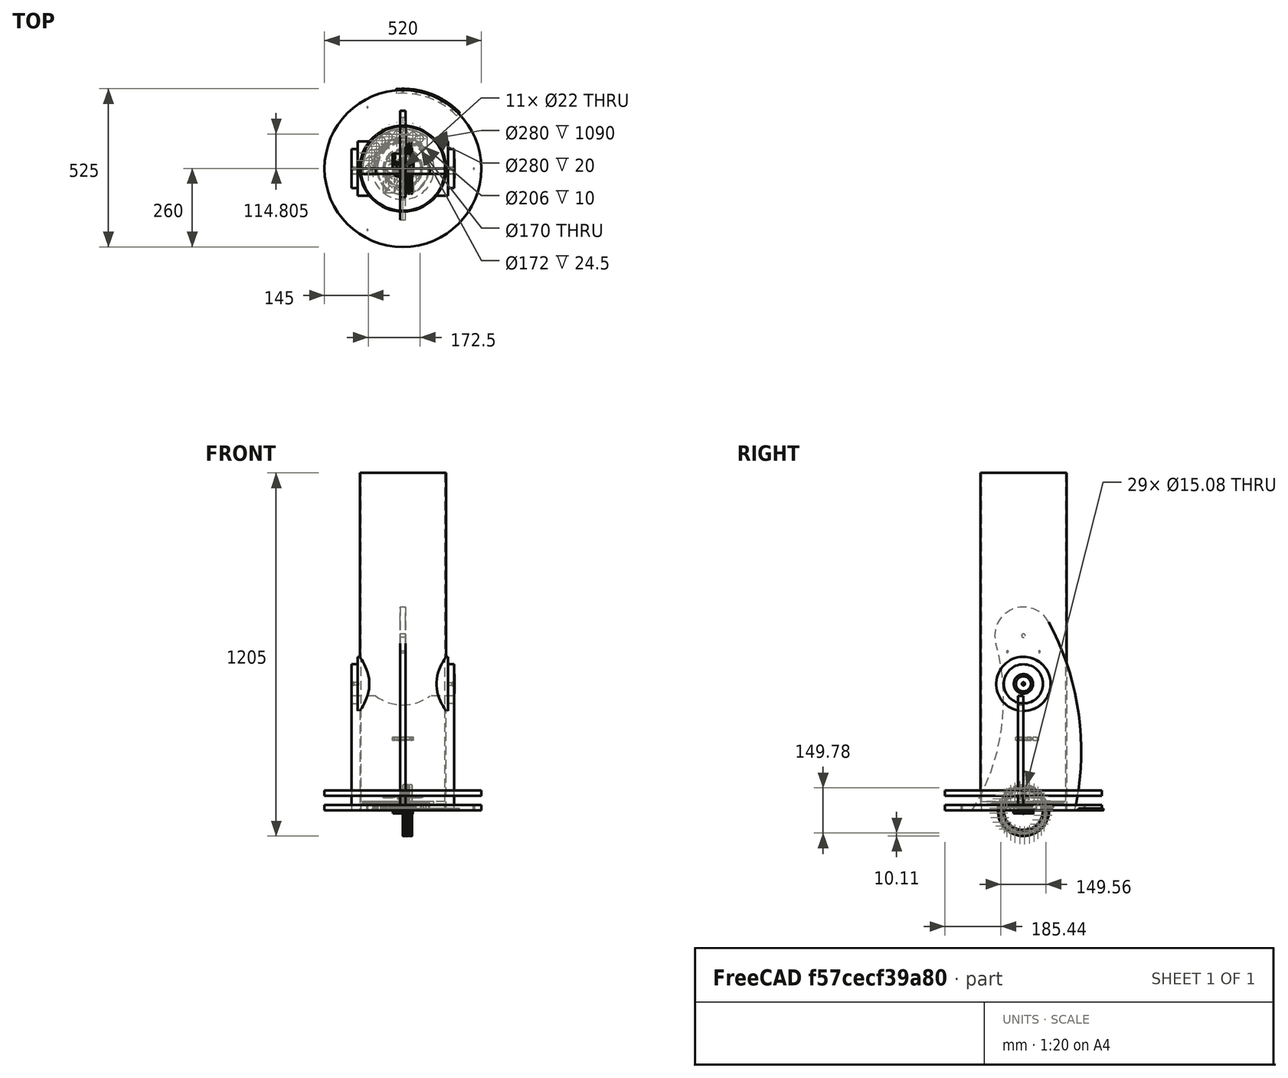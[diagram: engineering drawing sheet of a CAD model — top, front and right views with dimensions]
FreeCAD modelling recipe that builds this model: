
FCSTD DOCUMENT  (FreeCAD 1.1R20251125 (Git shallow))
Label: telescope
License: All rights reserved
LicenseURL: https://en.wikipedia.org/wiki/All_rights_reserved
objects: Sketcher::SketchObject×83, App::Link×62, PartDesign::Pocket×49, App::FeaturePython×38, App::Point×33, PartDesign::Pad×26, PartDesign::Body×21, Part::Feature×14, PartDesign::Chamfer×12, PartDesign::PolarPattern×8, App::Part×8, PartDesign::Fillet×7, PartDesign::LinearPattern×6, PartDesign::FeatureBase×6, Part::FeaturePython×6, PartDesign::MultiTransform×4, PartDesign::Plane×4, PartDesign::Groove×4, Assembly::JointGroup×4, Assembly::AssemblyObject×4, +6 more types
note: 565 computed .brp shape members not serialized (recipe doc carries the construction recipe); baked Part::Feature solids carry a one-line shape summary decoded from their .brp

FEATURE [Sketcher::SketchObject] Sketch002
  ArcFitTolerance = 0
  AttachmentSupport = -> [XY_Plane]
  ExternalTypes = [0]
  FullyConstrained = true
  MakeInternals = false
  MapMode = 5
  sketch-geometry (1):
    g0: Circle CenterX=0 CenterY=0 CenterZ=0 NormalX=0 NormalY=0 NormalZ=1 AngleXU=0 Radius=7
  constraints (2):
    c: Coincident(g0,g-1)
    c: Diameter(g0) = 14
FEATURE [Sketcher::SketchObject] Sketch
  ArcFitTolerance = 0
  AttachmentSupport = -> [XY_Plane]
  ExternalTypes = [0]
  FullyConstrained = true
  MakeInternals = false
  MapMode = 5
  sketch-geometry (1):
    g0: Circle CenterX=0 CenterY=0 CenterZ=0 NormalX=0 NormalY=0 NormalZ=1 AngleXU=0 Radius=260
  constraints (2):
    c: Coincident(g0,g-1)
    c: Diameter(g0) = 520
FEATURE [PartDesign::Pad] Pad
  AllowMultiFace = false
  Direction = (0,0,1)
  Length = 18
  Length2 = 100
  Profile = -> Sketch
  SideType = 0
  Suppressed = false
  Type = 0
  Type2 = 0
FEATURE [Sketcher::SketchObject] Sketch001
  ArcFitTolerance = 0
  AttachmentSupport = -> [Pad]
  ExternalTypes = [0]
  FullyConstrained = true
  MakeInternals = false
  MapMode = 5
  Placement = pos=(0,0,18) rot=(0,0,1;0rad)
  sketch-geometry (1):
    g0: Circle CenterX=235 CenterY=0 CenterZ=0 NormalX=0 NormalY=0 NormalZ=1 AngleXU=0 Radius=2
  constraints (3):
    c: PointOnObject(g0,g-1)
    c: DistanceX(g0) = 235
    c: Radius(g0) = 2
FEATURE [PartDesign::Pocket] Pocket
  AllowMultiFace = false
  BaseFeature = -> Pad
  Direction = (0,0,-1)
  Length = 5
  Length2 = 100
  Profile = -> Sketch001
  SideType = 0
  Suppressed = false
  Type = 1
  Type2 = 0
FEATURE [PartDesign::PolarPattern] PolarPattern
  Angle = 360
  Axis = -> Sketch001 [N_Axis]
  BaseFeature = -> Pocket
  Mode = 0
  Occurrences = 3
  Offset = 120
  Originals = -> [Pocket]
  SpacingPattern = [0]
  Spacings = [-1,-1]
  Suppressed = false
  TransformMode = 0
FEATURE [PartDesign::Pocket] Pocket001
  BaseFeature = -> PolarPattern
  Direction = (0,0,-1)
  Length = 5
  Length2 = 100
  Profile = -> Sketch002
  Reversed = true
  SideType = 0
  Suppressed = false
  Type = 1
  Type2 = 0
FEATURE [PartDesign::Body] Body  label="base_bottom_plate"
  AllowCompound = true
  Group = -> [Sketch,Pad,Sketch001,Pocket,PolarPattern,Sketch002,Pocket001]
  Origin = -> Origin
  Tip = -> Pocket001
FEATURE [Part::Feature] Solid001  label="_51126_PART2"
  shape: bbox 9.646 x 184 x 184 mm, 9 faces (baked)
FEATURE [Part::Feature] Solid003  label="_51126_PART4"
  shape: bbox 15.08 x 15.08 x 15.08 mm, 1 faces (baked)
FEATURE [App::Link] Link004  label="_51126_PART009"
  LinkPlacement = pos=(0,0,0) rot=(-1,0,0;1.08331rad)
  LinkedObject = -> Solid003
  Placement = pos=(0,0,0) rot=(-1,0,0;1.08331rad)
FEATURE [App::Link] Link  label="_51126_PART005"
  LinkPlacement = pos=(0,0,0) rot=(-1,0,0;0.216662rad)
  LinkedObject = -> Solid003
  Placement = pos=(0,0,0) rot=(-1,0,0;0.216662rad)
FEATURE [App::Link] Link017  label="_51126_PART022"
  LinkPlacement = pos=(0,0,0) rot=(1,0,0;2.38328rad)
  LinkedObject = -> Solid003
  Placement = pos=(0,0,0) rot=(1,0,0;2.38328rad)
FEATURE [App::Link] Link002  label="_51126_PART007"
  LinkPlacement = pos=(0,0,0) rot=(-1,0,0;0.649985rad)
  LinkedObject = -> Solid003
  Placement = pos=(0,0,0) rot=(-1,0,0;0.649985rad)
FEATURE [App::Link] Link027  label="_51126_PART032"
  LinkPlacement = pos=(0,0,0) rot=(1,0,0;0.216662rad)
  LinkedObject = -> Solid003
  Placement = pos=(0,0,0) rot=(1,0,0;0.216662rad)
FEATURE [App::Link] Link023  label="_51126_PART028"
  LinkPlacement = pos=(0,0,0) rot=(1,0,0;1.08331rad)
  LinkedObject = -> Solid003
  Placement = pos=(0,0,0) rot=(1,0,0;1.08331rad)
FEATURE [App::Link] Link024  label="_51126_PART029"
  LinkPlacement = pos=(0,0,0) rot=(1,0,0;0.866646rad)
  LinkedObject = -> Solid003
  Placement = pos=(0,0,0) rot=(1,0,0;0.866646rad)
FEATURE [App::Link] Link010  label="_51126_PART015"
  LinkPlacement = pos=(0,0,0) rot=(1,0,0;3.89991rad)
  LinkedObject = -> Solid003
  Placement = pos=(0,0,0) rot=(1,0,0;3.89991rad)
FEATURE [App::Link] Link014  label="_51126_PART019"
  LinkPlacement = pos=(0,0,0) rot=(1,0,0;3.03326rad)
  LinkedObject = -> Solid003
  Placement = pos=(0,0,0) rot=(1,0,0;3.03326rad)
FEATURE [App::Link] Link022  label="_51126_PART027"
  LinkPlacement = pos=(0,0,0) rot=(1,0,0;1.29997rad)
  LinkedObject = -> Solid003
  Placement = pos=(0,0,0) rot=(1,0,0;1.29997rad)
FEATURE [App::Link] Link026  label="_51126_PART031"
  LinkPlacement = pos=(0,0,0) rot=(1,0,0;0.433323rad)
  LinkedObject = -> Solid003
  Placement = pos=(0,0,0) rot=(1,0,0;0.433323rad)
FEATURE [App::Link] Link021  label="_51126_PART026"
  LinkPlacement = pos=(0,0,0) rot=(1,0,0;1.51663rad)
  LinkedObject = -> Solid003
  Placement = pos=(0,0,0) rot=(1,0,0;1.51663rad)
FEATURE [App::Link] Link016  label="_51126_PART021"
  LinkPlacement = pos=(0,0,0) rot=(1,0,0;2.59994rad)
  LinkedObject = -> Solid003
  Placement = pos=(0,0,0) rot=(1,0,0;2.59994rad)
FEATURE [App::Link] Link015  label="_51126_PART020"
  LinkPlacement = pos=(0,0,0) rot=(1,0,0;2.8166rad)
  LinkedObject = -> Solid003
  Placement = pos=(0,0,0) rot=(1,0,0;2.8166rad)
FEATURE [App::Link] Link013  label="_51126_PART018"
  LinkPlacement = pos=(0,0,0) rot=(1,0,0;3.24992rad)
  LinkedObject = -> Solid003
  Placement = pos=(0,0,0) rot=(1,0,0;3.24992rad)
FEATURE [App::Link] Link012  label="_51126_PART017"
  LinkPlacement = pos=(0,0,0) rot=(1,0,0;3.46658rad)
  LinkedObject = -> Solid003
  Placement = pos=(0,0,0) rot=(1,0,0;3.46658rad)
FEATURE [App::Link] Link019  label="_51126_PART024"
  LinkPlacement = pos=(0,0,0) rot=(1,0,0;1.94995rad)
  LinkedObject = -> Solid003
  Placement = pos=(0,0,0) rot=(1,0,0;1.94995rad)
FEATURE [App::Link] Link020  label="_51126_PART025"
  LinkPlacement = pos=(0,0,0) rot=(1,0,0;1.73329rad)
  LinkedObject = -> Solid003
  Placement = pos=(0,0,0) rot=(1,0,0;1.73329rad)
FEATURE [App::Link] Link001  label="_51126_PART006"
  LinkPlacement = pos=(0,0,0) rot=(-1,0,0;0.433323rad)
  LinkedObject = -> Solid003
  Placement = pos=(0,0,0) rot=(-1,0,0;0.433323rad)
FEATURE [App::Link] Link006  label="_51126_PART011"
  LinkPlacement = pos=(0,0,0) rot=(-1,0,0;1.51663rad)
  LinkedObject = -> Solid003
  Placement = pos=(0,0,0) rot=(-1,0,0;1.51663rad)
FEATURE [App::Link] Link007  label="_51126_PART012"
  LinkPlacement = pos=(0,0,0) rot=(-1,0,0;1.73329rad)
  LinkedObject = -> Solid003
  Placement = pos=(0,0,0) rot=(-1,0,0;1.73329rad)
FEATURE [App::Link] Link025  label="_51126_PART030"
  LinkPlacement = pos=(0,0,0) rot=(1,0,0;0.649985rad)
  LinkedObject = -> Solid003
  Placement = pos=(0,0,0) rot=(1,0,0;0.649985rad)
FEATURE [App::Link] Link011  label="_51126_PART016"
  LinkPlacement = pos=(0,0,0) rot=(1,0,0;3.68325rad)
  LinkedObject = -> Solid003
  Placement = pos=(0,0,0) rot=(1,0,0;3.68325rad)
FEATURE [App::Link] Link009  label="_51126_PART014"
  LinkPlacement = pos=(0,0,0) rot=(1,0,0;4.11657rad)
  LinkedObject = -> Solid003
  Placement = pos=(0,0,0) rot=(1,0,0;4.11657rad)
FEATURE [App::Link] Link005  label="_51126_PART010"
  LinkPlacement = pos=(0,0,0) rot=(-1,0,0;1.29997rad)
  LinkedObject = -> Solid003
  Placement = pos=(0,0,0) rot=(-1,0,0;1.29997rad)
FEATURE [Part::Feature] Solid002  label="_51126_PART3"
  shape: bbox 15 x 184 x 184 mm, 8 faces (baked)
FEATURE [App::Link] Link008  label="_51126_PART013"
  LinkPlacement = pos=(0,0,0) rot=(-1,0,0;1.94995rad)
  LinkedObject = -> Solid003
  Placement = pos=(0,0,0) rot=(-1,0,0;1.94995rad)
FEATURE [App::Link] Link018  label="_51126_PART023"
  LinkPlacement = pos=(0,0,0) rot=(1,0,0;2.16662rad)
  LinkedObject = -> Solid003
  Placement = pos=(0,0,0) rot=(1,0,0;2.16662rad)
FEATURE [App::Link] Link003  label="_51126_PART008"
  LinkPlacement = pos=(0,0,0) rot=(-1,0,0;0.866646rad)
  LinkedObject = -> Solid003
  Placement = pos=(0,0,0) rot=(-1,0,0;0.866646rad)
FEATURE [App::FeaturePython] Constraints  # WARN: FeaturePython — macro-defined, semantics opaque (R4)
  _Version = 1
FEATURE [Part::Feature] Solid  label="_51126_PART1"
  shape: bbox 7.541 x 184 x 184 mm, 35 faces (baked)
FEATURE [App::Part] Part  label="bearing-51126"
  Group = -> [Solid001,Link004,Link,Link017,Link002,Link027,Link023,Link024,Link010,Link014,Link022,Link026,Link021,Solid003,Link016,Link015,Link013,Link012,Link019,Link020,Link001,Link006,Link007,Link025,Link011,Link009,Link005,Solid002,Link008,Link018,Link003,Constraints,Solid]
  Origin = -> Origin001
  Placement = pos=(-4.26e-14,-3.08e-14,18) rot=(0.707107,0,0.707107;3.14159rad)
FEATURE [Sketcher::SketchObject] Sketch003
  ArcFitTolerance = 0
  AttachmentSupport = -> [XY_Plane003]
  ExternalTypes = [0]
  FullyConstrained = true
  MakeInternals = false
  MapMode = 5
  sketch-geometry (7):
    g0: ArcOfCircle CenterX=0 CenterY=0 CenterZ=0 NormalX=0 NormalY=0 NormalZ=1 AngleXU=0 Radius=60 StartAngle=1.65423 EndAngle=3.58176
    g1: ArcOfCircle CenterX=0 CenterY=0 CenterZ=0 NormalX=0 NormalY=0 NormalZ=1 AngleXU=0 Radius=10 StartAngle=2.0944 EndAngle=3.14159
    g2: LineSegment StartX=-5 StartY=8.66025 StartZ=0 EndX=-5 EndY=59.7913 EndZ=0
    g3: LineSegment [constr] StartX=0 StartY=0 StartZ=0 EndX=-86.6025 EndY=-50 EndZ=0
    g4: LineSegment StartX=-10 StartY=1.2e-15 StartZ=0 EndX=-54.2808 EndY=-25.5655 EndZ=0
    g5: LineSegment [constr] StartX=-10 StartY=1.2e-15 StartZ=0 EndX=0 EndY=0 EndZ=0
    g6: Circle CenterX=0 CenterY=50 CenterZ=0 NormalX=0 NormalY=0 NormalZ=1 AngleXU=0 Radius=2
  constraints (20):
    c: Coincident(g0,g-1)
    c: Coincident(g1,g0)
    c: Vertical(g2)
    c: Coincident(g3,g0)
    c: Angle(g3) = -2.61799
    c: Parallel(g4,g3)
    c: Diameter(g0) = 120
    c: Coincident(g5,g4)
    c: Coincident(g5,g0)
    c: Coincident(g0,g2)
    c: Coincident(g0,g4)
    c: Coincident(g1,g2)
    c: DistanceX(g1) = -5
    c: Diameter(g1) = 20
    c: Distance(g1,g3) = 5
    c: Coincident(g4,g1)
    c: Distance(g3) = 100
    c: PointOnObject(g6,g-2)
    c: Diameter(g6) = 4
    c: DistanceY(g6) = 50
FEATURE [Sketcher::SketchObject] Sketch004
  ArcFitTolerance = 0
  AttachmentSupport = -> [XY_Plane003]
  ExternalTypes = [0]
  FullyConstrained = true
  MakeInternals = false
  MapMode = 5
  sketch-geometry (1):
    g0: Circle CenterX=0 CenterY=0 CenterZ=0 NormalX=0 NormalY=0 NormalZ=1 AngleXU=0 Radius=5.5
  constraints (2):
    c: Coincident(g0,g-1)
    c: Diameter(g0) = 11
FEATURE [Sketcher::SketchObject] Sketch005
  ArcFitTolerance = 0
  AttachmentSupport = -> [XY_Plane003]
  ExternalTypes = [0]
  FullyConstrained = true
  MakeInternals = false
  MapMode = 5
  sketch-geometry (1):
    g0: Circle CenterX=0 CenterY=0 CenterZ=0 NormalX=0 NormalY=0 NormalZ=1 AngleXU=0 Radius=65.25
  constraints (2):
    c: Coincident(g0,g-1)
    c: Diameter(g0) = 130.5
FEATURE [PartDesign::Pad] Pad001
  Direction = (0,0,1)
  Length = 6
  Length2 = 100
  Profile = -> Sketch005
  SideType = 0
  Suppressed = false
  Type = 0
  Type2 = 0
FEATURE [PartDesign::Pocket] Pocket002
  BaseFeature = -> Pad001
  Direction = (0,0,-1)
  Length = 5
  Length2 = 100
  Profile = -> Sketch004
  Reversed = true
  SideType = 0
  Suppressed = false
  Type = 1
  Type2 = 0
FEATURE [PartDesign::Pocket] Pocket003
  BaseFeature = -> Pocket002
  Direction = (0,0,-1)
  Length = 5
  Length2 = 100
  Profile = -> Sketch003
  Reversed = true
  SideType = 0
  Suppressed = false
  Type = 1
  Type2 = 0
FEATURE [PartDesign::PolarPattern] PolarPattern001
  Angle = 360
  Axis = -> Sketch003 [N_Axis]
  BaseFeature = -> Pocket003
  Mode = 0
  Occurrences = 3
  Offset = 120
  Originals = -> [Pocket003]
  SpacingPattern = [0]
  Spacings = [-1,-1]
  Suppressed = false
  TransformMode = 0
FEATURE [PartDesign::Chamfer] Chamfer
  Angle = 45
  Base = -> PolarPattern001 [Edge3,Edge2]
  BaseFeature = -> PolarPattern001
  ChamferType = 0
  FlipDirection = false
  Size = 1
  Size2 = 1
  SupportTransform = true
  Suppressed = false
  UseAllEdges = false
FEATURE [PartDesign::Fillet] Fillet
  Base = -> Chamfer [Edge49,Edge46,Edge54,Edge52,Edge42,Edge40]
  BaseFeature = -> Chamfer
  Radius = 6
  SupportTransform = true
  Suppressed = false
  UseAllEdges = false
FEATURE [Sketcher::SketchObject] Sketch006
  ArcFitTolerance = 0
  AttachmentSupport = -> [Fillet]
  ExternalTypes = [0]
  FullyConstrained = true
  MakeInternals = false
  MapMode = 5
  Placement = pos=(0,0,6) rot=(0,0,1;0rad)
  sketch-geometry (1):
    g0: Circle CenterX=0 CenterY=0 CenterZ=0 NormalX=0 NormalY=0 NormalZ=1 AngleXU=0 Radius=63
  constraints (2):
    c: Coincident(g0,g-1)
    c: Diameter(g0) = 126
FEATURE [PartDesign::Pocket] Pocket004
  BaseFeature = -> Fillet
  Direction = (0,0,-1)
  Length = 3
  Length2 = 100
  Profile = -> Sketch006
  SideType = 0
  Suppressed = false
  Type = 0
  Type2 = 0
FEATURE [PartDesign::Body] Body001  label="bearing-bottom-location-ring"
  AllowCompound = true
  Group = -> [Sketch005,Pad001,Sketch004,Pocket002,Sketch003,Pocket003,PolarPattern001,Chamfer,Fillet,Sketch006,Pocket004]
  Origin = -> Origin003
  Placement = pos=(0,0,18) rot=(0,0,1;0rad)
  Tip = -> Pocket004
FEATURE [Sketcher::SketchObject] Sketch007
  ArcFitTolerance = 0
  AttachmentSupport = -> [XY_Plane004]
  ExternalTypes = [0]
  FullyConstrained = true
  MakeInternals = false
  MapMode = 5
  sketch-geometry (2):
    g0: Circle CenterX=0 CenterY=0 CenterZ=0 NormalX=0 NormalY=0 NormalZ=1 AngleXU=0 Radius=5.25
    g1: Circle CenterX=0 CenterY=0 CenterZ=0 NormalX=0 NormalY=0 NormalZ=1 AngleXU=0 Radius=7.25
  constraints (4):
    c: Coincident(g0,g-1)
    c: Coincident(g1,g0)
    c: Diameter(g0) = 10.5
    c: Diameter(g1) = 14.5
FEATURE [PartDesign::Pad] Pad002
  Direction = (0,0,1)
  Length = 17
  Length2 = 100
  Profile = -> Sketch007
  SideType = 0
  Suppressed = false
  Type = 0
  Type2 = 0
FEATURE [PartDesign::Chamfer] Chamfer001
  Angle = 45
  Base = -> Pad002 [Edge3]
  BaseFeature = -> Pad002
  ChamferType = 0
  FlipDirection = false
  Size = 1
  Size2 = 1
  SupportTransform = true
  Suppressed = false
  UseAllEdges = false
FEATURE [PartDesign::Body] Body002  label="m10to14.5-bolt-sleeve"
  AllowCompound = true
  Group = -> [Sketch007,Pad002,Chamfer001]
  Origin = -> Origin004
  Tip = -> Chamfer001
FEATURE [Sketcher::SketchObject] Sketch012
  ArcFitTolerance = 0
  AttachmentSupport = -> [XY_Plane009]
  ExternalTypes = [0]
  FullyConstrained = true
  MakeInternals = false
  MapMode = 5
  sketch-geometry (1):
    g0: Circle CenterX=0 CenterY=0 CenterZ=0 NormalX=0 NormalY=0 NormalZ=1 AngleXU=0 Radius=7
  constraints (2):
    c: Coincident(g0,g-1)
    c: Diameter(g0) = 14
FEATURE [Sketcher::SketchObject] Sketch013
  ArcFitTolerance = 0
  AttachmentSupport = -> [XY_Plane009]
  ExternalTypes = [0]
  FullyConstrained = true
  MakeInternals = false
  MapMode = 5
  sketch-geometry (1):
    g0: Circle CenterX=0 CenterY=0 CenterZ=0 NormalX=0 NormalY=0 NormalZ=1 AngleXU=0 Radius=260
  constraints (2):
    c: Coincident(g0,g-1)
    c: Radius(g0) = 260
FEATURE [PartDesign::Pad] Pad003
  AllowMultiFace = false
  Direction = (0,0,1)
  Length = 18
  Length2 = 100
  Profile = -> Sketch013
  SideType = 0
  Suppressed = false
  Type = 0
  Type2 = 0
FEATURE [PartDesign::Pocket] Pocket009
  BaseFeature = -> Pad003
  Direction = (0,0,-1)
  Length = 5
  Length2 = 100
  Profile = -> Sketch012
  Reversed = true
  SideType = 0
  Suppressed = false
  Type = 1
  Type2 = 0
FEATURE [Sketcher::SketchObject] Sketch014
  ArcFitTolerance = 0
  AttachmentSupport = -> [Pocket009]
  ExternalTypes = [0]
  FullyConstrained = true
  MakeInternals = false
  MapMode = 5
  Placement = pos=(0,0,18) rot=(0,0,1;0rad)
  sketch-geometry (4):
    g0: LineSegment StartX=-170 StartY=150 StartZ=0 EndX=170 EndY=150 EndZ=0
    g1: LineSegment StartX=-170 StartY=150 StartZ=0 EndX=-170 EndY=0 EndZ=0
    g2: LineSegment StartX=170 StartY=150 StartZ=0 EndX=170 EndY=0 EndZ=0
    g3: LineSegment StartX=-28 StartY=-227 StartZ=0 EndX=28 EndY=-227 EndZ=0
  constraints (12):
    c: Symmetric(g0,g0,g-2)
    c: DistanceX(g0,g0) = 340
    c: DistanceY(g0) = 150
    c: Coincident(g1,g0)
    c: PointOnObject(g1,g-1)
    c: Vertical(g1)
    c: Coincident(g2,g0)
    c: PointOnObject(g2,g-1)
    c: Vertical(g2)
    c: Symmetric(g3,g3,g-2)
    c: DistanceX(g3,g3) = 56
    c: DistanceY(g3) = -227
FEATURE [PartDesign::Body] Body004  label="fork-bottom-plate"
  AllowCompound = true
  Group = -> [Sketch013,Pad003,Sketch012,Pocket009,Sketch014]
  Origin = -> Origin009
  Placement = pos=(0,0,48) rot=(0,0,1;0.004518rad)
  Tip = -> Pocket009
FEATURE [Sketcher::SketchObject] Sketch015
  ArcFitTolerance = 0
  AttachmentSupport = -> [XY_Plane010]
  ExternalTypes = [0]
  FullyConstrained = true
  MakeInternals = false
  MapMode = 5
  sketch-geometry (7):
    g0: ArcOfCircle CenterX=0 CenterY=0 CenterZ=0 NormalX=0 NormalY=0 NormalZ=1 AngleXU=0 Radius=60 StartAngle=1.65423 EndAngle=3.58176
    g1: ArcOfCircle CenterX=0 CenterY=0 CenterZ=0 NormalX=0 NormalY=0 NormalZ=1 AngleXU=0 Radius=10 StartAngle=2.0944 EndAngle=3.14159
    g2: LineSegment StartX=-5 StartY=8.66025 StartZ=0 EndX=-5 EndY=59.7913 EndZ=0
    g3: LineSegment [constr] StartX=0 StartY=0 StartZ=0 EndX=-86.6025 EndY=-50 EndZ=0
    g4: LineSegment StartX=-10 StartY=1.2e-15 StartZ=0 EndX=-54.2808 EndY=-25.5655 EndZ=0
    g5: LineSegment [constr] StartX=-10 StartY=1.2e-15 StartZ=0 EndX=0 EndY=0 EndZ=0
    g6: Circle CenterX=0 CenterY=50 CenterZ=0 NormalX=0 NormalY=0 NormalZ=1 AngleXU=0 Radius=2
  constraints (20):
    c: Coincident(g0,g-1)
    c: Coincident(g1,g0)
    c: Vertical(g2)
    c: Coincident(g3,g0)
    c: Angle(g3) = -2.61799
    c: Parallel(g4,g3)
    c: Diameter(g0) = 120
    c: Coincident(g5,g4)
    c: Coincident(g5,g0)
    c: Coincident(g0,g2)
    c: Coincident(g0,g4)
    c: Coincident(g1,g2)
    c: DistanceX(g1) = -5
    c: Diameter(g1) = 20
    c: Distance(g1,g3) = 5
    c: Coincident(g4,g1)
    c: Distance(g3) = 100
    c: PointOnObject(g6,g-2)
    c: Diameter(g6) = 4
    c: DistanceY(g6) = 50
FEATURE [Sketcher::SketchObject] Sketch016
  ArcFitTolerance = 0
  AttachmentSupport = -> [XY_Plane010]
  ExternalTypes = [0]
  FullyConstrained = true
  MakeInternals = false
  MapMode = 5
  sketch-geometry (1):
    g0: Circle CenterX=0 CenterY=0 CenterZ=0 NormalX=0 NormalY=0 NormalZ=1 AngleXU=0 Radius=5.5
  constraints (2):
    c: Coincident(g0,g-1)
    c: Diameter(g0) = 11
FEATURE [Sketcher::SketchObject] Sketch017
  ArcFitTolerance = 0
  AttachmentSupport = -> [XY_Plane010]
  ExternalTypes = [0]
  FullyConstrained = true
  MakeInternals = false
  MapMode = 5
  sketch-geometry (1):
    g0: Circle CenterX=0 CenterY=0 CenterZ=0 NormalX=0 NormalY=0 NormalZ=1 AngleXU=0 Radius=66.25
  constraints (2):
    c: Coincident(g0,g-1)
    c: Diameter(g0) = 132.5
FEATURE [PartDesign::Pad] Pad004
  Direction = (0,0,1)
  Length = 6
  Length2 = 100
  Profile = -> Sketch017
  SideType = 0
  Suppressed = false
  Type = 0
  Type2 = 0
FEATURE [PartDesign::Pocket] Pocket010
  BaseFeature = -> Pad004
  Direction = (0,0,-1)
  Length = 5
  Length2 = 100
  Profile = -> Sketch016
  Reversed = true
  SideType = 0
  Suppressed = false
  Type = 1
  Type2 = 0
FEATURE [PartDesign::Pocket] Pocket011
  BaseFeature = -> Pocket010
  Direction = (0,0,-1)
  Length = 5
  Length2 = 100
  Profile = -> Sketch015
  Reversed = true
  SideType = 0
  Suppressed = false
  Type = 1
  Type2 = 0
FEATURE [PartDesign::PolarPattern] PolarPattern003
  Angle = 360
  Axis = -> Sketch015 [N_Axis]
  BaseFeature = -> Pocket011
  Mode = 0
  Occurrences = 3
  Offset = 120
  Originals = -> [Pocket011]
  SpacingPattern = [0]
  Spacings = [-1,-1]
  Suppressed = false
  TransformMode = 0
FEATURE [PartDesign::Chamfer] Chamfer002
  Angle = 45
  Base = -> PolarPattern003 [Edge3,Edge2]
  BaseFeature = -> PolarPattern003
  ChamferType = 0
  FlipDirection = false
  Size = 1
  Size2 = 1
  SupportTransform = true
  Suppressed = false
  UseAllEdges = false
FEATURE [PartDesign::Fillet] Fillet001
  Base = -> Chamfer002 [Edge49,Edge46,Edge54,Edge52,Edge42,Edge40]
  BaseFeature = -> Chamfer002
  Radius = 6
  SupportTransform = true
  Suppressed = false
  UseAllEdges = false
FEATURE [Sketcher::SketchObject] Sketch018
  ArcFitTolerance = 0
  AttachmentSupport = -> [Fillet001]
  ExternalTypes = [0]
  FullyConstrained = true
  MakeInternals = false
  MapMode = 5
  Placement = pos=(0,0,6) rot=(0,0,1;0rad)
  sketch-geometry (1):
    g0: Circle CenterX=0 CenterY=0 CenterZ=0 NormalX=0 NormalY=0 NormalZ=1 AngleXU=0 Radius=64
  constraints (2):
    c: Coincident(g0,g-1)
    c: Diameter(g0) = 128
FEATURE [PartDesign::Pocket] Pocket012
  BaseFeature = -> Fillet001
  Direction = (0,0,-1)
  Length = 3
  Length2 = 100
  Profile = -> Sketch018
  SideType = 0
  Suppressed = false
  Type = 0
  Type2 = 0
FEATURE [PartDesign::Body] Body005  label="bearing-top-location-ring"
  AllowCompound = true
  Group = -> [Sketch017,Pad004,Sketch016,Pocket010,Sketch015,Pocket011,PolarPattern003,Chamfer002,Fillet001,Sketch018,Pocket012]
  Origin = -> Origin010
  Placement = pos=(0,0,48) rot=(0.999999,-0.001422,0;3.14159rad)
  Tip = -> Pocket012
FEATURE [App::Link] Link028  label="base-bottom-plate001"
  LinkedObject = -> Body
FEATURE [App::Link] Link029  label="bearing-51126_001"
  LinkPlacement = pos=(0,0,18) rot=(0,1,0;4.71239rad)
  LinkedObject = -> Part
  Placement = pos=(0,0,18) rot=(0,1,0;4.71239rad)
FEATURE [App::FeaturePython] Fixed  # Assembly joint (typed FeaturePython)
  Angle = 0
  AngleMax = 0
  AngleMin = 0
  Detach1 = false
  Detach2 = false
  Distance = 0
  Distance2 = 0
  EnableAngleMax = false
  EnableAngleMin = false
  EnableLengthMax = false
  EnableLengthMin = false
  EnableLimits = false
  JointType = 0 (Fixed)
  LengthMax = 0
  LengthMin = 0
  Object1 = -> Solid001 [Edge1,Edge1]
  Object2 = -> Link028 [Edge9,Edge9]
  Placement1 = pos=(0,0,0) rot=(0,1,0;1.5708rad)
  Placement2 = pos=(0,0,18) rot=(1,0,0;3.14159rad)
  Reference1 = -> Assembly002 [Assembly.Link029.Solid001.Edge1,Assembly.Link029.Solid001.Edge1]
  Reference2 = -> Assembly002 [Assembly.Link028.Edge9,Assembly.Link028.Edge9]
  Suppressed = false
FEATURE [App::Link] Link030  label="bearing-bottom-location-ring001"
  LinkPlacement = pos=(0,0,18) rot=(0,0,1;0rad)
  LinkedObject = -> Body001
  Placement = pos=(0,0,18) rot=(0,0,1;0rad)
FEATURE [App::FeaturePython] Fixed001  # Assembly joint (typed FeaturePython)
  Angle = 0
  AngleMax = 0
  AngleMin = 0
  Detach1 = false
  Detach2 = false
  Distance = 0
  Distance2 = 0
  EnableAngleMax = false
  EnableAngleMin = false
  EnableLengthMax = false
  EnableLengthMin = false
  EnableLimits = false
  JointType = 0 (Fixed)
  LengthMax = 0
  LengthMin = 0
  Object1 = -> Link028 [Edge9,Edge9]
  Object2 = -> Link030 [Edge10,Edge10]
  Placement1 = pos=(0,0,18) rot=(1,0,0;3.14159rad)
  Reference1 = -> Assembly002 [Assembly.Link028.Edge9,Assembly.Link028.Edge9]
  Reference2 = -> Assembly002 [Assembly.Link030.Edge10,Assembly.Link030.Edge10]
  Suppressed = false
FEATURE [App::Link] Link031  label="m10to14.5-bolt-sleeve001"
  LinkedObject = -> Body002
FEATURE [App::FeaturePython] Fixed002  # Assembly joint (typed FeaturePython)
  Angle = 0
  AngleMax = 0
  AngleMin = 0
  Detach1 = false
  Detach2 = false
  Distance = 0
  Distance2 = 0
  EnableAngleMax = false
  EnableAngleMin = false
  EnableLengthMax = false
  EnableLengthMin = false
  EnableLimits = false
  JointType = 0 (Fixed)
  LengthMax = 0
  LengthMin = 0
  Object1 = -> Link031 [Edge3,Edge3]
  Object2 = -> Link028 [Edge5,Edge5]
  Reference1 = -> Assembly002 [Assembly.Link031.Edge3,Assembly.Link031.Edge3]
  Reference2 = -> Assembly002 [Assembly.Link028.Edge5,Assembly.Link028.Edge5]
  Suppressed = false
FEATURE [App::Link] Link032  label="fork-bottom-plate001"
  LinkPlacement = pos=(0,0,48) rot=(0,0,1;0.068094rad)
  LinkedObject = -> Body004
  Placement = pos=(0,0,48) rot=(0,0,1;0.068094rad)
FEATURE [App::Link] Link033  label="vertical-axis-main-gear001"
  LinkPlacement = pos=(0,0,22) rot=(0.984808,-0.173648,0;3.14159rad)
  LinkedObject = -> Part001
  Placement = pos=(0,0,22) rot=(0.984808,-0.173648,0;3.14159rad)
FEATURE [App::FeaturePython] Fixed003  # Assembly joint (typed FeaturePython)
  Angle = 0
  AngleMax = 0
  AngleMin = 0
  Detach1 = false
  Detach2 = false
  Distance = 0
  Distance2 = 0
  EnableAngleMax = false
  EnableAngleMin = false
  EnableLengthMax = false
  EnableLengthMin = false
  EnableLimits = false
  JointType = 0 (Fixed)
  LengthMax = 0
  LengthMin = 0
  Object1 = -> Body003 [Edge966,Edge966]
  Object2 = -> Link028 [Edge3,Edge3]
  Offset2 = pos=(0,0,0) rot=(0,0,-1;0.349066rad)
  Placement1 = pos=(0,0,4) rot=(0,0,1;0rad)
  Placement2 = pos=(0,0,18) rot=(0,0,-1;0.349066rad)
  Reference1 = -> Assembly002 [Assembly.Link033.Body003.Edge966,Assembly.Link033.Body003.Edge966]
  Reference2 = -> Assembly002 [Assembly.Link028.Edge3,Assembly.Link028.Edge3]
  Suppressed = false
FEATURE [App::Link] Link034  label="vertical-axis-main-gear002"
  LinkPlacement = pos=(0,0,22) rot=(0.816642,-0.577145,0;3.14159rad)
  LinkedObject = -> Part001
  Placement = pos=(0,0,22) rot=(0.816642,-0.577145,0;3.14159rad)
FEATURE [App::Link] Link035  label="vertical-axis-main-gear003"
  LinkPlacement = pos=(0,0,22) rot=(0.964787,0.263031,0;3.14159rad)
  LinkedObject = -> Part001
  Placement = pos=(0,0,22) rot=(0.964787,0.263031,0;3.14159rad)
FEATURE [App::FeaturePython] Fixed004  # Assembly joint (typed FeaturePython)
  Angle = 0
  AngleMax = 0
  AngleMin = 0
  Detach1 = false
  Detach2 = false
  Distance = 0
  Distance2 = 0
  EnableAngleMax = false
  EnableAngleMin = false
  EnableLengthMax = false
  EnableLengthMin = false
  EnableLimits = false
  JointType = 0 (Fixed)
  LengthMax = 0
  LengthMin = 0
  Object1 = -> Body003 [Edge966,Edge966]
  Object2 = -> Link028 [Edge3,Edge3]
  Offset2 = pos=(0,0,0) rot=(0,0,1;0.532325rad)
  Placement1 = pos=(0,0,4) rot=(0,0,1;0rad)
  Placement2 = pos=(0,0,18) rot=(0,0,1;0.532325rad)
  Reference1 = -> Assembly002 [Assembly.Link035.Body003.Edge966,Assembly.Link035.Body003.Edge966]
  Reference2 = -> Assembly002 [Assembly.Link028.Edge3,Assembly.Link028.Edge3]
  Suppressed = false
FEATURE [App::FeaturePython] Fixed005  # Assembly joint (typed FeaturePython)
  Angle = 0
  AngleMax = 0
  AngleMin = 0
  Detach1 = false
  Detach2 = false
  Distance = 0
  Distance2 = 0
  EnableAngleMax = false
  EnableAngleMin = false
  EnableLengthMax = false
  EnableLengthMin = false
  EnableLimits = false
  JointType = 0 (Fixed)
  LengthMax = 0
  LengthMin = 0
  Object1 = -> Body003 [Edge966,Edge966]
  Object2 = -> Link028 [Edge3,Edge3]
  Offset2 = pos=(0,0,0) rot=(0,0,-1;1.23046rad)
  Placement1 = pos=(0,0,4) rot=(0,0,1;0rad)
  Placement2 = pos=(0,0,18) rot=(0,0,-1;1.23046rad)
  Reference1 = -> Assembly002 [Assembly.Link034.Body003.Edge966,Assembly.Link034.Body003.Edge966]
  Reference2 = -> Assembly002 [Assembly.Link028.Edge3,Assembly.Link028.Edge3]
  Suppressed = false
FEATURE [App::Link] bearing_51126_hub_top  label="bearing-top-location-ring001"
  LinkPlacement = pos=(-3.6e-15,1.57e-14,48) rot=(0.99942,0.034041,0;3.14159rad)
  LinkedObject = -> Body005
  Placement = pos=(-3.6e-15,1.57e-14,48) rot=(0.99942,0.034041,0;3.14159rad)
FEATURE [Sketcher::SketchObject] Sketch019
  ArcFitTolerance = 0
  AttachmentSupport = -> [XZ_Plane011]
  ExternalTypes = [0]
  FullyConstrained = true
  MakeInternals = false
  MapMode = 5
  Placement = pos=(0,0,0) rot=(1,0,0;1.5708rad)
  sketch-geometry (5):
    g0: LineSegment StartX=85 StartY=0 StartZ=0 EndX=85 EndY=28.5 EndZ=0
    g1: LineSegment StartX=85 StartY=28.5 StartZ=0 EndX=84.5 EndY=29 EndZ=0
    g2: LineSegment StartX=84.5 StartY=29 StartZ=0 EndX=87 EndY=29 EndZ=0
    g3: LineSegment StartX=87 StartY=29 StartZ=0 EndX=87 EndY=0 EndZ=0
    g4: LineSegment StartX=87 StartY=0 StartZ=0 EndX=85 EndY=0 EndZ=0
  constraints (15):
    c: PointOnObject(g0,g-1)
    c: Vertical(g0)
    c: Coincident(g0,g1)
    c: Coincident(g1,g2)
    c: Coincident(g2,g3)
    c: PointOnObject(g3,g-1)
    c: Vertical(g3)
    c: Coincident(g3,g4)
    c: Coincident(g4,g0)
    c: Horizontal(g2)
    c: Angle(g1,g2) = 0.785398
    c: DistanceX(g0) = 85
    c: DistanceX(g4,g4) = 2
    c: DistanceX(g2,g2) = 2.5
    c: DistanceY(g3,g3) = 29
FEATURE [PartDesign::Revolution] Revolution
  Angle = 360
  Angle2 = 60
  Axis = (0,2e-16,1)
  Base = (0,0,0)
  Placement = pos=(0,0,0) rot=(1,0,0;1.5708rad)
  Profile = -> Sketch019
  ReferenceAxis = -> Sketch019 [V_Axis]
  Reversed = true
  Suppressed = false
  Type = 0
FEATURE [Sketcher::SketchObject] Sketch020
  ArcFitTolerance = 0
  AttachmentSupport = -> [Revolution]
  ExternalTypes = [0]
  FullyConstrained = true
  MakeInternals = false
  MapMode = 5
  Placement = pos=(0,0,0) rot=(1,0,0;3.14159rad)
  sketch-geometry (1):
    g0: Circle CenterX=0 CenterY=0 CenterZ=0 NormalX=0 NormalY=0 NormalZ=1 AngleXU=0 Radius=86
  constraints (2):
    c: Coincident(g0,g-1)
    c: Diameter(g0) = 172
FEATURE [PartDesign::Pocket] Pocket013
  BaseFeature = -> Revolution
  Direction = (0,0,1)
  Length = 25
  Length2 = 100
  Placement = pos=(0,0,0) rot=(1,0,0;1.5708rad)
  Profile = -> Sketch020
  SideType = 0
  Suppressed = false
  Type = 0
  Type2 = 0
FEATURE [PartDesign::Chamfer] Chamfer003
  Angle = 45
  Base = -> Pocket013 [Edge1,Edge8]
  BaseFeature = -> Pocket013
  ChamferType = 0
  FlipDirection = false
  Placement = pos=(0,0,0) rot=(1,0,0;1.5708rad)
  Size = 0.5
  Size2 = 1
  SupportTransform = true
  Suppressed = false
  UseAllEdges = false
FEATURE [PartDesign::Body] Body006  label="bearing-51126-cover"
  AllowCompound = true
  Group = -> [Sketch019,Revolution,Sketch020,Pocket013,Chamfer003]
  Origin = -> Origin011
  Tip = -> Chamfer003
FEATURE [App::Link] bearing_51126_cover  label="bearing_51126_cover001"
  LinkPlacement = pos=(-3.5e-15,1.56e-14,19) rot=(0,0,1;0.068094rad)
  LinkedObject = -> Body006
  Placement = pos=(-3.5e-15,1.56e-14,19) rot=(0,0,1;0.068094rad)
FEATURE [App::Link] Link036  label="m10to14.5-bolt-sleeve002"
  LinkPlacement = pos=(0,0,66) rot=(0.99942,0.034041,0;3.14159rad)
  LinkedObject = -> Body002
  Placement = pos=(0,0,66) rot=(0.99942,0.034041,0;3.14159rad)
FEATURE [Sketcher::SketchObject] Sketch021
  ArcFitTolerance = 0
  AttachmentSupport = -> [XY_Plane012]
  ExternalTypes = [0]
  FullyConstrained = true
  MakeInternals = false
  MapMode = 5
  sketch-geometry (4):
    g0: ArcOfCircle CenterX=-28 CenterY=15 CenterZ=0 NormalX=0 NormalY=0 NormalZ=1 AngleXU=0 Radius=2 StartAngle=3.14159 EndAngle=6.28319
    g1: ArcOfCircle CenterX=-28 CenterY=25 CenterZ=0 NormalX=0 NormalY=0 NormalZ=1 AngleXU=0 Radius=2 StartAngle=0 EndAngle=3.14159
    g2: LineSegment StartX=-26 StartY=15 StartZ=0 EndX=-26 EndY=25 EndZ=0
    g3: LineSegment StartX=-30 StartY=15 StartZ=0 EndX=-30 EndY=25 EndZ=0
  constraints (10):
    c: Tangent(g0,g3) = 1.5708
    c: Tangent(g0,g2) = -1.5708
    c: Tangent(g2,g1) = -1.5708
    c: Tangent(g3,g1) = 1.5708
    c: Vertical(g2)
    c: Equal(g0,g1)
    c: Radius(g1) = 2
    c: DistanceY(g0,g1) = 10
    c: DistanceY(g0) = 15
    c: DistanceX(g0,g-1) = 28
FEATURE [PartDesign::LinearPattern] LinearPattern
  Direction = -> Sketch021 [H_Axis]
  Length = 56
  Length2 = 100
  Mode = 0
  Mode2 = 0
  Occurrences = 2
  Occurrences2 = 1
  Offset = 56
  Offset2 = 10
  Reversed2 = false
  SpacingPattern = [0]
  SpacingPattern2 = [0]
  Spacings = [-1]
  Suppressed = false
  TransformMode = 0
FEATURE [PartDesign::LinearPattern] LinearPattern001
  Direction = -> Sketch021 [V_Axis]
  Length = 18
  Length2 = 100
  Mode = 0
  Mode2 = 0
  Occurrences = 2
  Occurrences2 = 1
  Offset = 18
  Offset2 = 10
  Reversed2 = false
  SpacingPattern = [0]
  SpacingPattern2 = [0]
  Spacings = [-1]
  Suppressed = false
  TransformMode = 0
FEATURE [Sketcher::SketchObject] Sketch022
  ArcFitTolerance = 0
  ExternalTypes = [0]
  FullyConstrained = true
  MakeInternals = false
  MapMode = 5
  Placement = pos=(0,0,5) rot=(0,0,1;0rad)
  sketch-geometry (4):
    g0: Circle CenterX=-15.5 CenterY=15.5 CenterZ=0 NormalX=0 NormalY=0 NormalZ=1 AngleXU=0 Radius=2
    g1: Circle CenterX=15.5 CenterY=15.5 CenterZ=0 NormalX=0 NormalY=0 NormalZ=1 AngleXU=0 Radius=2
    g2: Circle CenterX=15.5 CenterY=-15.5 CenterZ=0 NormalX=0 NormalY=0 NormalZ=1 AngleXU=0 Radius=2
    g3: Circle CenterX=-15.5 CenterY=-15.5 CenterZ=0 NormalX=0 NormalY=0 NormalZ=1 AngleXU=0 Radius=2
  constraints (9):
    c: Symmetric(g3,g0,g-1)
    c: Symmetric(g0,g1,g-2)
    c: Symmetric(g2,g1,g-1)
    c: Equal(g3,g2)
    c: Equal(g2,g1)
    c: Equal(g1,g0)
    c: DistanceX(g0,g1) = 31
    c: DistanceY(g2,g1) = 31
    c: Diameter(g1) = 4
FEATURE [Sketcher::SketchObject] Sketch023
  ArcFitTolerance = 0
  AttachmentSupport = -> [XY_Plane012]
  ExternalTypes = [0]
  FullyConstrained = true
  MakeInternals = false
  MapMode = 5
  sketch-geometry (5):
    g0: LineSegment StartX=25 StartY=25 StartZ=0 EndX=-25 EndY=25 EndZ=0
    g1: LineSegment StartX=-25 StartY=-25 StartZ=0 EndX=25 EndY=-25 EndZ=0
    g2: Circle [constr] CenterX=0 CenterY=0 CenterZ=0 NormalX=0 NormalY=0 NormalZ=1 AngleXU=0 Radius=35.3553
    g3: LineSegment StartX=-25 StartY=25 StartZ=0 EndX=-25 EndY=-25 EndZ=0
    g4: LineSegment StartX=25 StartY=25 StartZ=0 EndX=25 EndY=-25 EndZ=0
  constraints (14):
    c: Equal(g0,g1)
    c: PointOnObject(g0,g2)
    c: PointOnObject(g1,g2)
    c: PointOnObject(g1,g2)
    c: PointOnObject(g0,g2)
    c: Coincident(g2,g-1)
    c: Horizontal(g0)
    c: DistanceX(g0,g0) = 50
    c: DistanceY(g1,g0) = 50
    c: Horizontal(g1)
    c: Coincident(g0,g3)
    c: Coincident(g3,g1)
    c: Coincident(g0,g4)
    c: Coincident(g4,g1)
FEATURE [PartDesign::Pad] Pad005
  Direction = (0,0,1)
  Length = 10
  Length2 = 100
  Profile = -> Sketch023
  Refine = true
  SideType = 0
  Suppressed = false
  Type = 0
  Type2 = 0
FEATURE [Sketcher::SketchObject] Sketch024
  ArcFitTolerance = 0
  AttachmentSupport = -> [Pad005]
  ExternalTypes = [0]
  FullyConstrained = true
  MakeInternals = false
  MapMode = 5
  Placement = pos=(0,0,10) rot=(0,0,1;0rad)
  sketch-geometry (5):
    g0: LineSegment StartX=21 StartY=21 StartZ=0 EndX=-21 EndY=21 EndZ=0
    g1: LineSegment StartX=-21 StartY=21 StartZ=0 EndX=-21 EndY=-21 EndZ=0
    g2: LineSegment StartX=-21 StartY=-21 StartZ=0 EndX=21 EndY=-21 EndZ=0
    g3: LineSegment StartX=21 StartY=-21 StartZ=0 EndX=21 EndY=21 EndZ=0
    g4: Circle [constr] CenterX=0 CenterY=0 CenterZ=0 NormalX=0 NormalY=0 NormalZ=1 AngleXU=0 Radius=29.6985
  constraints (14):
    c: Coincident(g0,g1)
    c: Coincident(g1,g2)
    c: Coincident(g2,g3)
    c: Coincident(g3,g0)
    c: Equal(g0,g1)
    c: Equal(g0,g2)
    c: Equal(g0,g3)
    c: PointOnObject(g0,g4)
    c: PointOnObject(g1,g4)
    c: PointOnObject(g2,g4)
    c: PointOnObject(g3,g4)
    c: Coincident(g4,g-1)
    c: DistanceX(g0,g0) = 42
    c: Horizontal(g0)
FEATURE [PartDesign::Pocket] Pocket014
  BaseFeature = -> Pad005
  Direction = (0,0,-1)
  Length = 7
  Length2 = 100
  Profile = -> Sketch024
  Refine = true
  SideType = 0
  Suppressed = false
  Type = 0
  Type2 = 0
FEATURE [Sketcher::SketchObject] Sketch025
  ArcFitTolerance = 0
  AttachmentSupport = -> [Pocket014]
  ExternalTypes = [0]
  FullyConstrained = true
  MakeInternals = false
  MapMode = 5
  Placement = pos=(0,0,3) rot=(0,0,1;0rad)
  sketch-geometry (1):
    g0: Circle CenterX=0 CenterY=0 CenterZ=0 NormalX=0 NormalY=0 NormalZ=1 AngleXU=0 Radius=11
  constraints (2):
    c: Coincident(g0,g-1)
    c: Diameter(g0) = 22
FEATURE [PartDesign::Pocket] Pocket015
  BaseFeature = -> Pocket014
  Direction = (0,0,-1)
  Length = 5
  Length2 = 100
  Profile = -> Sketch025
  Refine = true
  SideType = 0
  Suppressed = false
  Type = 1
  Type2 = 0
FEATURE [PartDesign::Pocket] Pocket016
  BaseFeature = -> Pocket015
  Direction = (0,0,-1)
  Length = 5
  Length2 = 100
  Profile = -> Sketch022
  Refine = true
  SideType = 0
  Suppressed = false
  Type = 0
  Type2 = 0
FEATURE [Sketcher::SketchObject] Sketch026
  ArcFitTolerance = 0
  AttachmentSupport = -> [XY_Plane012]
  ExternalGeometry = -> [Pocket016]
  ExternalTypes = [0]
  FullyConstrained = true
  MakeInternals = false
  MapMode = 5
  sketch-geometry (8):
    g0: LineSegment StartX=-25 StartY=25 StartZ=0 EndX=25 EndY=25 EndZ=0
    g1: LineSegment StartX=35 StartY=-7.67949 StartZ=0 EndX=35 EndY=50 EndZ=0
    g2: LineSegment StartX=35 StartY=50 StartZ=0 EndX=-35 EndY=50 EndZ=0
    g3: LineSegment StartX=-35 StartY=50 StartZ=0 EndX=-35 EndY=-7.67949 EndZ=0
    g4: LineSegment StartX=-35 StartY=-7.67949 StartZ=0 EndX=-25 EndY=-25 EndZ=0
    g5: LineSegment StartX=-25 StartY=-25 StartZ=0 EndX=-25 EndY=25 EndZ=0
    g6: LineSegment StartX=35 StartY=-7.67949 StartZ=0 EndX=25 EndY=-25 EndZ=0
    g7: LineSegment StartX=25 StartY=-25 StartZ=0 EndX=25 EndY=25 EndZ=0
  constraints (19):
    c: Coincident(g-3,g0)
    c: Coincident(g0,g-3)
    c: Vertical(g1)
    c: Coincident(g1,g2)
    c: Coincident(g2,g3)
    c: Symmetric(g2,g1,g-2)
    c: Symmetric(g3,g1,g-2)
    c: DistanceX(g2,g2) = 70
    c: DistanceY(g1) = 50
    c: Coincident(g3,g4)
    c: Coincident(g4,g5)
    c: Coincident(g5,g0)
    c: Vertical(g5)
    c: Coincident(g1,g6)
    c: Coincident(g6,g7)
    c: Coincident(g7,g0)
    c: Symmetric(g6,g4,g-2)
    c: Angle(g1,g6) = 2.61799
    c: DistanceY(g6) = -25
FEATURE [PartDesign::Pad] Pad006
  BaseFeature = -> Pocket016
  Direction = (0,0,1)
  Length = 10
  Length2 = 100
  Profile = -> Sketch026
  Refine = true
  SideType = 0
  Suppressed = false
  Type = 0
  Type2 = 0
FEATURE [PartDesign::Pocket] Pocket017
  BaseFeature = -> Pad006
  Direction = (0,0,-1)
  Length = 5
  Length2 = 100
  Profile = -> Sketch021
  Refine = true
  Reversed = true
  SideType = 0
  Suppressed = false
  Type = 1
  Type2 = 0
FEATURE [PartDesign::MultiTransform] MultiTransform
  BaseFeature = -> Pocket017
  Originals = -> [Pocket017]
  Refine = true
  Suppressed = false
  TransformMode = 0
  Transformations = -> [LinearPattern,LinearPattern001]
FEATURE [PartDesign::Fillet] Fillet002
  Base = -> MultiTransform [Edge5,Edge1,Edge2,Edge58,Edge59,Edge8]
  BaseFeature = -> MultiTransform
  Radius = 5
  SupportTransform = true
  Suppressed = false
  UseAllEdges = false
FEATURE [PartDesign::Body] Body007  label="vertical-axis-motor-mount"
  AllowCompound = true
  Group = -> [Sketch023,Pad005,Sketch024,Pocket014,Sketch025,Pocket015,Sketch022,Pocket016,Sketch026,Pad006,Sketch021,Pocket017,MultiTransform,LinearPattern,LinearPattern001,Fillet002]
  Origin = -> Origin012
  Placement = pos=(0,0,232.808) rot=(0,0,1;0rad)
  Tip = -> Fillet002
FEATURE [App::Link] Link037  label="vertical-axis-motor-mount001"
  LinkPlacement = pos=(18.3713,-269.374,66) rot=(0,0,1;0.068094rad)
  LinkedObject = -> Body007
  Placement = pos=(18.3713,-269.374,66) rot=(0,0,1;0.068094rad)
FEATURE [Sketcher::SketchObject] Sketch027
  ArcFitTolerance = 0
  AttachmentSupport = -> [XY_Plane013]
  ExternalTypes = [0]
  FullyConstrained = true
  MakeInternals = false
  MapMode = 5
  sketch-geometry (5):
    g0: LineSegment StartX=21.15 StartY=21.15 StartZ=0 EndX=-21.15 EndY=21.15 EndZ=0
    g1: LineSegment StartX=-21.15 StartY=21.15 StartZ=0 EndX=-21.15 EndY=-21.15 EndZ=0
    g2: LineSegment StartX=-21.15 StartY=-21.15 StartZ=0 EndX=21.15 EndY=-21.15 EndZ=0
    g3: LineSegment StartX=21.15 StartY=-21.15 StartZ=0 EndX=21.15 EndY=21.15 EndZ=0
    g4: Circle [constr] CenterX=0 CenterY=0 CenterZ=0 NormalX=0 NormalY=0 NormalZ=1 AngleXU=0 Radius=29.9106
  constraints (14):
    c: Coincident(g0,g1)
    c: Coincident(g1,g2)
    c: Coincident(g2,g3)
    c: Coincident(g3,g0)
    c: Equal(g0,g1)
    c: Equal(g0,g2)
    c: Equal(g0,g3)
    c: PointOnObject(g0,g4)
    c: PointOnObject(g1,g4)
    c: PointOnObject(g2,g4)
    c: PointOnObject(g3,g4)
    c: Coincident(g4,g-1)
    c: Horizontal(g0)
    c: DistanceY(g3,g3) = 42.3
FEATURE [PartDesign::Pad] Pad007
  Direction = (0,0,1)
  Length = 40
  Length2 = 100
  Profile = -> Sketch027
  SideType = 0
  Suppressed = false
  Type = 0
  Type2 = 0
FEATURE [Sketcher::SketchObject] Sketch028
  ArcFitTolerance = 0
  AttachmentSupport = -> [Pad007]
  ExternalTypes = [0]
  FullyConstrained = true
  MakeInternals = false
  MapMode = 5
  Placement = pos=(0,0,40) rot=(0,0,1;0rad)
  sketch-geometry (1):
    g0: Circle CenterX=0 CenterY=0 CenterZ=0 NormalX=0 NormalY=0 NormalZ=1 AngleXU=0 Radius=11
  constraints (2):
    c: Coincident(g0,g-1)
    c: Diameter(g0) = 22
FEATURE [PartDesign::Pad] Pad008
  BaseFeature = -> Pad007
  Direction = (0,0,1)
  Length = 2
  Length2 = 100
  Profile = -> Sketch028
  SideType = 0
  Suppressed = false
  Type = 0
  Type2 = 0
FEATURE [Sketcher::SketchObject] Sketch029
  ArcFitTolerance = 0
  AttachmentSupport = -> [Pad008]
  ExternalTypes = [0]
  FullyConstrained = true
  MakeInternals = false
  MapMode = 5
  Placement = pos=(0,0,40) rot=(0,0,1;0rad)
  sketch-geometry (1):
    g0: Circle CenterX=0 CenterY=0 CenterZ=0 NormalX=0 NormalY=0 NormalZ=1 AngleXU=0 Radius=2.5
  constraints (2):
    c: Coincident(g0,g-1)
    c: Diameter(g0) = 5
FEATURE [PartDesign::Pad] Pad009
  BaseFeature = -> Pad008
  Direction = (0,0,1)
  Length = 24
  Length2 = 100
  Profile = -> Sketch029
  SideType = 0
  Suppressed = false
  Type = 0
  Type2 = 0
FEATURE [PartDesign::Chamfer] Chamfer004
  Angle = 45
  Base = -> Pad009 [Edge18]
  BaseFeature = -> Pad009
  ChamferType = 0
  FlipDirection = false
  Size = 0.5
  Size2 = 1
  SupportTransform = true
  Suppressed = false
  UseAllEdges = false
FEATURE [Sketcher::SketchObject] Sketch030
  ArcFitTolerance = 0
  AttachmentSupport = -> [XZ_Plane013]
  ExternalGeometry = -> [Chamfer004]
  ExternalTypes = [0]
  FullyConstrained = true
  MakeInternals = false
  MapMode = 5
  Placement = pos=(0,0,0) rot=(1,0,0;1.5708rad)
  sketch-geometry (4):
    g0: LineSegment StartX=2 StartY=64 StartZ=0 EndX=2.5 EndY=64 EndZ=0
    g1: LineSegment StartX=2.5 StartY=64 StartZ=0 EndX=2.5 EndY=43 EndZ=0
    g2: LineSegment StartX=2.5 StartY=43 StartZ=0 EndX=2 EndY=43 EndZ=0
    g3: LineSegment StartX=2 StartY=43 StartZ=0 EndX=2 EndY=64 EndZ=0
  constraints (12):
    c: Coincident(g0,g1)
    c: Coincident(g1,g2)
    c: Coincident(g2,g3)
    c: Coincident(g3,g0)
    c: Horizontal(g0)
    c: Horizontal(g2)
    c: Vertical(g1)
    c: Vertical(g3)
    c: PointOnObject(g0,g-3)
    c: PointOnObject(g1,g-4)
    c: DistanceX(g2,g2) = 0.5
    c: DistanceY(g1,g1) = 21
FEATURE [PartDesign::Pocket] Pocket018
  BaseFeature = -> Chamfer004
  Direction = (0,1,-2e-16)
  Length = 20
  Length2 = 100
  Profile = -> Sketch030
  SideType = 2
  Suppressed = false
  Type = 1
  Type2 = 0
FEATURE [Sketcher::SketchObject] Sketch031
  ArcFitTolerance = 0
  AttachmentSupport = -> [Pocket018]
  ExternalTypes = [0]
  FullyConstrained = true
  MakeInternals = false
  MapMode = 5
  Placement = pos=(0,0,40) rot=(0,0,1;0rad)
  sketch-geometry (4):
    g0: Circle CenterX=15.5 CenterY=-15.5 CenterZ=0 NormalX=0 NormalY=0 NormalZ=1 AngleXU=0 Radius=1.25
    g1: Circle CenterX=15.5 CenterY=15.5 CenterZ=0 NormalX=0 NormalY=0 NormalZ=1 AngleXU=0 Radius=1.25
    g2: Circle CenterX=-15.5 CenterY=15.5 CenterZ=0 NormalX=0 NormalY=0 NormalZ=1 AngleXU=0 Radius=1.25
    g3: Circle CenterX=-15.5 CenterY=-15.5 CenterZ=0 NormalX=0 NormalY=0 NormalZ=1 AngleXU=0 Radius=1.25
  constraints (9):
    c: Diameter(g0) = 2.5
    c: Symmetric(g1,g0,g-1)
    c: Symmetric(g1,g2,g-2)
    c: Symmetric(g3,g2,g-1)
    c: Equal(g2,g1)
    c: Equal(g1,g3)
    c: Equal(g3,g0)
    c: DistanceX(g2,g1) = 31
    c: DistanceY(g0,g1) = 31
FEATURE [PartDesign::Hole] Hole
  BaseFeature = -> Pocket018
  BaseProfileType = 6
  CustomThreadClearance = 0
  Depth = 4
  DepthType = 0
  Diameter = 1.4
  DrillForDepth = false
  DrillPoint = 1
  DrillPointAngle = 118
  HoleCutCountersinkAngle = 90
  HoleCutCustomValues = false
  HoleCutDepth = 0
  HoleCutDiameter = 1.6
  HoleCutType = 0
  ModelThread = false
  Profile = -> Sketch031
  Suppressed = false
  Tapered = false
  TaperedAngle = 90
  ThreadClass = 0
  ThreadDepth = 4
  ThreadDepthType = 0
  ThreadDiameter = 1.2
  ThreadDirection = 0
  ThreadFit = 0
  ThreadSize = 2
  ThreadType = 1
  Threaded = false
  UseCustomThreadClearance = false
FEATURE [PartDesign::Chamfer] Chamfer005
  Angle = 45
  Base = -> Hole [Edge29,Edge26,Edge31,Edge27]
  BaseFeature = -> Hole
  ChamferType = 0
  FlipDirection = false
  Size = 5
  Size2 = 1
  SupportTransform = true
  Suppressed = false
  UseAllEdges = false
FEATURE [PartDesign::Body] Body008  label="nema17"
  AllowCompound = true
  Group = -> [Sketch027,Pad007,Sketch028,Pad008,Sketch029,Pad009,Chamfer004,Sketch030,Pocket018,Sketch031,Hole,Chamfer005]
  Origin = -> Origin013
  Tip = -> Chamfer005
FEATURE [App::Link] Link038  label="nema17_001"
  LinkPlacement = pos=(18.3713,-269.374,109) rot=(0.99942,0.034041,0;3.14159rad)
  LinkedObject = -> Body008
  Placement = pos=(18.3713,-269.374,109) rot=(0.99942,0.034041,0;3.14159rad)
FEATURE [App::Link] Link039  label="vertical-axis-motor-gear001"
  LinkPlacement = pos=(18.3713,-269.374,12) rot=(0,0,-1;0.004082rad)
  LinkedObject = -> Part002
  Placement = pos=(18.3713,-269.374,12) rot=(0,0,-1;0.004082rad)
FEATURE [Sketcher::SketchObject] Sketch034
  ArcFitTolerance = 0
  AttachmentSupport = -> [XZ_Plane016]
  ExternalTypes = [0]
  FullyConstrained = true
  MakeInternals = false
  MapMode = 5
  Placement = pos=(0,0,0) rot=(1,0,0;1.5708rad)
  sketch-geometry (7):
    g0: LineSegment StartX=-170 StartY=0 StartZ=0 EndX=170 EndY=0 EndZ=0
    g1: LineSegment StartX=170 StartY=0 StartZ=0 EndX=170 EndY=380 EndZ=0
    g2: LineSegment StartX=170 StartY=380 StartZ=0 EndX=90 EndY=380 EndZ=0
    g3: LineSegment StartX=-170 StartY=380 StartZ=0 EndX=-170 EndY=0 EndZ=0
    g4: ArcOfCircle CenterX=0 CenterY=500 CenterZ=0 NormalX=0 NormalY=0 NormalZ=1 AngleXU=0 Radius=150 StartAngle=4.06889 EndAngle=5.35589
    g5: LineSegment StartX=-90 StartY=380 StartZ=0 EndX=-170 EndY=380 EndZ=0
    g6: GeomPoint [constr] X=0 Y=350 Z=0
  constraints (19):
    c: Coincident(g0,g1)
    c: Coincident(g1,g2)
    c: Coincident(g5,g3)
    c: Coincident(g3,g0)
    c: Horizontal(g0)
    c: Vertical(g1)
    c: Vertical(g3)
    c: PointOnObject(g0,g-1)
    c: Symmetric(g1,g5,g-2)
    c: DistanceY(g1,g1) = 380
    c: DistanceX(g0,g0) = 340
    c: Tangent(g2,g5)
    c: Coincident(g4,g5)
    c: Coincident(g4,g2)
    c: PointOnObject(g4,g-2)
    c: PointOnObject(g6,g-2)
    c: PointOnObject(g6,g4)
    c: DistanceY(g-1,g6) = 350
    c: DistanceX(g4,g2) = 180
FEATURE [PartDesign::Pad] Pad010
  AllowMultiFace = false
  Direction = (0,-1,-1.035e-13)
  Length = 18
  Length2 = 100
  Placement = pos=(0,0,0) rot=(1,0,0;1.5708rad)
  Profile = -> Sketch034
  SideType = 0
  Suppressed = false
  Type = 0
  Type2 = 0
FEATURE [PartDesign::Body] Body010  label="fork-rear-plate"
  AllowCompound = true
  Group = -> [Sketch034,Pad010]
  Origin = -> Origin016
  Tip = -> Pad010
FEATURE [App::Link] Link040  label="fork-rear-plate001"
  LinkPlacement = pos=(-10.2063,149.652,66) rot=(0,0,1;0.068094rad)
  LinkedObject = -> Body010
  Placement = pos=(-10.2063,149.652,66) rot=(0,0,1;0.068094rad)
FEATURE [Sketcher::SketchObject] Sketch035
  ArcFitTolerance = 0
  AttachmentSupport = -> [YZ_Plane017]
  ExternalTypes = [0]
  FullyConstrained = true
  MakeInternals = false
  MapMode = 5
  Placement = pos=(0,0,0) rot=(0.57735,0.57735,0.57735;2.0944rad)
  sketch-geometry (5):
    g0: ArcOfCircle CenterX=0 CenterY=580 CenterZ=0 NormalX=0 NormalY=0 NormalZ=1 AngleXU=0 Radius=95 StartAngle=0.495618 EndAngle=3.41262
    g1: ArcOfCircle CenterX=-765.98 CenterY=367.162 CenterZ=0 NormalX=0 NormalY=0 NormalZ=1 AngleXU=0 Radius=700 StartAngle=5.73104 EndAngle=6.55421
    g2: ArcOfCircle CenterX=-708.138 CenterY=197.162 CenterZ=0 NormalX=0 NormalY=0 NormalZ=1 AngleXU=0 Radius=900 StartAngle=6.06233 EndAngle=6.7788
    g3: LineSegment StartX=-170 StartY=-2.274e-13 StartZ=0 EndX=170 EndY=-1.705e-13 EndZ=0
    g4: Circle CenterX=0 CenterY=580 CenterZ=0 NormalX=0 NormalY=0 NormalZ=1 AngleXU=0 Radius=6
  constraints (16):
    c: PointOnObject(g0,g-2)
    c: Radius(g0) = 95
    c: DistanceY(g-1,g0) = 580
    c: PointOnObject(g1,g-1)
    c: PointOnObject(g2,g-1)
    c: Tangent(g2,g0)
    c: Coincident(g3,g1)
    c: Coincident(g3,g2)
    c: DistanceX(g3,g3) = 340
    c: DistanceX(g1,g-1) = 170
    c: Radius(g1) = 700
    c: Radius(g2) = 900
    c: Coincident(g0,g2)
    c: Tangent(g0,g1) = 1.5708
    c: Coincident(g4,g0)
    c: Radius(g4) = 6
FEATURE [PartDesign::Pad] Pad011
  AllowMultiFace = false
  Direction = (1,-1.128e-13,1.13e-13)
  Length = 18
  Length2 = 100
  Placement = pos=(0,0,0) rot=(0.57735,0.57735,0.57735;2.0944rad)
  Profile = -> Sketch035
  SideType = 2
  Suppressed = false
  Type = 0
  Type2 = 0
FEATURE [Sketcher::SketchObject] Sketch036
  ArcFitTolerance = 0
  AttachmentSupport = -> [Pad011]
  ExternalGeometry = -> [Pad011]
  ExternalTypes = [0]
  FullyConstrained = true
  MakeInternals = false
  MapMode = 5
  Placement = pos=(9,-1.0152e-12,1.0172e-12) rot=(0.57735,0.57735,0.57735;2.0944rad)
  sketch-geometry (5):
    g0: Circle [constr] CenterX=0 CenterY=580 CenterZ=0 NormalX=0 NormalY=0 NormalZ=1 AngleXU=0 Radius=75
    g1: LineSegment [constr] StartX=0 StartY=580 StartZ=0 EndX=-53.033 EndY=526.967 EndZ=0
    g2: LineSegment [constr] StartX=0 StartY=580 StartZ=0 EndX=53.033 EndY=526.967 EndZ=0
    g3: Circle CenterX=-53.033 CenterY=526.967 CenterZ=0 NormalX=0 NormalY=0 NormalZ=1 AngleXU=0 Radius=3
    g4: Circle CenterX=53.033 CenterY=526.967 CenterZ=0 NormalX=0 NormalY=0 NormalZ=1 AngleXU=0 Radius=3
  constraints (12):
    c: Coincident(g0,g-3)
    c: Coincident(g1,g0)
    c: PointOnObject(g1,g0)
    c: Coincident(g2,g0)
    c: PointOnObject(g2,g0)
    c: Angle(g1,g2) = 1.5708
    c: Angle(g1) = -2.35619
    c: Radius(g0) = 75
    c: Coincident(g3,g1)
    c: Coincident(g4,g2)
    c: Equal(g4,g3)
    c: Radius(g4) = 3
FEATURE [PartDesign::Pocket] Pocket020
  AllowMultiFace = false
  BaseFeature = -> Pad011
  Direction = (-1,1.125e-13,-1.129e-13)
  Length = 5
  Length2 = 100
  Placement = pos=(0,0,0) rot=(0.57735,0.57735,0.57735;2.0944rad)
  Profile = -> Sketch036
  SideType = 0
  Suppressed = false
  Type = 1
  Type2 = 0
FEATURE [PartDesign::Line] DatumLine
  AttacherType = Attacher::AttachEngineLine
  AttachmentSupport = -> [Pocket020]
  Length = 18
  MapMode = 19
  Placement = pos=(9,6.45244e-11,580) rot=(0.57735,0.57735,0.57735;2.0944rad)
  ResizeMode = 0
FEATURE [Sketcher::SketchObject] Sketch037
  ArcFitTolerance = 0
  AttachmentSupport = -> [Pocket020]
  ExternalGeometry = -> [Pocket020]
  ExternalTypes = [0]
  FullyConstrained = true
  MakeInternals = false
  MapMode = 5
  Placement = pos=(9,-1.0152e-12,1.0172e-12) rot=(0.57735,0.57735,0.57735;2.0944rad)
  sketch-geometry (1):
    g0: LineSegment StartX=2.416e-13 StartY=580 StartZ=0 EndX=0 EndY=0 EndZ=0
  constraints (2):
    c: Coincident(g0,g-3)
    c: Coincident(g0,g-1)
FEATURE [PartDesign::Body] Body011  label="fork-side-plate"
  AllowCompound = true
  Group = -> [Sketch035,Pad011,Sketch036,Pocket020,DatumLine,Sketch037]
  Origin = -> Origin017
  Tip = -> Pocket020
FEATURE [App::Link] Link041  label="fork-side-plate001"
  LinkPlacement = pos=(178.585,12.1795,66) rot=(0,0,1;0.068094rad)
  LinkedObject = -> Body011
  Placement = pos=(178.585,12.1795,66) rot=(0,0,1;0.068094rad)
FEATURE [App::Link] Link042  label="fork-side-plate002"
  LinkPlacement = pos=(-178.585,-12.1795,66) rot=(0,0,1;0.068094rad)
  LinkedObject = -> Body011
  Placement = pos=(-178.585,-12.1795,66) rot=(0,0,1;0.068094rad)
FEATURE [Sketcher::SketchObject] Sketch051
  ArcFitTolerance = 0
  AttachmentSupport = -> [XZ_Plane020]
  ExternalTypes = [0]
  FullyConstrained = true
  MakeInternals = false
  MapMode = 5
  Placement = pos=(0,0,0) rot=(1,0,0;1.5708rad)
  sketch-geometry (2):
    g0: Circle CenterX=0 CenterY=-135 CenterZ=0 NormalX=0 NormalY=0 NormalZ=1 AngleXU=0 Radius=145
    g1: GeomPoint [constr] X=0 Y=10 Z=0
  constraints (5):
    c: PointOnObject(g0,g-2)
    c: PointOnObject(g1,g0)
    c: PointOnObject(g1,g-2)
    c: DistanceY(g-1,g1) = 10
    c: Diameter(g0) = 290
FEATURE [Sketcher::SketchObject] Sketch052
  ArcFitTolerance = 0
  AttachmentSupport = -> [XY_Plane020]
  ExternalTypes = [0]
  FullyConstrained = true
  MakeInternals = false
  MapMode = 5
  sketch-geometry (4):
    g0: LineSegment StartX=-150 StartY=-20 StartZ=0 EndX=150 EndY=-20 EndZ=0
    g1: LineSegment StartX=150 StartY=-20 StartZ=0 EndX=150 EndY=-170 EndZ=0
    g2: LineSegment StartX=150 StartY=-170 StartZ=0 EndX=-150 EndY=-170 EndZ=0
    g3: LineSegment StartX=-150 StartY=-170 StartZ=0 EndX=-150 EndY=-20 EndZ=0
  constraints (11):
    c: Coincident(g0,g1)
    c: Coincident(g1,g2)
    c: Coincident(g2,g3)
    c: Coincident(g3,g0)
    c: Horizontal(g2)
    c: Vertical(g1)
    c: Vertical(g3)
    c: DistanceY(g0,g-1) = 20
    c: Symmetric(g0,g0,g-2)
    c: DistanceX(g2,g2) = 300
    c: DistanceY(g1,g1) = 150
FEATURE [PartDesign::Plane] DatumPlane003
  AttachmentOffset = pos=(0,0,5) rot=(0,0,1;0rad)
  AttachmentSupport = -> [XY_Plane020]
  Length = 249.689
  MapMode = 5
  Placement = pos=(0,0,5) rot=(0,0,1;0rad)
  ResizeMode = 0
  Width = 194.689
FEATURE [Sketcher::SketchObject] Sketch053
  ArcFitTolerance = 0
  AttachmentSupport = -> [DatumPlane003]
  ExternalTypes = [0]
  FullyConstrained = true
  MakeInternals = false
  MapMode = 5
  Placement = pos=(0,0,5) rot=(0,0,1;0rad)
  sketch-geometry (6):
    g0: LineSegment StartX=80 StartY=0 StartZ=0 EndX=80 EndY=2 EndZ=0
    g1: LineSegment StartX=80 StartY=2 StartZ=0 EndX=98 EndY=2 EndZ=0
    g2: LineSegment StartX=98 StartY=2 StartZ=0 EndX=98 EndY=3.5 EndZ=0
    g3: LineSegment StartX=98 StartY=3.5 StartZ=0 EndX=140 EndY=3.5 EndZ=0
    g4: LineSegment StartX=140 StartY=3.5 StartZ=0 EndX=140 EndY=0 EndZ=0
    g5: LineSegment StartX=140 StartY=0 StartZ=0 EndX=80 EndY=0 EndZ=0
  constraints (18):
    c: PointOnObject(g0,g-1)
    c: Vertical(g0)
    c: Coincident(g0,g1)
    c: Horizontal(g1)
    c: Coincident(g1,g2)
    c: Coincident(g2,g3)
    c: Horizontal(g3)
    c: Coincident(g3,g4)
    c: PointOnObject(g4,g-1)
    c: Vertical(g4)
    c: Coincident(g4,g5)
    c: Coincident(g5,g0)
    c: DistanceX(g0) = 80
    c: DistanceX(g1,g1) = 18
    c: Vertical(g2)
    c: DistanceY(g0,g0) = 2
    c: DistanceY(g4,g4) = 3.5
    c: DistanceX(g5,g5) = 60
FEATURE [PartDesign::PolarPattern] PolarPattern004
  Angle = 45
  Axis = -> Z_Axis020
  Mode = 0
  Occurrences = 3
  Offset = 120
  SpacingPattern = [0]
  Spacings = [-1,-1]
  Suppressed = false
  TransformMode = 0
FEATURE [PartDesign::Mirrored] Mirrored
  MirrorPlane = -> YZ_Plane020
  Suppressed = false
  TransformMode = 0
FEATURE [Sketcher::SketchObject] Sketch054
  ArcFitTolerance = 0
  AttachmentSupport = -> [XY_Plane020]
  ExternalTypes = [0]
  FullyConstrained = true
  MakeInternals = false
  MapMode = 5
  sketch-geometry (4):
    g0: LineSegment StartX=160 StartY=150 StartZ=0 EndX=10 EndY=0 EndZ=0
    g1: LineSegment StartX=10 StartY=0 StartZ=0 EndX=10 EndY=-30 EndZ=0
    g2: LineSegment StartX=10 StartY=-30 StartZ=0 EndX=160 EndY=-30 EndZ=0
    g3: LineSegment StartX=160 StartY=-30 StartZ=0 EndX=160 EndY=150 EndZ=0
  constraints (12):
    c: PointOnObject(g0,g-1)
    c: Coincident(g0,g1)
    c: Vertical(g1)
    c: Coincident(g1,g2)
    c: Horizontal(g2)
    c: Coincident(g2,g3)
    c: Coincident(g3,g0)
    c: Angle(g-1,g0) = 0.785398
    c: DistanceX(g0) = 10
    c: Vertical(g3)
    c: DistanceY(g2) = -30
    c: DistanceX(g2,g2) = 150
FEATURE [Sketcher::SketchObject] Sketch055
  ArcFitTolerance = 0
  AttachmentSupport = -> [XY_Plane020]
  ExternalTypes = [0]
  FullyConstrained = true
  MakeInternals = false
  MapMode = 5
  sketch-geometry (5):
    g0: LineSegment StartX=-92 StartY=8 StartZ=0 EndX=-97 EndY=8 EndZ=0
    g1: ArcOfCircle CenterX=0 CenterY=0 CenterZ=0 NormalX=0 NormalY=0 NormalZ=1 AngleXU=0 Radius=92.3472 StartAngle=2.82743 EndAngle=3.05485
    g2: ArcOfCircle CenterX=0 CenterY=0 CenterZ=0 NormalX=0 NormalY=0 NormalZ=1 AngleXU=0 Radius=97.3293 StartAngle=2.82743 EndAngle=3.0593
    g3: LineSegment StartX=-92.5657 StartY=30.0764 StartZ=0 EndX=-87.8274 EndY=28.5368 EndZ=0
    g4: LineSegment [constr] StartX=-87.8274 StartY=28.5368 StartZ=0 EndX=0 EndY=0 EndZ=0
  constraints (14):
    c: Horizontal(g0)
    c: Coincident(g1,g-1)
    c: Coincident(g1,g0)
    c: Coincident(g2,g1)
    c: Coincident(g2,g0)
    c: Coincident(g3,g2)
    c: Coincident(g3,g1)
    c: DistanceX(g0) = -92
    c: DistanceY(g0) = 8
    c: DistanceX(g0,g0) = 5
    c: Angle(g3,g0) = 0.314159
    c: Coincident(g4,g1)
    c: Coincident(g4,g1)
    c: Parallel(g4,g3)
FEATURE [Sketcher::SketchObject] Sketch056
  ArcFitTolerance = 0
  AttachmentSupport = -> [XY_Plane020]
  ExternalTypes = [0]
  FullyConstrained = true
  MakeInternals = false
  MapMode = 5
  sketch-geometry (2):
    g0: Circle CenterX=0 CenterY=0 CenterZ=0 NormalX=0 NormalY=0 NormalZ=1 AngleXU=0 Radius=100
    g1: Circle CenterX=0 CenterY=0 CenterZ=0 NormalX=0 NormalY=0 NormalZ=1 AngleXU=0 Radius=150
  constraints (4):
    c: Coincident(g0,g-1)
    c: Coincident(g1,g0)
    c: Diameter(g0) = 200
    c: Diameter(g1) = 300
FEATURE [Sketcher::SketchObject] Sketch057
  ArcFitTolerance = 0
  AttachmentSupport = -> [XY_Plane020]
  ExternalTypes = [0]
  FullyConstrained = true
  MakeInternals = false
  MapMode = 5
  sketch-geometry (1):
    g0: Circle CenterX=-115 CenterY=0 CenterZ=0 NormalX=0 NormalY=0 NormalZ=1 AngleXU=0 Radius=11
  constraints (3):
    c: PointOnObject(g0,g-1)
    c: DistanceX(g0) = -115
    c: Diameter(g0) = 22
FEATURE [Sketcher::SketchObject] Sketch058
  ArcFitTolerance = 0
  AttachmentSupport = -> [XY_Plane020]
  ExternalTypes = [0]
  FullyConstrained = true
  MakeInternals = false
  MapMode = 5
  sketch-geometry (4):
    g0: LineSegment StartX=80 StartY=120 StartZ=0 EndX=160 EndY=120 EndZ=0
    g1: LineSegment StartX=160 StartY=120 StartZ=0 EndX=160 EndY=0 EndZ=0
    g2: LineSegment StartX=160 StartY=0 StartZ=0 EndX=80 EndY=0 EndZ=0
    g3: LineSegment StartX=80 StartY=0 StartZ=0 EndX=80 EndY=120 EndZ=0
  constraints (12):
    c: Coincident(g0,g1)
    c: Coincident(g1,g2)
    c: Coincident(g2,g3)
    c: Coincident(g3,g0)
    c: Horizontal(g0)
    c: Horizontal(g2)
    c: Vertical(g1)
    c: Vertical(g3)
    c: PointOnObject(g1,g-1)
    c: DistanceX(g2) = 80
    c: DistanceY(g1,g1) = 120
    c: DistanceX(g2,g2) = 80
FEATURE [Sketcher::SketchObject] Sketch059
  ArcFitTolerance = 0
  AttachmentSupport = -> [XY_Plane023]
  ExternalTypes = [0]
  FullyConstrained = true
  MakeInternals = false
  MapMode = 5
  sketch-geometry (2):
    g0: Circle CenterX=0 CenterY=0 CenterZ=0 NormalX=0 NormalY=0 NormalZ=1 AngleXU=0 Radius=140
    g1: Circle CenterX=0 CenterY=0 CenterZ=0 NormalX=0 NormalY=0 NormalZ=1 AngleXU=0 Radius=143
  constraints (4):
    c: Coincident(g0,g-1)
    c: Coincident(g1,g0)
    c: Radius(g1) = 143
    c: Radius(g0) = 140
FEATURE [PartDesign::Pad] Pad020
  AllowMultiFace = false
  Direction = (0,0,1)
  Length = 1120
  Length2 = 100
  Profile = -> Sketch059
  SideType = 0
  Suppressed = false
  Type = 0
  Type2 = 0
FEATURE [PartDesign::Plane] DatumPlane004
  AttachmentOffset = pos=(0,0,-20) rot=(0,0,1;0rad)
  AttachmentSupport = -> [Pad020]
  Length = 404.321
  MapMode = 5
  Placement = pos=(0,0,20) rot=(1,0,0;3.14159rad)
  ResizeMode = 0
  Width = 346.236
FEATURE [Sketcher::SketchObject] Sketch060
  ArcFitTolerance = 0
  AttachmentSupport = -> [DatumPlane004]
  ExternalGeometry = -> [Pad020]
  ExternalTypes = [0]
  FullyConstrained = true
  MakeInternals = false
  MapMode = 5
  Placement = pos=(0,0,20) rot=(1,0,0;3.14159rad)
  sketch-geometry (2):
    g0: Circle CenterX=0 CenterY=0 CenterZ=0 NormalX=0 NormalY=0 NormalZ=1 AngleXU=0 Radius=140
    g1: Circle CenterX=0 CenterY=0 CenterZ=0 NormalX=0 NormalY=0 NormalZ=1 AngleXU=0 Radius=103
  constraints (4):
    c: Coincident(g0,g-1)
    c: Coincident(g1,g0)
    c: Equal(g-3,g0)
    c: Radius(g1) = 103
FEATURE [PartDesign::Pad] Pad021
  AllowMultiFace = false
  BaseFeature = -> Pad020
  Direction = (0,0,-1)
  Length = 10
  Length2 = 100
  Profile = -> Sketch060
  Reversed = true
  SideType = 0
  Suppressed = false
  Type = 0
  Type2 = 0
FEATURE [PartDesign::Plane] DatumPlane005
  AttachmentOffset = pos=(0,0,150) rot=(0,0,1;0rad)
  AttachmentSupport = -> [YZ_Plane023]
  Length = 397.947
  MapMode = 5
  Placement = pos=(150,-1.69198e-11,1.69531e-11) rot=(0.57735,0.57735,0.57735;2.0944rad)
  ResizeMode = 0
  Width = 1259.03
FEATURE [Sketcher::SketchObject] Sketch061
  ArcFitTolerance = 0
  AttachmentSupport = -> [DatumPlane005]
  ExternalTypes = [0]
  FullyConstrained = true
  MakeInternals = false
  MapMode = 5
  Placement = pos=(150,-1.69198e-11,1.69531e-11) rot=(0.57735,0.57735,0.57735;2.0944rad)
  sketch-geometry (1):
    g0: Circle CenterX=0 CenterY=420 CenterZ=0 NormalX=0 NormalY=0 NormalZ=1 AngleXU=0 Radius=90
  constraints (3):
    c: PointOnObject(g0,g-2)
    c: DistanceY(g0) = 420
    c: Radius(g0) = 90
FEATURE [PartDesign::Pad] Pad022
  AllowMultiFace = false
  BaseFeature = -> Pad021
  Direction = (1,0,0)
  Length = 23
  Length2 = 100
  Profile = -> Sketch061
  ReferenceAxis = -> Sketch061 [N_Axis]
  Reversed = true
  SideType = 0
  Suppressed = false
  Type = 2
  Type2 = 0
FEATURE [Sketcher::SketchObject] Sketch062
  ArcFitTolerance = 0
  AttachmentSupport = -> [Pad022]
  ExternalTypes = [0]
  FullyConstrained = true
  MakeInternals = false
  MapMode = 5
  Placement = pos=(150,-1.6926e-11,1.6956e-11) rot=(0.57735,0.57735,0.57735;2.0944rad)
  sketch-geometry (1):
    g0: Circle CenterX=0 CenterY=420 CenterZ=0 NormalX=0 NormalY=0 NormalZ=1 AngleXU=0 Radius=65
  constraints (2):
    c: Coincident(g0,g-3)
    c: Radius(g0) = 65
FEATURE [PartDesign::Pad] Pad023
  AllowMultiFace = false
  BaseFeature = -> Pad022
  Direction = (1,-1.127e-13,1.129e-13)
  Length = 20
  Length2 = 100
  Profile = -> Sketch062
  SideType = 0
  Suppressed = false
  Type = 0
  Type2 = 0
FEATURE [Sketcher::SketchObject] Sketch063
  ArcFitTolerance = 0
  AttachmentSupport = -> [Pad023]
  ExternalGeometry = -> [Pad023]
  ExternalTypes = [0]
  FullyConstrained = true
  MakeInternals = false
  MapMode = 5
  Placement = pos=(170,-1.91539e-11,1.91845e-11) rot=(0.57735,0.57735,0.57735;2.0944rad)
  sketch-geometry (2):
    g0: Circle CenterX=0 CenterY=420 CenterZ=0 NormalX=0 NormalY=0 NormalZ=1 AngleXU=0 Radius=32
    g1: Circle CenterX=0 CenterY=420 CenterZ=0 NormalX=0 NormalY=0 NormalZ=1 AngleXU=0 Radius=25
  constraints (4):
    c: Coincident(g0,g-3)
    c: Radius(g0) = 32
    c: Coincident(g1,g0)
    c: Radius(g1) = 25
FEATURE [PartDesign::Pad] Pad024
  AllowMultiFace = false
  BaseFeature = -> Pad023
  Direction = (1,-1.126e-13,1.13e-13)
  Length = 1
  Length2 = 100
  Profile = -> Sketch063
  SideType = 0
  Suppressed = false
  Type = 0
  Type2 = 0
FEATURE [PartDesign::Plane] DatumPlane006
  AttachmentOffset = pos=(0,0,-150) rot=(0,0,1;0rad)
  AttachmentSupport = -> [YZ_Plane023]
  Length = 397.947
  MapMode = 5
  Placement = pos=(-150,1.69198e-11,-1.69531e-11) rot=(0.57735,0.57735,0.57735;2.0944rad)
  ResizeMode = 0
  Width = 1259.03
FEATURE [Sketcher::SketchObject] Sketch064
  ArcFitTolerance = 0
  AttachmentSupport = -> [DatumPlane006]
  ExternalGeometry = -> [Pad024]
  ExternalTypes = [0]
  FullyConstrained = true
  MakeInternals = false
  MapMode = 5
  Placement = pos=(-150,1.69198e-11,-1.69531e-11) rot=(0.57735,0.57735,0.57735;2.0944rad)
  sketch-geometry (1):
    g0: Circle CenterX=0 CenterY=420 CenterZ=0 NormalX=0 NormalY=0 NormalZ=1 AngleXU=0 Radius=90
  constraints (2):
    c: Coincident(g0,g-3)
    c: Equal(g0,g-3)
FEATURE [PartDesign::Pad] Pad025
  AllowMultiFace = false
  BaseFeature = -> Pad024
  Direction = (1,-1.128e-13,1.13e-13)
  Length = 10
  Length2 = 100
  Profile = -> Sketch064
  SideType = 0
  Suppressed = false
  Type = 3
  Type2 = 0
  UpToFace = -> Pad024 [Face1]
FEATURE [Sketcher::SketchObject] Sketch065
  ArcFitTolerance = 0
  AttachmentSupport = -> [Pad025]
  ExternalGeometry = -> [Pad025]
  ExternalTypes = [0]
  FullyConstrained = true
  MakeInternals = false
  MapMode = 5
  Placement = pos=(-150,1.6926e-11,-1.6956e-11) rot=(-0.57735,0.57735,0.57735;4.18879rad)
  sketch-geometry (1):
    g0: Circle CenterX=0 CenterY=420 CenterZ=0 NormalX=0 NormalY=0 NormalZ=1 AngleXU=0 Radius=65
  constraints (2):
    c: Coincident(g0,g-3)
    c: Equal(g-4,g0)
FEATURE [PartDesign::Pad] Pad026
  AllowMultiFace = false
  BaseFeature = -> Pad025
  Direction = (-1,1.127e-13,-1.129e-13)
  Length = 20
  Length2 = 100
  Profile = -> Sketch065
  SideType = 0
  Suppressed = false
  Type = 0
  Type2 = 0
FEATURE [Sketcher::SketchObject] Sketch066
  ArcFitTolerance = 0
  AttachmentSupport = -> [Pad026]
  ExternalGeometry = -> [Pad026]
  ExternalTypes = [0]
  FullyConstrained = true
  MakeInternals = false
  MapMode = 5
  Placement = pos=(-170,1.91539e-11,-1.91845e-11) rot=(-0.57735,0.57735,0.57735;4.18879rad)
  sketch-geometry (2):
    g0: Circle CenterX=0 CenterY=420 CenterZ=0 NormalX=0 NormalY=0 NormalZ=1 AngleXU=0 Radius=25
    g1: Circle CenterX=0 CenterY=420 CenterZ=0 NormalX=0 NormalY=0 NormalZ=1 AngleXU=0 Radius=32
  constraints (4):
    c: Coincident(g0,g-4)
    c: Coincident(g1,g0)
    c: Equal(g1,g-3)
    c: Equal(g0,g-4)
FEATURE [PartDesign::Pad] Pad027
  AllowMultiFace = false
  BaseFeature = -> Pad026
  Direction = (-1,1.126e-13,-1.13e-13)
  Length = 1
  Length2 = 100
  Profile = -> Sketch066
  SideType = 0
  Suppressed = false
  Type = 0
  Type2 = 0
FEATURE [Sketcher::SketchObject] Sketch067
  ArcFitTolerance = 0
  AttachmentSupport = -> [Pad027]
  ExternalGeometry = -> [Pad027]
  ExternalTypes = [0]
  FullyConstrained = true
  MakeInternals = false
  MapMode = 5
  Placement = pos=(170,-1.91539e-11,1.91845e-11) rot=(0.57735,0.57735,0.57735;2.0944rad)
  sketch-geometry (1):
    g0: Circle CenterX=0 CenterY=420 CenterZ=0 NormalX=0 NormalY=0 NormalZ=1 AngleXU=0 Radius=5.25
  constraints (2):
    c: Coincident(g0,g-3)
    c: Radius(g0) = 5.25
FEATURE [PartDesign::Pocket] Pocket033
  AllowMultiFace = false
  BaseFeature = -> Pad027
  Direction = (-1,1.126e-13,-1.13e-13)
  Length = 7
  Length2 = 100
  Profile = -> Sketch067
  SideType = 0
  Suppressed = false
  Type = 0
  Type2 = 0
FEATURE [Sketcher::SketchObject] Sketch068
  ArcFitTolerance = 0
  AttachmentSupport = -> [Pocket033]
  ExternalGeometry = -> [Pocket033]
  ExternalTypes = [0]
  FullyConstrained = true
  MakeInternals = false
  MapMode = 5
  Placement = pos=(163,-1.85315e-11,1.8851e-11) rot=(0.57735,0.57735,0.57735;2.0944rad)
  sketch-geometry (1):
    g0: Circle CenterX=0 CenterY=420 CenterZ=0 NormalX=0 NormalY=0 NormalZ=1 AngleXU=0 Radius=4.25
  constraints (2):
    c: Coincident(g0,g-3)
    c: Radius(g0) = 4.25
FEATURE [PartDesign::Pocket] Pocket034
  AllowMultiFace = false
  BaseFeature = -> Pocket033
  Direction = (-1,1.136e-13,-1.156e-13)
  Length = 15
  Length2 = 100
  Profile = -> Sketch068
  SideType = 0
  Suppressed = false
  Type = 0
  Type2 = 0
FEATURE [Sketcher::SketchObject] Sketch069
  ArcFitTolerance = 0
  AttachmentSupport = -> [Pocket034]
  ExternalGeometry = -> [Pocket034]
  ExternalTypes = [0]
  FullyConstrained = true
  MakeInternals = false
  MapMode = 5
  Placement = pos=(-170,1.91539e-11,-1.91845e-11) rot=(-0.57735,0.57735,0.57735;4.18879rad)
  sketch-geometry (1):
    g0: Circle CenterX=0 CenterY=420 CenterZ=0 NormalX=0 NormalY=0 NormalZ=1 AngleXU=0 Radius=5.25
  constraints (2):
    c: Coincident(g0,g-3)
    c: Radius(g0) = 5.25
FEATURE [PartDesign::Pocket] Pocket035
  AllowMultiFace = false
  BaseFeature = -> Pocket034
  Direction = (1,-1.126e-13,1.13e-13)
  Length = 7
  Length2 = 100
  Profile = -> Sketch069
  SideType = 0
  Suppressed = false
  Type = 0
  Type2 = 0
FEATURE [Sketcher::SketchObject] Sketch070
  ArcFitTolerance = 0
  AttachmentSupport = -> [Pocket035]
  ExternalGeometry = -> [Pocket035]
  ExternalTypes = [0]
  FullyConstrained = true
  MakeInternals = false
  MapMode = 5
  Placement = pos=(-163,1.82364e-11,-1.83408e-11) rot=(-0.57735,0.57735,0.57735;4.18879rad)
  sketch-geometry (1):
    g0: Circle CenterX=0 CenterY=420 CenterZ=0 NormalX=0 NormalY=0 NormalZ=1 AngleXU=0 Radius=4.25
  constraints (2):
    c: Coincident(g0,g-3)
    c: Radius(g0) = 4.25
FEATURE [PartDesign::Pocket] Pocket036
  AllowMultiFace = false
  BaseFeature = -> Pocket035
  Direction = (1,-1.118e-13,1.125e-13)
  Length = 15
  Length2 = 100
  Profile = -> Sketch070
  SideType = 0
  Suppressed = false
  Type = 0
  Type2 = 0
FEATURE [PartDesign::Body] Body014  label="tube-main"
  AllowCompound = true
  Group = -> [Sketch059,Pad020,DatumPlane004,Sketch060,Pad021,DatumPlane005,Sketch061,Pad022,Sketch062,Pad023,Sketch063,Pad024,DatumPlane006,Sketch064,Pad025,Sketch065,Pad026,Sketch066,Pad027,Sketch067,Pocket033,Sketch068,Pocket034,Sketch069,Pocket035,Sketch070,Pocket036]
  Origin = -> Origin023
  Tip = -> Pocket036
FEATURE [App::Link] Link043  label="tube-main001"
  LinkedObject = -> Body014
FEATURE [App::Link] Link044  label="tube-main-gear001"
  LinkPlacement = pos=(-133,6.25091e-11,420) rot=(-0.57735,0.57735,0.57735;4.18879rad)
  LinkedObject = -> Part003
  Placement = pos=(-133,6.25091e-11,420) rot=(-0.57735,0.57735,0.57735;4.18879rad)
FEATURE [Sketcher::SketchObject] Sketch071
  ArcFitTolerance = 0
  AttachmentSupport = -> [XY_Plane024]
  ExternalTypes = [0]
  FullyConstrained = true
  MakeInternals = false
  MapMode = 5
  sketch-geometry (7):
    g0: LineSegment StartX=-65 StartY=-80 StartZ=0 EndX=37 EndY=-80 EndZ=0
    g1: LineSegment StartX=37 StartY=-80 StartZ=0 EndX=37 EndY=25 EndZ=0
    g2: LineSegment StartX=37 StartY=25 StartZ=0 EndX=-65 EndY=25 EndZ=0
    g3: LineSegment StartX=-65 StartY=25 StartZ=0 EndX=-65 EndY=-80 EndZ=0
    g4: Circle CenterX=2 CenterY=0 CenterZ=0 NormalX=0 NormalY=0 NormalZ=1 AngleXU=0 Radius=11
    g5: Circle CenterX=-40 CenterY=-4e-15 CenterZ=0 NormalX=0 NormalY=0 NormalZ=1 AngleXU=0 Radius=13.5
    g6: LineSegment [constr] StartX=2 StartY=0 StartZ=0 EndX=-40 EndY=-4e-15 EndZ=0
  constraints (20):
    c: Coincident(g0,g1)
    c: Coincident(g1,g2)
    c: Coincident(g2,g3)
    c: Coincident(g3,g0)
    c: Horizontal(g0)
    c: Horizontal(g2)
    c: Vertical(g1)
    c: Vertical(g3)
    c: DistanceX(g0) = -65
    c: DistanceY(g0) = -80
    c: DistanceY(g3,g3) = 105
    c: DistanceX(g2,g2) = 102
    c: Diameter(g4) = 22
    c: Coincident(g6,g4)
    c: Coincident(g6,g5)
    c: Diameter(g5) = 27
    c: Angle(g-1,g6) = 3.14159
    c: DistanceX(g5) = -40
    c: DistanceX(g4) = 2
    c: PointOnObject(g4,g-1)
FEATURE [PartDesign::Pad] Pad028
  Direction = (0,0,1)
  Length = 20
  Length2 = 100
  Profile = -> Sketch071
  SideType = 0
  Suppressed = false
  Type = 0
  Type2 = 0
FEATURE [Sketcher::SketchObject] Sketch072
  ArcFitTolerance = 0
  AttachmentSupport = -> [Pad028]
  ExternalGeometry = -> [Pad028]
  ExternalTypes = [0]
  FullyConstrained = true
  MakeInternals = false
  MapMode = 5
  Placement = pos=(0,0,20) rot=(0,0,1;0rad)
  sketch-geometry (4):
    g0: LineSegment StartX=37 StartY=-80 StartZ=0 EndX=-65 EndY=-80 EndZ=0
    g1: LineSegment StartX=-65 StartY=-80 StartZ=0 EndX=-65 EndY=-25 EndZ=0
    g2: LineSegment StartX=-65 StartY=-25 StartZ=0 EndX=37 EndY=-25 EndZ=0
    g3: LineSegment StartX=37 StartY=-25 StartZ=0 EndX=37 EndY=-80 EndZ=0
  constraints (11):
    c: Coincident(g0,g1)
    c: Coincident(g1,g2)
    c: Coincident(g2,g3)
    c: Coincident(g3,g0)
    c: Horizontal(g0)
    c: Horizontal(g2)
    c: Vertical(g1)
    c: Vertical(g3)
    c: Coincident(g0,g-3)
    c: PointOnObject(g1,g-4)
    c: DistanceY(g2) = -25
FEATURE [PartDesign::Pocket] Pocket037
  BaseFeature = -> Pad028
  Direction = (0,0,-1)
  Length = 10
  Length2 = 100
  Profile = -> Sketch072
  SideType = 0
  Suppressed = false
  Type = 0
  Type2 = 0
FEATURE [Sketcher::SketchObject] Sketch073
  ArcFitTolerance = 0
  AttachmentSupport = -> [Pocket037]
  ExternalTypes = [0]
  FullyConstrained = true
  MakeInternals = false
  MapMode = 5
  Placement = pos=(0,0,0) rot=(1,0,0;3.14159rad)
  sketch-geometry (5):
    g0: LineSegment StartX=23 StartY=21 StartZ=0 EndX=-19 EndY=21 EndZ=0
    g1: LineSegment StartX=-19 StartY=21 StartZ=0 EndX=-19 EndY=-21 EndZ=0
    g2: LineSegment StartX=-19 StartY=-21 StartZ=0 EndX=23 EndY=-21 EndZ=0
    g3: LineSegment StartX=23 StartY=-21 StartZ=0 EndX=23 EndY=21 EndZ=0
    g4: Circle [constr] CenterX=2 CenterY=0 CenterZ=0 NormalX=0 NormalY=0 NormalZ=1 AngleXU=0 Radius=29.6985
  constraints (15):
    c: Coincident(g0,g1)
    c: Coincident(g1,g2)
    c: Coincident(g2,g3)
    c: Coincident(g3,g0)
    c: Equal(g0,g1)
    c: Equal(g0,g2)
    c: Equal(g0,g3)
    c: PointOnObject(g0,g4)
    c: PointOnObject(g1,g4)
    c: PointOnObject(g2,g4)
    c: PointOnObject(g3,g4)
    c: Horizontal(g0)
    c: DistanceX(g0,g0) = 42
    c: PointOnObject(g4,g-1)
    c: DistanceX(g-1,g4) = 2
FEATURE [PartDesign::Pocket] Pocket038
  BaseFeature = -> Pocket037
  Direction = (0,0,1)
  Length = 16
  Length2 = 100
  Profile = -> Sketch073
  SideType = 0
  Suppressed = false
  Type = 0
  Type2 = 0
FEATURE [Sketcher::SketchObject] Sketch074
  ArcFitTolerance = 0
  AttachmentSupport = -> [Pocket038]
  ExternalTypes = [0]
  FullyConstrained = true
  MakeInternals = false
  MapMode = 5
  Placement = pos=(0,0,0) rot=(1,0,0;3.14159rad)
  sketch-geometry (4):
    g0: ArcOfCircle CenterX=28 CenterY=35 CenterZ=0 NormalX=0 NormalY=0 NormalZ=1 AngleXU=0 Radius=2 StartAngle=3.14159 EndAngle=6.28319
    g1: ArcOfCircle CenterX=28 CenterY=45 CenterZ=0 NormalX=0 NormalY=0 NormalZ=1 AngleXU=0 Radius=2 StartAngle=0 EndAngle=3.14159
    g2: LineSegment StartX=30 StartY=35 StartZ=0 EndX=30 EndY=45 EndZ=0
    g3: LineSegment StartX=26 StartY=35 StartZ=0 EndX=26 EndY=45 EndZ=0
  constraints (10):
    c: Tangent(g0,g3) = 1.5708
    c: Tangent(g0,g2) = -1.5708
    c: Tangent(g2,g1) = -1.5708
    c: Tangent(g3,g1) = 1.5708
    c: Vertical(g2)
    c: Equal(g0,g1)
    c: Radius(g0) = 2
    c: DistanceY(g2,g2) = 10
    c: DistanceX(g0) = 28
    c: DistanceY(g0) = 35
FEATURE [PartDesign::Pocket] Pocket039
  BaseFeature = -> Pocket038
  Direction = (0,0,1)
  Length = 5
  Length2 = 100
  Profile = -> Sketch074
  SideType = 0
  Suppressed = false
  Type = 1
  Type2 = 0
FEATURE [PartDesign::LinearPattern] LinearPattern002
  Direction = -> Sketch074 [H_Axis]
  Length = 84
  Length2 = 100
  Mode = 0
  Mode2 = 0
  Occurrences = 4
  Occurrences2 = 1
  Offset = 28
  Offset2 = 10
  Reversed = true
  Reversed2 = false
  SpacingPattern = [0]
  SpacingPattern2 = [0]
  Spacings = [-1,-1,-1]
  Suppressed = false
  TransformMode = 0
FEATURE [PartDesign::LinearPattern] LinearPattern003
  Direction = -> Sketch074 [V_Axis]
  Length = 30
  Length2 = 100
  Mode = 0
  Mode2 = 0
  Occurrences = 2
  Occurrences2 = 1
  Offset = 30
  Offset2 = 10
  Reversed2 = false
  SpacingPattern = [0]
  SpacingPattern2 = [0]
  Spacings = [-1]
  Suppressed = false
  TransformMode = 0
FEATURE [PartDesign::MultiTransform] MultiTransform002
  BaseFeature = -> Pocket039
  Originals = -> [Pocket039]
  Suppressed = false
  TransformMode = 0
  Transformations = -> [LinearPattern002,LinearPattern003]
FEATURE [Sketcher::SketchObject] Sketch075
  ArcFitTolerance = 0
  AttachmentSupport = -> [MultiTransform002]
  ExternalTypes = [0]
  FullyConstrained = true
  MakeInternals = false
  MapMode = 5
  Placement = pos=(0,0,16) rot=(1,0,0;3.14159rad)
  sketch-geometry (4):
    g0: Circle CenterX=16.5 CenterY=15.5 CenterZ=0 NormalX=0 NormalY=0 NormalZ=1 AngleXU=0 Radius=1.6
    g1: Circle CenterX=16.5 CenterY=-15.5 CenterZ=0 NormalX=0 NormalY=0 NormalZ=1 AngleXU=0 Radius=1.6
    g2: Circle CenterX=-14.5 CenterY=-15.5 CenterZ=0 NormalX=0 NormalY=0 NormalZ=1 AngleXU=0 Radius=1.6
    g3: Circle CenterX=-14.5 CenterY=15.5 CenterZ=0 NormalX=0 NormalY=0 NormalZ=1 AngleXU=0 Radius=1.6
  constraints (11):
    c: Equal(g0,g3)
    c: Equal(g3,g1)
    c: Equal(g1,g2)
    c: Diameter(g1) = 3.2
    c: DistanceY(g1,g0) = 31
    c: Vertical(g2,g3)
    c: Horizontal(g3,g0)
    c: Horizontal(g2,g1)
    c: DistanceX(g1) = 16.5
    c: DistanceX(g2,g1) = 31
    c: Symmetric(g0,g1,g-1)
FEATURE [PartDesign::Pocket] Pocket040
  BaseFeature = -> MultiTransform002
  Direction = (0,0,1)
  Length = 5
  Length2 = 100
  Profile = -> Sketch075
  SideType = 0
  Suppressed = false
  Type = 1
  Type2 = 0
FEATURE [PartDesign::Chamfer] Chamfer006
  Angle = 45
  Base = -> Pocket040 [Edge4,Edge2]
  BaseFeature = -> Pocket040
  ChamferType = 0
  FlipDirection = false
  Size = 5
  Size2 = 1
  SupportTransform = true
  Suppressed = false
  UseAllEdges = false
FEATURE [PartDesign::Chamfer] Chamfer007
  Angle = 45
  Base = -> Chamfer006 [Edge91,Edge89,Edge88]
  BaseFeature = -> Chamfer006
  ChamferType = 0
  FlipDirection = false
  Size = 10
  Size2 = 1
  SupportTransform = true
  Suppressed = false
  UseAllEdges = false
FEATURE [PartDesign::Fillet] Fillet004
  Base = -> Chamfer007 [Edge55]
  BaseFeature = -> Chamfer007
  Radius = 20
  SupportTransform = true
  Suppressed = false
  UseAllEdges = false
FEATURE [Sketcher::SketchObject] Sketch076
  ArcFitTolerance = 0
  AttachmentSupport = -> [Fillet004]
  ExternalGeometry = -> [Fillet004]
  ExternalTypes = [0]
  FullyConstrained = true
  MakeInternals = false
  MapMode = 5
  Placement = pos=(0,0,20) rot=(0,0,1;0rad)
  sketch-geometry (1):
    g0: Circle CenterX=-40 CenterY=-4.25258e-11 CenterZ=0 NormalX=0 NormalY=0 NormalZ=1 AngleXU=0 Radius=16
  constraints (2):
    c: Coincident(g0,g-3)
    c: Diameter(g0) = 32
FEATURE [PartDesign::Pocket] Pocket041
  BaseFeature = -> Fillet004
  Direction = (0,0,-1)
  Length = 16
  Length2 = 100
  Profile = -> Sketch076
  SideType = 0
  Suppressed = false
  Type = 0
  Type2 = 0
FEATURE [Sketcher::SketchObject] Sketch077
  ArcFitTolerance = 0
  AttachmentSupport = -> [Pocket041]
  ExternalGeometry = -> [Pocket041]
  ExternalTypes = [0]
  FullyConstrained = true
  MakeInternals = false
  MapMode = 5
  Placement = pos=(0,0,20) rot=(0,0,1;0rad)
  sketch-geometry (4):
    g0: Circle CenterX=16.5 CenterY=15.5 CenterZ=0 NormalX=0 NormalY=0 NormalZ=1 AngleXU=0 Radius=3
    g1: Circle CenterX=-14.5 CenterY=15.5 CenterZ=0 NormalX=0 NormalY=0 NormalZ=1 AngleXU=0 Radius=3
    g2: Circle CenterX=-14.5 CenterY=-15.5 CenterZ=0 NormalX=0 NormalY=0 NormalZ=1 AngleXU=0 Radius=3
    g3: Circle CenterX=16.5 CenterY=-15.5 CenterZ=0 NormalX=0 NormalY=0 NormalZ=1 AngleXU=0 Radius=3
  constraints (8):
    c: Diameter(g3) = 6
    c: Equal(g3,g2)
    c: Equal(g3,g1)
    c: Equal(g3,g0)
    c: Coincident(g2,g-6)
    c: Coincident(g3,g-5)
    c: Coincident(g0,g-4)
    c: Coincident(g1,g-3)
FEATURE [PartDesign::Pocket] Pocket042
  BaseFeature = -> Pocket041
  Direction = (0,0,-1)
  Length = 2
  Length2 = 100
  Profile = -> Sketch077
  SideType = 0
  Suppressed = false
  Type = 0
  Type2 = 0
FEATURE [Sketcher::SketchObject] Sketch078
  ArcFitTolerance = 0
  AttachmentSupport = -> [Pocket042]
  ExternalGeometry = -> [Pocket042]
  ExternalTypes = [0]
  FullyConstrained = true
  MakeInternals = false
  MapMode = 5
  Placement = pos=(0,0,16) rot=(1,0,0;3.14159rad)
  sketch-geometry (16):
    g0: ArcOfCircle CenterX=-14.5 CenterY=-15.5 CenterZ=0 NormalX=0 NormalY=0 NormalZ=1 AngleXU=0 Radius=1.6 StartAngle=4.71239 EndAngle=7.85398
    g1: ArcOfCircle CenterX=-16.5 CenterY=-15.5 CenterZ=0 NormalX=0 NormalY=0 NormalZ=1 AngleXU=0 Radius=1.6 StartAngle=1.5708 EndAngle=4.71239
    g2: LineSegment StartX=-14.5 StartY=-13.9 StartZ=0 EndX=-16.5 EndY=-13.9 EndZ=0
    g3: LineSegment StartX=-14.5 StartY=-17.1 StartZ=0 EndX=-16.5 EndY=-17.1 EndZ=0
    g4: ArcOfCircle CenterX=-14.5 CenterY=15.5 CenterZ=0 NormalX=0 NormalY=0 NormalZ=1 AngleXU=0 Radius=1.6 StartAngle=4.71239 EndAngle=7.85398
    g5: ArcOfCircle CenterX=-16.5 CenterY=15.5 CenterZ=0 NormalX=0 NormalY=0 NormalZ=1 AngleXU=0 Radius=1.6 StartAngle=1.5708 EndAngle=4.71239
    g6: LineSegment StartX=-14.5 StartY=17.1 StartZ=0 EndX=-16.5 EndY=17.1 EndZ=0
    g7: LineSegment StartX=-14.5 StartY=13.9 StartZ=0 EndX=-16.5 EndY=13.9 EndZ=0
    g8: ArcOfCircle CenterX=16.5 CenterY=15.5 CenterZ=0 NormalX=0 NormalY=0 NormalZ=1 AngleXU=0 Radius=1.6 StartAngle=4.71239 EndAngle=7.85398
    g9: ArcOfCircle CenterX=14.5 CenterY=15.5 CenterZ=0 NormalX=0 NormalY=0 NormalZ=1 AngleXU=0 Radius=1.6 StartAngle=1.5708 EndAngle=4.71239
    g10: LineSegment StartX=16.5 StartY=17.1 StartZ=0 EndX=14.5 EndY=17.1 EndZ=0
    g11: LineSegment StartX=16.5 StartY=13.9 StartZ=0 EndX=14.5 EndY=13.9 EndZ=0
    g12: ArcOfCircle CenterX=16.5 CenterY=-15.5 CenterZ=0 NormalX=0 NormalY=0 NormalZ=1 AngleXU=0 Radius=1.6 StartAngle=4.71239 EndAngle=7.85398
    g13: ArcOfCircle CenterX=14.5 CenterY=-15.5 CenterZ=0 NormalX=0 NormalY=0 NormalZ=1 AngleXU=0 Radius=1.6 StartAngle=1.5708 EndAngle=4.71239
    g14: LineSegment StartX=16.5 StartY=-13.9 StartZ=0 EndX=14.5 EndY=-13.9 EndZ=0
    g15: LineSegment StartX=16.5 StartY=-17.1 StartZ=0 EndX=14.5 EndY=-17.1 EndZ=0
  constraints (36):
    c: Tangent(g0,g3) = 1.5708
    c: Tangent(g0,g2) = -1.5708
    c: Tangent(g2,g1) = -1.5708
    c: Tangent(g3,g1) = 1.5708
    c: Horizontal(g2)
    c: Equal(g0,g1)
    c: Coincident(g0,g-4)
    c: Tangent(g4,g7) = 1.5708
    c: Tangent(g4,g6) = -1.5708
    c: Tangent(g6,g5) = -1.5708
    c: Tangent(g7,g5) = 1.5708
    c: Horizontal(g6)
    c: Equal(g4,g5)
    c: Coincident(g4,g-3)
    c: Tangent(g8,g11) = 1.5708
    c: Tangent(g8,g10) = -1.5708
    c: Tangent(g10,g9) = -1.5708
    c: Tangent(g11,g9) = 1.5708
    c: Horizontal(g10)
    c: Equal(g8,g9)
    c: Coincident(g8,g-6)
    c: Tangent(g12,g15) = 1.5708
    c: Tangent(g12,g14) = -1.5708
    c: Tangent(g14,g13) = -1.5708
    c: Tangent(g15,g13) = 1.5708
    c: Horizontal(g14)
    c: Equal(g12,g13)
    c: Coincident(g12,g-5)
    c: Equal(g0,g-4)
    c: Equal(g-4,g4)
    c: Equal(g4,g8)
    c: Equal(g8,g12)
    c: Equal(g6,g2)
    c: Equal(g2,g14)
    c: Equal(g14,g10)
    c: DistanceX(g14,g14) = 2
FEATURE [PartDesign::Pocket] Pocket043
  BaseFeature = -> Pocket042
  Direction = (0,0,1)
  Length = 5
  Length2 = 100
  Profile = -> Sketch078
  SideType = 0
  Suppressed = false
  Type = 1
  Type2 = 0
FEATURE [Sketcher::SketchObject] Sketch079
  ArcFitTolerance = 0
  AttachmentSupport = -> [Pocket043]
  ExternalGeometry = -> [Pocket043]
  ExternalTypes = [0]
  FullyConstrained = true
  MakeInternals = false
  MapMode = 5
  Placement = pos=(0,0,0) rot=(1,0,0;3.14159rad)
  sketch-geometry (4):
    g0: LineSegment StartX=-19 StartY=21 StartZ=0 EndX=-23 EndY=21 EndZ=0
    g1: LineSegment StartX=-23 StartY=21 StartZ=0 EndX=-23 EndY=-21 EndZ=0
    g2: LineSegment StartX=-23 StartY=-21 StartZ=0 EndX=-19 EndY=-21 EndZ=0
    g3: LineSegment StartX=-19 StartY=-21 StartZ=0 EndX=-19 EndY=21 EndZ=0
  constraints (10):
    c: Coincident(g0,g1)
    c: Coincident(g1,g2)
    c: Coincident(g2,g3)
    c: Coincident(g3,g0)
    c: Horizontal(g0)
    c: Horizontal(g2)
    c: Vertical(g1)
    c: Coincident(g0,g-3)
    c: Coincident(g2,g-3)
    c: DistanceX(g2,g2) = 4
FEATURE [PartDesign::Pocket] Pocket044
  BaseFeature = -> Pocket043
  Direction = (0,0,1)
  Length = 0
  Length2 = 100
  Profile = -> Sketch079
  SideType = 0
  Suppressed = false
  Type = 3
  Type2 = 0
  UpToFace = -> Pocket043 [Face52]
FEATURE [Sketcher::SketchObject] Sketch080
  ArcFitTolerance = 0
  AttachmentSupport = -> [Pocket044]
  ExternalGeometry = -> [Pocket044]
  ExternalTypes = [0]
  FullyConstrained = true
  MakeInternals = false
  MapMode = 5
  Placement = pos=(0,0,20) rot=(0,0,1;0rad)
  sketch-geometry (16):
    g0: ArcOfCircle CenterX=-14.5 CenterY=15.5 CenterZ=0 NormalX=0 NormalY=0 NormalZ=1 AngleXU=0 Radius=3 StartAngle=4.71239 EndAngle=7.85398
    g1: ArcOfCircle CenterX=-16.5 CenterY=15.5 CenterZ=0 NormalX=0 NormalY=0 NormalZ=1 AngleXU=0 Radius=3 StartAngle=1.5708 EndAngle=4.71239
    g2: LineSegment StartX=-14.5 StartY=18.5 StartZ=0 EndX=-16.5 EndY=18.5 EndZ=0
    g3: LineSegment StartX=-14.5 StartY=12.5 StartZ=0 EndX=-16.5 EndY=12.5 EndZ=0
    g4: ArcOfCircle CenterX=16.5 CenterY=15.5 CenterZ=0 NormalX=0 NormalY=0 NormalZ=1 AngleXU=0 Radius=3 StartAngle=4.71239 EndAngle=7.85398
    g5: ArcOfCircle CenterX=14.5 CenterY=15.5 CenterZ=0 NormalX=0 NormalY=0 NormalZ=1 AngleXU=0 Radius=3 StartAngle=1.5708 EndAngle=4.71239
    g6: LineSegment StartX=16.5 StartY=18.5 StartZ=0 EndX=14.5 EndY=18.5 EndZ=0
    g7: LineSegment StartX=16.5 StartY=12.5 StartZ=0 EndX=14.5 EndY=12.5 EndZ=0
    g8: ArcOfCircle CenterX=-14.5 CenterY=-15.5 CenterZ=0 NormalX=0 NormalY=0 NormalZ=1 AngleXU=0 Radius=3 StartAngle=4.71239 EndAngle=7.85398
    g9: ArcOfCircle CenterX=-16.5 CenterY=-15.5 CenterZ=0 NormalX=0 NormalY=0 NormalZ=1 AngleXU=0 Radius=3 StartAngle=1.5708 EndAngle=4.71239
    g10: LineSegment StartX=-14.5 StartY=-12.5 StartZ=0 EndX=-16.5 EndY=-12.5 EndZ=0
    g11: LineSegment StartX=-14.5 StartY=-18.5 StartZ=0 EndX=-16.5 EndY=-18.5 EndZ=0
    g12: ArcOfCircle CenterX=16.5 CenterY=-15.5 CenterZ=0 NormalX=0 NormalY=0 NormalZ=1 AngleXU=0 Radius=3 StartAngle=4.71239 EndAngle=7.85398
    g13: ArcOfCircle CenterX=14.5 CenterY=-15.5 CenterZ=0 NormalX=0 NormalY=0 NormalZ=1 AngleXU=0 Radius=3 StartAngle=1.5708 EndAngle=4.71239
    g14: LineSegment StartX=16.5 StartY=-12.5 StartZ=0 EndX=14.5 EndY=-12.5 EndZ=0
    g15: LineSegment StartX=16.5 StartY=-18.5 StartZ=0 EndX=14.5 EndY=-18.5 EndZ=0
  constraints (36):
    c: Tangent(g0,g3) = 1.5708
    c: Tangent(g0,g2) = -1.5708
    c: Tangent(g2,g1) = -1.5708
    c: Tangent(g3,g1) = 1.5708
    c: Horizontal(g2)
    c: Equal(g0,g1)
    c: Coincident(g0,g-3)
    c: Tangent(g4,g7) = 1.5708
    c: Tangent(g4,g6) = -1.5708
    c: Tangent(g6,g5) = -1.5708
    c: Tangent(g7,g5) = 1.5708
    c: Horizontal(g6)
    c: Equal(g4,g5)
    c: Coincident(g4,g-4)
    c: Tangent(g8,g11) = 1.5708
    c: Tangent(g8,g10) = -1.5708
    c: Tangent(g10,g9) = -1.5708
    c: Tangent(g11,g9) = 1.5708
    c: Horizontal(g10)
    c: Equal(g8,g9)
    c: Coincident(g8,g-6)
    c: Tangent(g12,g15) = 1.5708
    c: Tangent(g12,g14) = -1.5708
    c: Tangent(g14,g13) = -1.5708
    c: Tangent(g15,g13) = 1.5708
    c: Horizontal(g14)
    c: Equal(g12,g13)
    c: Coincident(g12,g-5)
    c: Equal(g12,g0)
    c: Equal(g0,g4)
    c: Equal(g4,g8)
    c: Equal(g8,g-4)
    c: Equal(g10,g14)
    c: Equal(g14,g3)
    c: Equal(g3,g7)
    c: DistanceX(g10,g10) = 2
FEATURE [PartDesign::Pocket] Pocket045
  BaseFeature = -> Pocket044
  Direction = (0,0,-1)
  Length = 0
  Length2 = 100
  Profile = -> Sketch080
  SideType = 0
  Suppressed = false
  Type = 3
  Type2 = 0
  UpToFace = -> Pocket044 [Face89]
FEATURE [Sketcher::SketchObject] Sketch081
  ArcFitTolerance = 0
  AttachmentSupport = -> [Pocket045]
  ExternalGeometry = -> [Pocket045]
  ExternalTypes = [0]
  FullyConstrained = true
  MakeInternals = false
  MapMode = 5
  Placement = pos=(0,0,20) rot=(0,0,1;0rad)
  sketch-geometry (4):
    g0: ArcOfCircle CenterX=0 CenterY=0 CenterZ=0 NormalX=0 NormalY=0 NormalZ=1 AngleXU=0 Radius=11 StartAngle=4.71239 EndAngle=7.85398
    g1: ArcOfCircle CenterX=-2 CenterY=9e-16 CenterZ=0 NormalX=0 NormalY=0 NormalZ=1 AngleXU=0 Radius=11 StartAngle=1.5708 EndAngle=4.71239
    g2: LineSegment StartX=-5.828e-13 StartY=11 StartZ=0 EndX=-2 EndY=11 EndZ=0
    g3: LineSegment StartX=-2e-15 StartY=-11 StartZ=0 EndX=-2 EndY=-11 EndZ=0
  constraints (9):
    c: Tangent(g0,g3) = 1.5708
    c: Tangent(g0,g2) = -1.5708
    c: Tangent(g2,g1) = -1.5708
    c: Tangent(g3,g1) = 1.5708
    c: Horizontal(g2)
    c: Equal(g0,g1)
    c: Coincident(g0,g-1)
    c: Equal(g0,g-3)
    c: DistanceX(g2,g2) = 2
FEATURE [PartDesign::Pocket] Pocket046
  BaseFeature = -> Pocket045
  Direction = (0,0,-1)
  Length = 5
  Length2 = 100
  Profile = -> Sketch081
  SideType = 0
  Suppressed = false
  Type = 1
  Type2 = 0
FEATURE [Sketcher::SketchObject] Sketch082
  ArcFitTolerance = 0
  AttachmentSupport = -> [Pocket046]
  ExternalTypes = [0]
  FullyConstrained = true
  MakeInternals = false
  MapMode = 5
  Placement = pos=(0,0,10) rot=(0,0,1;0rad)
  sketch-geometry (1):
    g0: Circle CenterX=14 CenterY=-65 CenterZ=0 NormalX=0 NormalY=0 NormalZ=1 AngleXU=0 Radius=6.5
  constraints (3):
    c: Diameter(g0) = 13
    c: DistanceX(g0) = 14
    c: DistanceY(g0) = -65
FEATURE [PartDesign::Pocket] Pocket047
  BaseFeature = -> Pocket046
  Direction = (0,0,-1)
  Length = 8
  Length2 = 100
  Profile = -> Sketch082
  SideType = 0
  Suppressed = false
  Type = 0
  Type2 = 0
FEATURE [PartDesign::LinearPattern] LinearPattern004
  Direction = -> Sketch082 [H_Axis]
  Length = 56
  Length2 = 100
  Mode = 0
  Mode2 = 0
  Occurrences = 3
  Occurrences2 = 1
  Offset = 28
  Offset2 = 10
  Reversed = true
  Reversed2 = false
  SpacingPattern = [0]
  SpacingPattern2 = [0]
  Spacings = [-1,-1]
  Suppressed = false
  TransformMode = 0
FEATURE [PartDesign::LinearPattern] LinearPattern005
  Direction = -> Sketch082 [V_Axis]
  Length = 30
  Length2 = 100
  Mode = 0
  Mode2 = 0
  Occurrences = 3
  Occurrences2 = 1
  Offset = 15
  Offset2 = 10
  Reversed2 = false
  SpacingPattern = [0]
  SpacingPattern2 = [0]
  Spacings = [-1,-1]
  Suppressed = false
  TransformMode = 0
FEATURE [PartDesign::MultiTransform] MultiTransform003
  BaseFeature = -> Pocket047
  Originals = -> [Pocket047]
  Refine = true
  Suppressed = false
  TransformMode = 0
  Transformations = -> [LinearPattern004,LinearPattern005]
FEATURE [PartDesign::Body] Body015  label="tube-gearbox-body"
  AllowCompound = true
  Group = -> [Sketch071,Pad028,Sketch072,Pocket037,Sketch073,Pocket038,Sketch074,Pocket039,MultiTransform002,LinearPattern002,LinearPattern003,Sketch075,Pocket040,Chamfer006,Chamfer007,Fillet004,Sketch076,Pocket041,Sketch077,Pocket042,Sketch078,Pocket043,Sketch079,Pocket044,Sketch080,Pocket045,Sketch081,Pocket046,Sketch082,Pocket047,MultiTransform003,LinearPattern004,LinearPattern005]
  Origin = -> Origin024
  Tip = -> MultiTransform003
FEATURE [App::Link] Link045  label="tube-gearbox-body001"
  LinkPlacement = pos=(-207.414,131.303,649.197) rot=(0.086966,0.984278,0.153736;1.59501rad)
  LinkedObject = -> Body015
  Placement = pos=(-207.414,131.303,649.197) rot=(0.086966,0.984278,0.153736;1.59501rad)
FEATURE [Sketcher::SketchObject] Sketch083
  ArcFitTolerance = 0
  AttachmentSupport = -> [XY_Plane025]
  ExternalTypes = [0]
  FullyConstrained = true
  MakeInternals = false
  MapMode = 5
  sketch-geometry (2):
    g0: Circle CenterX=0 CenterY=0 CenterZ=0 NormalX=0 NormalY=0 NormalZ=1 AngleXU=0 Radius=6
    g1: Circle CenterX=0 CenterY=0 CenterZ=0 NormalX=0 NormalY=0 NormalZ=1 AngleXU=0 Radius=16
  constraints (4):
    c: Coincident(g0,g-1)
    c: Coincident(g1,g0)
    c: Diameter(g0) = 12
    c: Diameter(g1) = 32
FEATURE [PartDesign::Pad] Pad029
  Direction = (0,0,1)
  Length = 15.9
  Length2 = 100
  Profile = -> Sketch083
  SideType = 2
  Suppressed = false
  Type = 0
  Type2 = 0
FEATURE [Sketcher::SketchObject] Sketch084
  ArcFitTolerance = 0
  AttachmentSupport = -> [Pad029]
  ExternalTypes = [0]
  FullyConstrained = true
  MakeInternals = false
  MapMode = 5
  Placement = pos=(0,0,7.95) rot=(0,0,1;0rad)
  sketch-geometry (2):
    g0: Circle CenterX=0 CenterY=0 CenterZ=0 NormalX=0 NormalY=0 NormalZ=1 AngleXU=0 Radius=7.75
    g1: Circle CenterX=0 CenterY=0 CenterZ=0 NormalX=0 NormalY=0 NormalZ=1 AngleXU=0 Radius=13.5
  constraints (4):
    c: Coincident(g0,g-1)
    c: Coincident(g1,g0)
    c: Diameter(g1) = 27
    c: Diameter(g0) = 15.5
FEATURE [PartDesign::Pocket] Pocket048
  BaseFeature = -> Pad029
  Direction = (0,0,-1)
  Length = 1
  Length2 = 100
  Profile = -> Sketch084
  SideType = 0
  Suppressed = false
  Type = 0
  Type2 = 0
FEATURE [PartDesign::Mirrored] Mirrored001
  BaseFeature = -> Pocket048
  MirrorPlane = -> XY_Plane025
  Originals = -> [Pocket048]
  Suppressed = false
  TransformMode = 0
FEATURE [PartDesign::Body] Body016  label="bearing5201"
  AllowCompound = true
  Group = -> [Sketch083,Pad029,Sketch084,Pocket048,Mirrored001]
  Origin = -> Origin025
  Tip = -> Mirrored001
FEATURE [App::Link] Link046  label="bearing5201_001"
  LinkPlacement = pos=(-194.834,122.462,688.009) rot=(0.086966,0.984278,0.153736;1.59501rad)
  LinkedObject = -> Body016
  Placement = pos=(-194.834,122.462,688.009) rot=(0.086966,0.984278,0.153736;1.59501rad)
FEATURE [Sketcher::SketchObject] Sketch085
  ArcFitTolerance = 0
  AttachmentSupport = -> [YZ_Plane026]
  ExternalTypes = [0]
  FullyConstrained = true
  MakeInternals = false
  MapMode = 5
  Placement = pos=(0,0,0) rot=(0.57735,0.57735,0.57735;2.0944rad)
  sketch-geometry (6):
    g0: LineSegment StartX=0 StartY=20 StartZ=0 EndX=7 EndY=20 EndZ=0
    g1: LineSegment StartX=7 StartY=20 StartZ=0 EndX=7 EndY=5 EndZ=0
    g2: LineSegment StartX=7 StartY=5 StartZ=0 EndX=3.9 EndY=5 EndZ=0
    g3: LineSegment StartX=3.9 StartY=5 StartZ=0 EndX=3.9 EndY=-20 EndZ=0
    g4: LineSegment StartX=3.9 StartY=-20 StartZ=0 EndX=0 EndY=-20 EndZ=0
    g5: LineSegment StartX=0 StartY=-20 StartZ=0 EndX=0 EndY=20 EndZ=0
  constraints (18):
    c: PointOnObject(g0,g-2)
    c: Horizontal(g0)
    c: Coincident(g0,g1)
    c: Vertical(g1)
    c: Coincident(g1,g2)
    c: Horizontal(g2)
    c: Coincident(g2,g3)
    c: Vertical(g3)
    c: Coincident(g3,g4)
    c: PointOnObject(g4,g-2)
    c: Horizontal(g4)
    c: Coincident(g4,g5)
    c: Coincident(g5,g0)
    c: DistanceX(g0) = 7
    c: DistanceY(g0) = 20
    c: DistanceX(g2) = 3.9
    c: DistanceY(g4) = -20
    c: DistanceY(g1) = 5
FEATURE [Sketcher::SketchObject] Sketch086
  ArcFitTolerance = 0
  AttachmentSupport = -> [XZ_Plane026]
  ExternalTypes = [0]
  FullyConstrained = true
  MakeInternals = false
  MapMode = 5
  Placement = pos=(0,0,0) rot=(1,0,0;1.5708rad)
  sketch-geometry (4):
    g0: LineSegment StartX=-28 StartY=0 StartZ=0 EndX=-25.8162 EndY=-6 EndZ=0
    g1: LineSegment StartX=-25.8162 StartY=-6 StartZ=0 EndX=-14.1838 EndY=-6 EndZ=0
    g2: LineSegment StartX=-14.1838 StartY=-6 StartZ=0 EndX=-12 EndY=0 EndZ=0
    g3: LineSegment StartX=-12 StartY=0 StartZ=0 EndX=-28 EndY=0 EndZ=0
  constraints (12):
    c: Coincident(g0,g1)
    c: Horizontal(g1)
    c: Coincident(g1,g2)
    c: Coincident(g2,g3)
    c: Coincident(g3,g0)
    c: Horizontal(g3)
    c: DistanceY(g1) = -6
    c: DistanceX(g0) = -28
    c: DistanceX(g2) = -12
    c: DistanceY(g2) = 0
    c: Equal(g2,g0)
    c: Angle(g2,g1) = 1.91986
FEATURE [Sketcher::SketchObject] Sketch087
  ArcFitTolerance = 0
  AttachmentSupport = -> [XY_Plane026]
  ExternalTypes = [0]
  FullyConstrained = true
  MakeInternals = false
  MapMode = 5
  sketch-geometry (1):
    g0: Circle CenterX=0 CenterY=20 CenterZ=0 NormalX=0 NormalY=0 NormalZ=1 AngleXU=0 Radius=5
  constraints (3):
    c: PointOnObject(g0,g-2)
    c: Diameter(g0) = 10
    c: DistanceY(g0) = 20
FEATURE [App::Link] Link047  label="tube-gearbox-output-gear001"
  LinkPlacement = pos=(-175.928,123.751,688.009) rot=(-0.587132,0.598497,-0.545048;2.00714rad)
  LinkedObject = -> Part004
  Placement = pos=(-175.928,123.751,688.009) rot=(-0.587132,0.598497,-0.545048;2.00714rad)
FEATURE [Sketcher::SketchObject] Sketch088
  ArcFitTolerance = 0
  AttachmentSupport = -> [XY_Plane028]
  ExternalTypes = [0]
  FullyConstrained = true
  MakeInternals = false
  MapMode = 5
  sketch-geometry (1):
    g0: Circle CenterX=0 CenterY=0 CenterZ=0 NormalX=0 NormalY=0 NormalZ=1 AngleXU=0 Radius=7
  constraints (2):
    c: Coincident(g0,g-1)
    c: Diameter(g0) = 14
FEATURE [PartDesign::Pad] Pad030
  Direction = (0,0,1)
  Length = 1
  Length2 = 100
  Profile = -> Sketch088
  SideType = 0
  Suppressed = false
  Type = 0
  Type2 = 0
FEATURE [Sketcher::SketchObject] Sketch089
  ArcFitTolerance = 0
  AttachmentSupport = -> [Pad030]
  ExternalTypes = [0]
  FullyConstrained = true
  MakeInternals = false
  MapMode = 5
  Placement = pos=(0,0,1) rot=(0,0,1;0rad)
  sketch-geometry (1):
    g0: Circle CenterX=0 CenterY=0 CenterZ=0 NormalX=0 NormalY=0 NormalZ=1 AngleXU=0 Radius=6
  constraints (2):
    c: Coincident(g0,g-1)
    c: Diameter(g0) = 12
FEATURE [PartDesign::Pad] Pad031
  BaseFeature = -> Pad030
  Direction = (0,0,1)
  Length = 15.5
  Length2 = 100
  Profile = -> Sketch089
  SideType = 0
  Suppressed = false
  Type = 0
  Type2 = 0
FEATURE [PartDesign::Chamfer] Chamfer008
  Angle = 45
  Base = -> Pad031 [Edge6]
  BaseFeature = -> Pad031
  ChamferType = 0
  FlipDirection = false
  Size = 1
  Size2 = 1
  SupportTransform = true
  Suppressed = false
  UseAllEdges = false
FEATURE [Sketcher::SketchObject] Sketch090
  ArcFitTolerance = 0
  AttachmentSupport = -> [Chamfer008]
  ExternalTypes = [0]
  FullyConstrained = true
  MakeInternals = false
  MapMode = 5
  Placement = pos=(0,0,16.5) rot=(0,0,1;0rad)
  sketch-geometry (1):
    g0: Circle CenterX=0 CenterY=0 CenterZ=0 NormalX=0 NormalY=0 NormalZ=1 AngleXU=0 Radius=3.85
  constraints (3):
    c: PointOnObject(g0,g-2)
    c: Diameter(g0) = 7.7
    c: DistanceY(g0) = 0
FEATURE [PartDesign::Pocket] Pocket050
  BaseFeature = -> Chamfer008
  Direction = (0,0,-1)
  Length = 5
  Length2 = 100
  Profile = -> Sketch090
  SideType = 0
  Suppressed = false
  Type = 1
  Type2 = 0
FEATURE [PartDesign::Body] Body018  label="m8-bolt-sleeve"
  AllowCompound = true
  Group = -> [Sketch088,Pad030,Sketch089,Pad031,Chamfer008,Sketch090,Pocket050]
  Origin = -> Origin028
  Tip = -> Pocket050
FEATURE [App::Link] Link048  label="m8-bolt-sleeve001"
  LinkPlacement = pos=(-185.904,123.071,688.009) rot=(-0.699853,-0.110229,0.705731;3.01704rad)
  LinkedObject = -> Body018
  Placement = pos=(-185.904,123.071,688.009) rot=(-0.699853,-0.110229,0.705731;3.01704rad)
FEATURE [Part::Feature] BOLTS_part  label="Hex socket head cap screw M8 40.0"
  shape: bbox 13 x 13 x 48 mm, 13 faces (baked)
FEATURE [PartDesign::FeatureBase] BaseFeature004
  BaseFeature = -> BOLTS_part
  Suppressed = false
FEATURE [PartDesign::Body] Body019  label="m8x40imb"
  AllowCompound = true
  BaseFeature = -> BOLTS_part
  Group = -> [BaseFeature004]
  Origin = -> Origin029
  Tip = -> BaseFeature004
FEATURE [App::Part] Part005  label="bolt-m8x40imb"
  Group = -> [BOLTS_part,Body019]
  Origin = -> Origin030
FEATURE [App::Link] Link049  label="bolt-m8x40imb001"
  LinkPlacement = pos=(-162.958,124.636,688.009) rot=(-0.699853,-0.110229,0.705731;3.01704rad)
  LinkedObject = -> Part005
  Placement = pos=(-162.958,124.636,688.009) rot=(-0.699853,-0.110229,0.705731;3.01704rad)
FEATURE [App::Link] Link050  label="nema017_002"
  LinkPlacement = pos=(-231.359,129.67,649.197) rot=(0.086966,0.984278,0.153736;1.59501rad)
  LinkedObject = -> Body008
  Placement = pos=(-231.359,129.67,649.197) rot=(0.086966,0.984278,0.153736;1.59501rad)
FEATURE [App::Link] Link051  label="tube-gearbox-motor-gear001"
  LinkPlacement = pos=(-176.985,133.379,649.197) rot=(-0.693438,-0.159356,0.702673;2.91891rad)
  LinkedObject = -> Part006
  Placement = pos=(-176.985,133.379,649.197) rot=(-0.693438,-0.159356,0.702673;2.91891rad)
FEATURE [App::Point] Origin033  label="Odniesienie położenia"
  Role = Origin
FEATURE [App::Point] Origin034  label="Odniesienie położenia"
  Role = Origin
FEATURE [App::Point] Origin035  label="Odniesienie położenia"
  Role = Origin
FEATURE [App::Point] Origin036  label="Odniesienie położenia"
  Role = Origin
FEATURE [App::Point] Origin037  label="Odniesienie położenia"
  Role = Origin
FEATURE [App::Point] Origin038  label="Odniesienie położenia"
  Role = Origin
FEATURE [App::Point] Origin039  label="Odniesienie położenia"
  Role = Origin
FEATURE [App::Point] Origin040  label="Odniesienie położenia"
  Role = Origin
FEATURE [App::Point] Origin041  label="Odniesienie położenia"
  Role = Origin
FEATURE [App::Point] Origin042  label="Odniesienie położenia"
  Role = Origin
FEATURE [App::Point] Origin043  label="Odniesienie położenia"
  Role = Origin
FEATURE [App::Point] Origin044  label="Odniesienie położenia"
  Role = Origin
FEATURE [App::Point] Origin045  label="Odniesienie położenia"
  Role = Origin
FEATURE [App::Point] Origin046  label="Odniesienie położenia"
  Role = Origin
FEATURE [App::Point] Origin047  label="Odniesienie położenia"
  Role = Origin
FEATURE [App::Point] Origin048  label="Odniesienie położenia"
  Role = Origin
FEATURE [App::Point] Origin049  label="Odniesienie położenia"
  Role = Origin
FEATURE [App::Point] Origin050  label="Odniesienie położenia"
  Role = Origin
FEATURE [App::Point] Origin051  label="Odniesienie położenia"
  Role = Origin
FEATURE [App::Point] Origin052  label="Odniesienie położenia"
  Role = Origin
FEATURE [App::Point] Origin053  label="Odniesienie położenia"
  Role = Origin
FEATURE [App::Point] Origin054  label="Odniesienie położenia"
  Role = Origin
FEATURE [App::Point] Origin055  label="Odniesienie położenia"
  Role = Origin
FEATURE [App::Point] Origin056  label="Odniesienie położenia"
  Role = Origin
FEATURE [App::Point] Origin057  label="Odniesienie położenia"
  Role = Origin
FEATURE [App::Point] Origin058  label="Odniesienie położenia"
  Role = Origin
FEATURE [App::Point] Origin059  label="Odniesienie położenia"
  Role = Origin
FEATURE [App::Point] Origin060  label="Odniesienie położenia"
  Role = Origin
FEATURE [App::Point] Origin061  label="Odniesienie położenia"
  Role = Origin
FEATURE [App::Point] Origin062  label="Odniesienie położenia"
  Role = Origin
FEATURE [App::Point] Origin063  label="Odniesienie położenia"
  Role = Origin
FEATURE [Part::FeaturePython] InvoluteGear  label="InvoluteGear003"  # WARN: FeaturePython — macro-defined, semantics opaque (R4)
  AttacherType = Attacher::AttachEngine3D
  addendum_diameter = 266
  angular_backlash = 0
  axle_hole = false
  axle_holesize = 10
  backlash = 0
  clearance = 0.25
  double_helix = false
  head = 0
  head_fillet = 0
  height = 29
  helix_angle = 0
  module = 1
  num_teeth = 264
  numpoints = 20
  offset_hole = false
  offset_holeoffset = 10
  offset_holesize = 10
  pitch_diameter = 264
  pressure_angle = 20
  properties_from_tool = false
  reversed_backlash = false
  root_diameter = 261.5
  root_fillet = 0
  shift = 0
  simple = false
  transverse_pitch = 3.14159
  traverse_module = 1
  undercut = false
  version = 1.3.0
  expr: angular_backlash = backlash / pitch_diameter * 360 ° / pi
FEATURE [PartDesign::FeatureBase] BaseFeature002
  BaseFeature = -> InvoluteGear
  Suppressed = false
FEATURE [Sketcher::SketchObject] Sketch050
  ArcFitTolerance = 0
  AttachmentSupport = -> [BaseFeature002]
  ExternalTypes = [0]
  FullyConstrained = true
  MakeInternals = false
  MapMode = 5
  Placement = pos=(0,0,29) rot=(0,0,1;0rad)
  sketch-geometry (1):
    g0: Circle CenterX=0 CenterY=0 CenterZ=0 NormalX=0 NormalY=0 NormalZ=1 AngleXU=0 Radius=90
  constraints (2):
    c: Coincident(g0,g-1)
    c: Diameter(g0) = 180
FEATURE [PartDesign::Pocket] Pocket025  label="Pocket025-mount-diameter"
  BaseFeature = -> BaseFeature002
  Direction = (0,0,-1)
  Length = 5
  Length2 = 100
  Profile = -> Sketch050
  SideType = 0
  Suppressed = false
  Type = 1
  Type2 = 0
FEATURE [PartDesign::Pocket] Pocket026  label="Pocket026-tube-diameter"
  BaseFeature = -> Pocket025
  Direction = (0,1,-2e-16)
  Length = 5
  Length2 = 100
  Profile = -> Sketch051
  SideType = 2
  Suppressed = false
  Type = 1
  Type2 = 0
FEATURE [PartDesign::Pocket] Pocket027
  BaseFeature = -> Pocket026
  Direction = (0,0,-1)
  Length = 5
  Length2 = 100
  Profile = -> Sketch052
  Reversed = true
  SideType = 0
  Suppressed = false
  Type = 1
  Type2 = 0
FEATURE [PartDesign::Groove] Groove001
  Angle = 360
  Angle2 = 60
  Axis = (1,0,0)
  Base = (0,0,5)
  BaseFeature = -> Pocket027
  Profile = -> Sketch053
  ReferenceAxis = -> Sketch053 [H_Axis]
  Reversed = true
  Suppressed = false
  Type = 0
FEATURE [PartDesign::MultiTransform] MultiTransform001
  BaseFeature = -> Groove001
  Originals = -> [Groove001]
  Suppressed = false
  TransformMode = 0
  Transformations = -> [PolarPattern004,Mirrored]
FEATURE [PartDesign::Pocket] Pocket028
  BaseFeature = -> MultiTransform001
  Direction = (0,0,-1)
  Length = 5
  Length2 = 100
  Profile = -> Sketch054
  Reversed = true
  SideType = 0
  Suppressed = false
  Type = 1
  Type2 = 0
FEATURE [PartDesign::Pocket] Pocket029
  BaseFeature = -> Pocket028
  Direction = (0,0,-1)
  Length = 5
  Length2 = 100
  Profile = -> Sketch055
  Reversed = true
  SideType = 0
  Suppressed = false
  Type = 1
  Type2 = 0
FEATURE [PartDesign::PolarPattern] PolarPattern005
  Angle = 112
  Axis = -> Z_Axis020
  BaseFeature = -> Pocket029
  Mode = 0
  Occurrences = 6
  Offset = 120
  Originals = -> [Pocket029]
  Reversed = true
  SpacingPattern = [0]
  Spacings = [-1,-1,-1,-1,-1]
  Suppressed = false
  TransformMode = 0
FEATURE [PartDesign::Pocket] Pocket030
  BaseFeature = -> PolarPattern005
  Direction = (0,0,-1)
  Length = 20
  Length2 = 100
  Profile = -> Sketch056
  ReferenceAxis = -> Sketch056 [N_Axis]
  Reversed = true
  SideType = 0
  Suppressed = false
  Type = 0
  Type2 = 0
FEATURE [PartDesign::Fillet] Fillet003
  Base = -> Pocket030 [Edge44]
  BaseFeature = -> Pocket030
  Radius = 3
  SupportTransform = true
  Suppressed = false
  UseAllEdges = false
FEATURE [PartDesign::Pocket] Pocket031
  BaseFeature = -> Fillet003
  Direction = (0,0,-1)
  Length = 5
  Length2 = 100
  Profile = -> Sketch057
  Reversed = true
  SideType = 0
  Suppressed = false
  Type = 1
  Type2 = 0
FEATURE [PartDesign::PolarPattern] PolarPattern006
  Angle = 120
  Axis = -> Sketch057 [N_Axis]
  BaseFeature = -> Pocket031
  Mode = 0
  Occurrences = 10
  Offset = 120
  Originals = -> [Pocket031]
  Reversed = true
  SpacingPattern = [0]
  Spacings = [-1,-1,-1,-1,-1,-1,-1,-1,-1]
  Suppressed = false
  TransformMode = 0
FEATURE [PartDesign::Pocket] Pocket032
  BaseFeature = -> PolarPattern006
  Direction = (0,0,-1)
  Length = 5
  Length2 = 100
  Profile = -> Sketch058
  Reversed = true
  SideType = 0
  Suppressed = false
  Type = 1
  Type2 = 0
FEATURE [PartDesign::Body] Body013  label="tube-gear"
  AllowCompound = true
  Group = -> [BaseFeature002,Sketch050,Pocket025,Sketch051,Pocket026,Sketch052,Pocket027,DatumPlane003,Sketch053,Groove001,MultiTransform001,PolarPattern004,Mirrored,Sketch054,Pocket028,Sketch055,Pocket029,PolarPattern005,Sketch056,Pocket030,Fillet003,Sketch057,Pocket031,PolarPattern006,Sketch058,Pocket032]
  Origin = -> Origin020
  Tip = -> Pocket032
FEATURE [App::Part] Part003  label="tube-main-gear"
  Group = -> [InvoluteGear,Body013]
  Origin = -> Origin021
FEATURE [Part::FeaturePython] InvoluteGear001  label="InvoluteGear004"  # WARN: FeaturePython — macro-defined, semantics opaque (R4)
  AttacherType = Attacher::AttachEngine3D
  addendum_diameter = 18
  angular_backlash = 0
  axle_hole = false
  axle_holesize = 10
  backlash = 0
  clearance = 0.25
  double_helix = false
  head = 0
  head_fillet = 0
  height = 12
  helix_angle = 0
  module = 1
  num_teeth = 16
  numpoints = 20
  offset_hole = false
  offset_holeoffset = 10
  offset_holesize = 10
  pitch_diameter = 16
  pressure_angle = 20
  properties_from_tool = false
  reversed_backlash = false
  root_diameter = 13.5
  root_fillet = 0
  shift = 0
  simple = false
  transverse_pitch = 3.14159
  traverse_module = 1
  undercut = false
  version = 1.3.0
  expr: angular_backlash = backlash / pitch_diameter * 360 ° / pi
FEATURE [PartDesign::FeatureBase] BaseFeature005
  BaseFeature = -> InvoluteGear001
  Suppressed = false
FEATURE [Sketcher::SketchObject] Sketch091
  ArcFitTolerance = 0
  AttachmentSupport = -> [BaseFeature005]
  ExternalTypes = [0]
  FullyConstrained = true
  MakeInternals = false
  MapMode = 5
  Placement = pos=(0,0,0) rot=(1,0,0;3.14159rad)
  sketch-geometry (2):
    g0: ArcOfCircle CenterX=0 CenterY=0 CenterZ=0 NormalX=0 NormalY=0 NormalZ=1 AngleXU=0 Radius=2.55 StartAngle=0.636936 EndAngle=5.64625
    g1: LineSegment StartX=2.05 StartY=1.51658 StartZ=0 EndX=2.05 EndY=-1.51658 EndZ=0
  constraints (6):
    c: Coincident(g0,g-1)
    c: Diameter(g0) = 5.1
    c: Vertical(g1)
    c: Coincident(g0,g1)
    c: Coincident(g0,g1)
    c: DistanceX(g0) = 2.05
FEATURE [PartDesign::Pocket] Pocket051
  BaseFeature = -> BaseFeature005
  Direction = (0,0,1)
  Length = 25
  Length2 = 100
  Profile = -> Sketch091
  SideType = 0
  Suppressed = false
  Type = 1
  Type2 = 0
FEATURE [PartDesign::Chamfer] Chamfer009
  Angle = 45
  Base = -> Pocket051 [Edge199,Edge200]
  BaseFeature = -> Pocket051
  ChamferType = 1
  FlipDirection = false
  Size = 0.5
  Size2 = 1
  SupportTransform = true
  Suppressed = false
  UseAllEdges = false
FEATURE [PartDesign::Body] Body020  label="tube-motor-gear"
  AllowCompound = true
  BaseFeature = -> InvoluteGear001
  Group = -> [BaseFeature005,Sketch091,Pocket051,Chamfer009]
  Origin = -> Origin031
  Placement = pos=(0,0,0) rot=(0,0,1;0.139626rad)
  Tip = -> Chamfer009
FEATURE [App::Part] Part006  label="tube-gearbox-motor-gear"
  Group = -> [Body020,InvoluteGear001]
  Origin = -> Origin032
FEATURE [Part::FeaturePython] InvoluteGear002  label="InvoluteGear005"  # WARN: FeaturePython — macro-defined, semantics opaque (R4)
  AttacherType = Attacher::AttachEngine3D
  addendum_diameter = 22
  angular_backlash = 0
  axle_hole = false
  axle_holesize = 10
  backlash = 0
  clearance = 0.25
  double_helix = false
  head = 0
  head_fillet = 0
  height = 15
  helix_angle = 0
  module = 1
  num_teeth = 20
  numpoints = 20
  offset_hole = false
  offset_holeoffset = 10
  offset_holesize = 10
  pitch_diameter = 20
  pressure_angle = 20
  properties_from_tool = false
  reversed_backlash = false
  root_diameter = 17.5
  root_fillet = 0
  shift = 0
  simple = false
  transverse_pitch = 3.14159
  traverse_module = 1
  undercut = false
  version = 1.3.0
  expr: angular_backlash = backlash / pitch_diameter * 360 ° / pi
FEATURE [Part::FeaturePython] InvoluteGear003  label="InvoluteGear006"  # WARN: FeaturePython — macro-defined, semantics opaque (R4)
  AttacherType = Attacher::AttachEngine3D
  Placement = pos=(0,0,-10) rot=(0,0,1;0rad)
  addendum_diameter = 66
  angular_backlash = 0
  axle_hole = false
  axle_holesize = 10
  backlash = 0
  clearance = 0.25
  double_helix = false
  head = 0
  head_fillet = 0
  height = 10
  helix_angle = 0
  module = 1
  num_teeth = 64
  numpoints = 20
  offset_hole = false
  offset_holeoffset = 10
  offset_holesize = 10
  pitch_diameter = 64
  pressure_angle = 20
  properties_from_tool = false
  reversed_backlash = false
  root_diameter = 61.5
  root_fillet = 0
  shift = 0
  simple = false
  transverse_pitch = 3.14159
  traverse_module = 1
  undercut = false
  version = 1.3.0
  expr: angular_backlash = backlash / pitch_diameter * 360 ° / pi
FEATURE [Part::Fuse] Fusion
  Base = -> InvoluteGear002
  Tool = -> InvoluteGear003
FEATURE [PartDesign::FeatureBase] BaseFeature003
  BaseFeature = -> Fusion
  Suppressed = false
FEATURE [PartDesign::Groove] Groove002
  Angle = 360
  Angle2 = 60
  Axis = (0,0,1)
  Base = (0,0,0)
  BaseFeature = -> BaseFeature003
  Profile = -> Sketch085
  ReferenceAxis = -> Sketch085 [V_Axis]
  Suppressed = false
  Type = 0
FEATURE [PartDesign::Groove] Groove003
  Angle = 360
  Angle2 = 60
  Axis = (0,2e-16,1)
  Base = (0,0,0)
  BaseFeature = -> Groove002
  Profile = -> Sketch086
  ReferenceAxis = -> Sketch086 [V_Axis]
  Reversed = true
  Suppressed = false
  Type = 0
FEATURE [PartDesign::Pocket] Pocket049
  BaseFeature = -> Groove003
  Direction = (0,0,-1)
  Length = 5
  Length2 = 100
  Profile = -> Sketch087
  SideType = 0
  Suppressed = false
  Type = 1
  Type2 = 0
FEATURE [PartDesign::PolarPattern] PolarPattern007
  Angle = 360
  Axis = -> Sketch087 [N_Axis]
  BaseFeature = -> Pocket049
  Mode = 0
  Occurrences = 8
  Offset = 120
  Originals = -> [Pocket049]
  SpacingPattern = [0]
  Spacings = [-1,-1,-1,-1,-1,-1,-1]
  Suppressed = false
  TransformMode = 0
FEATURE [PartDesign::Body] Body017  label="gearbox-output-gear"
  AllowCompound = true
  BaseFeature = -> Fusion
  Group = -> [BaseFeature003,Sketch085,Groove002,Sketch086,Groove003,Sketch087,Pocket049,PolarPattern007]
  Origin = -> Origin026
  Placement = pos=(0,0,0) rot=(0,0,1;0.15708rad)
  Tip = -> PolarPattern007
FEATURE [App::Part] Part004  label="tube-gearbox-output-gear"
  Group = -> [Fusion,Body017,InvoluteGear002,InvoluteGear003]
  Origin = -> Origin027
FEATURE [Part::FeaturePython] InvoluteGear004  label="InvoluteGear007"  # WARN: FeaturePython — macro-defined, semantics opaque (R4)
  AttacherType = Attacher::AttachEngine3D
  addendum_diameter = 530
  angular_backlash = 0
  axle_hole = false
  axle_holesize = 10
  backlash = 0
  clearance = 0.25
  double_helix = false
  head = 0
  head_fillet = 0
  height = 6
  helix_angle = 0
  module = 1
  num_teeth = 528
  numpoints = 20
  offset_hole = false
  offset_holeoffset = 10
  offset_holesize = 10
  pitch_diameter = 528
  pressure_angle = 20
  properties_from_tool = false
  reversed_backlash = false
  root_diameter = 525.5
  root_fillet = 0
  shift = 0
  simple = false
  transverse_pitch = 3.14159
  traverse_module = 1
  undercut = false
  version = 1.3.0
  expr: angular_backlash = backlash / pitch_diameter * 360 ° / pi
FEATURE [PartDesign::FeatureBase] BaseFeature
  BaseFeature = -> InvoluteGear004
  Suppressed = false
FEATURE [Sketcher::SketchObject] Sketch008
  ArcFitTolerance = 0
  AttachmentSupport = -> [BaseFeature]
  ExternalTypes = [0]
  FullyConstrained = true
  MakeInternals = false
  MapMode = 5
  Placement = pos=(0,0,6) rot=(0,0,1;0rad)
  sketch-geometry (1):
    g0: Circle CenterX=0 CenterY=0 CenterZ=0 NormalX=0 NormalY=0 NormalZ=1 AngleXU=0 Radius=260
  constraints (2):
    c: Coincident(g0,g-1)
    c: Diameter(g0) = 520
FEATURE [PartDesign::Pocket] Pocket005
  BaseFeature = -> BaseFeature
  Direction = (0,0,-1)
  Length = 2
  Length2 = 100
  Profile = -> Sketch008
  SideType = 0
  Suppressed = false
  Type = 0
  Type2 = 0
FEATURE [Sketcher::SketchObject] Sketch009
  ArcFitTolerance = 0
  AttachmentSupport = -> [Pocket005]
  ExternalTypes = [0]
  FullyConstrained = true
  MakeInternals = false
  MapMode = 5
  Placement = pos=(0,0,4) rot=(0,0,1;0rad)
  sketch-geometry (1):
    g0: Circle CenterX=0 CenterY=0 CenterZ=0 NormalX=0 NormalY=0 NormalZ=1 AngleXU=0 Radius=250
  constraints (2):
    c: Coincident(g0,g-1)
    c: Diameter(g0) = 500
FEATURE [PartDesign::Pocket] Pocket006
  BaseFeature = -> Pocket005
  Direction = (0,0,-1)
  Length = 5
  Length2 = 100
  Profile = -> Sketch009
  SideType = 0
  Suppressed = false
  Type = 1
  Type2 = 0
FEATURE [Sketcher::SketchObject] Sketch010
  ArcFitTolerance = 0
  AttachmentSupport = -> [Pocket006]
  ExternalTypes = [0]
  FullyConstrained = true
  MakeInternals = false
  MapMode = 5
  Placement = pos=(0,0,4) rot=(0,0,1;0rad)
  sketch-geometry (4):
    g0: ArcOfCircle CenterX=0 CenterY=254 CenterZ=0 NormalX=0 NormalY=0 NormalZ=1 AngleXU=0 Radius=2.1 StartAngle=3.14159 EndAngle=6.28319
    g1: ArcOfCircle CenterX=2e-16 CenterY=255 CenterZ=0 NormalX=0 NormalY=0 NormalZ=1 AngleXU=0 Radius=2.1 StartAngle=4.6e-15 EndAngle=3.14159
    g2: LineSegment StartX=2.1 StartY=254 StartZ=0 EndX=2.1 EndY=255 EndZ=0
    g3: LineSegment StartX=-2.1 StartY=254 StartZ=0 EndX=-2.1 EndY=255 EndZ=0
  constraints (10):
    c: Tangent(g0,g3) = 1.5708
    c: Tangent(g0,g2) = -1.5708
    c: Tangent(g2,g1) = -1.5708
    c: Tangent(g3,g1) = 1.5708
    c: Vertical(g2)
    c: Equal(g0,g1)
    c: PointOnObject(g0,g-2)
    c: Diameter(g0) = 4.2
    c: DistanceY(g2,g2) = 1
    c: DistanceY(g0) = 254
FEATURE [PartDesign::Pocket] Pocket007
  BaseFeature = -> Pocket006
  Direction = (0,0,-1)
  Length = 5
  Length2 = 100
  Profile = -> Sketch010
  SideType = 0
  Suppressed = false
  Type = 1
  Type2 = 0
FEATURE [PartDesign::PolarPattern] PolarPattern002
  Angle = 360
  Axis = -> Sketch010 [N_Axis]
  BaseFeature = -> Pocket007
  Mode = 0
  Occurrences = 36
  Offset = 120
  Originals = -> [Pocket007]
  SpacingPattern = [0]
  Spacings = [-1,-1,-1,-1,-1,-1,-1,-1,-1,-1,-1,-1,-1,-1,-1,-1,-1,-1,-1,-1,-1,-1,-1,-1,-1,-1,-1,-1,-1,-1,-1,-1,-1,-1,-1]
  Suppressed = false
  TransformMode = 0
FEATURE [Sketcher::SketchObject] Sketch011
  ArcFitTolerance = 0
  AttachmentSupport = -> [PolarPattern002]
  ExternalTypes = [0]
  FullyConstrained = true
  MakeInternals = false
  MapMode = 5
  Placement = pos=(0,0,6) rot=(0,0,1;0rad)
  sketch-geometry (3):
    g0: LineSegment StartX=-26.7392 StartY=298.806 StartZ=0 EndX=3.6e-15 EndY=0 EndZ=0
    g1: LineSegment StartX=0 StartY=0 StartZ=0 EndX=213.39 EndY=210.866 EndZ=0
    g2: ArcOfCircle CenterX=0 CenterY=0 CenterZ=0 NormalX=0 NormalY=0 NormalZ=1 AngleXU=0 Radius=300 StartAngle=1.66005 EndAngle=7.06263
  constraints (8):
    c: Coincident(g0,g-1)
    c: Coincident(g1,g0)
    c: Angle(g-2,g0) = 0.0892492
    c: Coincident(g2,g0)
    c: Coincident(g2,g0)
    c: Coincident(g2,g1)
    c: Distance(g0) = 300
    c: Angle(g1,g0) = 0.880597
FEATURE [PartDesign::Pocket] Pocket008
  BaseFeature = -> PolarPattern002
  Direction = (0,0,-1)
  Length = 5
  Length2 = 100
  Profile = -> Sketch011
  SideType = 0
  Suppressed = false
  Type = 1
  Type2 = 0
FEATURE [PartDesign::Body] Body003  label="gear_ring"
  AllowCompound = true
  BaseFeature = -> InvoluteGear004
  Group = -> [BaseFeature,Sketch008,Pocket005,Sketch009,Pocket006,Sketch010,Pocket007,PolarPattern002,Sketch011,Pocket008]
  Origin = -> Origin005
  Tip = -> Pocket008
FEATURE [App::Part] Part001  label="vertical-axis-main-gear"
  Group = -> [Body003,InvoluteGear004]
  Origin = -> Origin006
  Placement = pos=(0,0,22) rot=(1,0,0;3.14159rad)
FEATURE [Part::FeaturePython] InvoluteGear005  label="InvoluteGear008"  # WARN: FeaturePython — macro-defined, semantics opaque (R4)
  AttacherType = Attacher::AttachEngine3D
  addendum_diameter = 14
  angular_backlash = 0
  axle_hole = false
  axle_holesize = 10
  backlash = 0
  clearance = 0.25
  double_helix = false
  head = 0
  head_fillet = 0
  height = 55
  helix_angle = 0
  module = 1
  num_teeth = 12
  numpoints = 20
  offset_hole = false
  offset_holeoffset = 10
  offset_holesize = 10
  pitch_diameter = 12
  pressure_angle = 20
  properties_from_tool = false
  reversed_backlash = false
  root_diameter = 9.5
  root_fillet = 0
  shift = 0
  simple = false
  transverse_pitch = 3.14159
  traverse_module = 1
  undercut = false
  version = 1.3.0
  expr: angular_backlash = backlash / pitch_diameter * 360 ° / pi
FEATURE [PartDesign::FeatureBase] BaseFeature001
  BaseFeature = -> InvoluteGear005
  Suppressed = false
FEATURE [Sketcher::SketchObject] Sketch032
  ArcFitTolerance = 0
  AttachmentSupport = -> [BaseFeature001]
  ExternalTypes = [0]
  FullyConstrained = true
  MakeInternals = false
  MapMode = 5
  Placement = pos=(0,0,55) rot=(0,0,1;0rad)
  sketch-geometry (2):
    g0: ArcOfCircle CenterX=0 CenterY=0 CenterZ=0 NormalX=0 NormalY=0 NormalZ=1 AngleXU=0 Radius=2.5 StartAngle=0.643501 EndAngle=5.63968
    g1: LineSegment StartX=2 StartY=1.5 StartZ=0 EndX=2 EndY=-1.5 EndZ=0
  constraints (6):
    c: Coincident(g0,g-1)
    c: Diameter(g0) = 5
    c: Vertical(g1)
    c: Coincident(g0,g1)
    c: Coincident(g0,g1)
    c: DistanceX(g0) = 2
FEATURE [PartDesign::Pocket] Pocket019
  BaseFeature = -> BaseFeature001
  Direction = (0,0,-1)
  Length = 25
  Length2 = 100
  Profile = -> Sketch032
  SideType = 0
  Suppressed = false
  Type = 0
  Type2 = 0
FEATURE [Sketcher::SketchObject] Sketch033
  ArcFitTolerance = 0
  AttachmentSupport = -> [XZ_Plane014]
  ExternalGeometry = -> [Pocket019]
  ExternalTypes = [0]
  FullyConstrained = true
  MakeInternals = false
  MapMode = 5
  Placement = pos=(0,0,0) rot=(1,0,0;1.5708rad)
  sketch-geometry (4):
    g0: LineSegment StartX=4.5 StartY=36.4434 StartZ=0 EndX=4.5 EndY=55 EndZ=0
    g1: LineSegment StartX=4.5 StartY=55 StartZ=0 EndX=7 EndY=55 EndZ=0
    g2: LineSegment StartX=7 StartY=55 StartZ=0 EndX=7 EndY=35 EndZ=0
    g3: LineSegment StartX=7 StartY=35 StartZ=0 EndX=4.5 EndY=36.4434 EndZ=0
  constraints (12):
    c: Vertical(g0)
    c: Coincident(g0,g1)
    c: Coincident(g1,g2)
    c: Vertical(g2)
    c: Coincident(g2,g3)
    c: Coincident(g3,g0)
    c: DistanceX(g0) = 4.5
    c: DistanceX(g2) = 7
    c: DistanceY(g2,g2) = 20
    c: Horizontal(g1)
    c: Horizontal(g1,g-3)
    c: Angle(g2,g3) = 1.0472
FEATURE [PartDesign::Groove] Groove
  Angle = 360
  Angle2 = 60
  Axis = (0,2e-16,1)
  Base = (0,0,0)
  BaseFeature = -> Pocket019
  Profile = -> Sketch033
  ReferenceAxis = -> Sketch033 [V_Axis]
  Suppressed = false
  Type = 0
FEATURE [PartDesign::Body] Body009  label="vertical-axis-gear"
  AllowCompound = true
  BaseFeature = -> InvoluteGear005
  Group = -> [BaseFeature001,Sketch032,Pocket019,Sketch033,Groove]
  Origin = -> Origin014
  Tip = -> Groove
FEATURE [App::Part] Part002  label="vertical-axis-motor-gear"
  Group = -> [Body009,InvoluteGear005]
  Origin = -> Origin015
FEATURE [App::FeaturePython] Joint  label="Fixed008"  # Assembly joint (typed FeaturePython)
  Angle = 0
  AngleMax = 0
  AngleMin = 0
  Detach1 = false
  Detach2 = false
  Distance = 0
  Distance2 = 0
  EnableAngleMax = false
  EnableAngleMin = false
  EnableLengthMax = false
  EnableLengthMin = false
  JointType = 0 (Fixed)
  LengthMax = 0
  LengthMin = 0
  Placement1 = pos=(-1e-15,-1.42e-14,0) rot=(0,0,1;0rad)
  Placement2 = pos=(1e-16,5.08e-14,0) rot=(0,0,1;0rad)
  Reference1 = -> Assembly002 [Assembly001.Link032.Face2,Assembly001.Link032.Face2]
  Reference2 = -> Assembly002 [Assembly001.bearing_51126_hub_top.Face1,Assembly001.bearing_51126_hub_top.Face1]
  Suppressed = false
FEATURE [App::FeaturePython] Joint001  label="Fixed009"  # Assembly joint (typed FeaturePython)
  Angle = 0
  AngleMax = 0
  AngleMin = 0
  Detach1 = false
  Detach2 = false
  Distance = 0
  Distance2 = 0
  EnableAngleMax = false
  EnableAngleMin = false
  EnableLengthMax = false
  EnableLengthMin = false
  JointType = 0 (Fixed)
  LengthMax = 0
  LengthMin = 0
  Offset2 = pos=(0,18,-179) rot=(0,0,1;0rad)
  Placement2 = pos=(0,18,-179) rot=(0,0,1;0rad)
  Reference1 = -> Assembly002 [Assembly001.Link042.Origin017.YZ_Plane017.,Assembly001.Link042.Origin017.YZ_Plane017.]
  Reference2 = -> Assembly002 [Assembly001.Link032.Origin009.YZ_Plane009.,Assembly001.Link032.Origin009.YZ_Plane009.]
  Suppressed = false
FEATURE [App::FeaturePython] Joint002  label="Fixed010"  # Assembly joint (typed FeaturePython)
  Angle = 0
  AngleMax = 0
  AngleMin = 0
  Detach1 = false
  Detach2 = false
  Distance = 0
  Distance2 = 0
  EnableAngleMax = false
  EnableAngleMin = false
  EnableLengthMax = false
  EnableLengthMin = false
  JointType = 0 (Fixed)
  LengthMax = 0
  LengthMin = 0
  Offset2 = pos=(0,18,179) rot=(0,0,1;0rad)
  Placement2 = pos=(0,18,179) rot=(0,0,1;0rad)
  Reference1 = -> Assembly002 [Assembly001.Link041.Origin017.YZ_Plane017.,Assembly001.Link041.Origin017.YZ_Plane017.]
  Reference2 = -> Assembly002 [Assembly001.Link032.Origin009.YZ_Plane009.,Assembly001.Link032.Origin009.YZ_Plane009.]
  Suppressed = false
FEATURE [App::FeaturePython] Joint003  label="Fixed011"  # Assembly joint (typed FeaturePython)
  Angle = 0
  AngleMax = 0
  AngleMin = 0
  Detach1 = false
  Detach2 = false
  Distance = 0
  Distance2 = 0
  EnableAngleMax = false
  EnableAngleMin = false
  EnableLengthMax = false
  EnableLengthMin = false
  JointType = 0 (Fixed)
  LengthMax = 0
  LengthMin = 0
  Offset2 = pos=(0,18,-150) rot=(0,0,1;0rad)
  Placement2 = pos=(0,18,-150) rot=(0,0,1;0rad)
  Reference1 = -> Assembly002 [Assembly001.Link040.Origin016.XZ_Plane016.,Assembly001.Link040.Origin016.XZ_Plane016.]
  Reference2 = -> Assembly002 [Assembly001.Link032.Origin009.XZ_Plane009.,Assembly001.Link032.Origin009.XZ_Plane009.]
  Suppressed = false
FEATURE [App::FeaturePython] Joint004  label="Fixed012"  # Assembly joint (typed FeaturePython)
  Angle = 0
  AngleMax = 0
  AngleMin = 0
  Detach1 = false
  Detach2 = false
  Distance = 0
  Distance2 = 0
  EnableAngleMax = false
  EnableAngleMin = false
  EnableLengthMax = false
  EnableLengthMin = false
  JointType = 0 (Fixed)
  LengthMax = 0
  LengthMin = 0
  Placement2 = pos=(0,0,18) rot=(1,0,0;3.14159rad)
  Reference1 = -> Assembly002 [Assembly001.Link036.Edge3,Assembly001.Link036.Edge3]
  Reference2 = -> Assembly002 [Assembly001.Link032.Edge5,Assembly001.Link032.Edge5]
  Suppressed = false
FEATURE [App::FeaturePython] Joint005  label="Fixed013"  # Assembly joint (typed FeaturePython)
  Angle = 0
  AngleMax = 0
  AngleMin = 0
  Detach1 = false
  Detach2 = false
  Distance = 0
  Distance2 = 0
  EnableAngleMax = false
  EnableAngleMin = false
  EnableLengthMax = false
  EnableLengthMin = false
  JointType = 0 (Fixed)
  LengthMax = 0
  LengthMin = 0
  Placement1 = pos=(0,6.4e-15,29) rot=(1,0,0;3.14159rad)
  Reference1 = -> Assembly002 [Assembly001.bearing_51126_cover.Edge9,Assembly001.bearing_51126_cover.Edge9]
  Reference2 = -> Assembly002 [Assembly001.bearing_51126_hub_top.Edge7,Assembly001.bearing_51126_hub_top.Edge7]
  Suppressed = false
FEATURE [App::FeaturePython] Joint006  label="Fixed006"  # Assembly joint (typed FeaturePython)
  Angle = 0
  AngleMax = 0
  AngleMin = 0
  Detach1 = false
  Detach2 = false
  Distance = 0
  Distance2 = 0
  EnableAngleMax = false
  EnableAngleMin = false
  EnableLengthMax = false
  EnableLengthMin = false
  JointType = 0 (Fixed)
  LengthMax = 0
  LengthMin = 0
  Offset2 = pos=(0,18,270) rot=(0,0,1;0rad)
  Placement2 = pos=(0,18,270) rot=(0,0,1;0rad)
  Reference1 = -> Assembly002 [Assembly001.Link037.Origin012.XZ_Plane012.,Assembly001.Link037.Origin012.XZ_Plane012.]
  Reference2 = -> Assembly002 [Assembly001.Link032.Origin009.XZ_Plane009.,Assembly001.Link032.Origin009.XZ_Plane009.]
  Suppressed = false
FEATURE [App::FeaturePython] Joint007  label="Fixed007"  # Assembly joint (typed FeaturePython)
  Angle = 0
  AngleMax = 0
  AngleMin = 0
  Detach1 = false
  Detach2 = false
  Distance = 0
  Distance2 = 0
  EnableAngleMax = false
  EnableAngleMin = false
  EnableLengthMax = false
  EnableLengthMin = false
  JointType = 0 (Fixed)
  LengthMax = 0
  LengthMin = 0
  Placement1 = pos=(3.2e-15,-5.68e-14,40) rot=(0,0,1;0rad)
  Placement2 = pos=(0,0,3) rot=(0,0,1;0rad)
  Reference1 = -> Assembly002 [Assembly001.Link038.Edge11,Assembly001.Link038.Edge11]
  Reference2 = -> Assembly002 [Assembly001.Link037.Edge82,Assembly001.Link037.Edge82]
  Suppressed = false
FEATURE [App::FeaturePython] Joint008  label="Revolute008"  # Assembly joint (typed FeaturePython)
  Angle = 0
  AngleMax = 0
  AngleMin = 0
  Detach1 = false
  Detach2 = false
  Distance = 0
  Distance2 = 0
  EnableAngleMax = false
  EnableAngleMin = false
  EnableLengthMax = false
  EnableLengthMin = false
  JointType = 1 (Revolute)
  LengthMax = 0
  LengthMin = 0
  Placement1 = pos=(0,1.22e-14,55) rot=(0,0,1;0rad)
  Placement2 = pos=(3.4e-15,0,42) rot=(-1,0,0;3.14159rad)
  Reference1 = -> Assembly002 [Assembly001.Link039.Body009.Edge221,Assembly001.Link039.Body009.Edge221]
  Reference2 = -> Assembly002 [Assembly001.Link038.Edge44,Assembly001.Link038.Edge44]
  Suppressed = false
FEATURE [App::FeaturePython] Joint009  label="Revolute014"  # Assembly joint (typed FeaturePython)
  Angle = 0
  AngleMax = 0
  AngleMin = 0
  Detach1 = false
  Detach2 = false
  Distance = 0
  Distance2 = 0
  EnableAngleMax = false
  EnableAngleMin = false
  EnableLengthMax = false
  EnableLengthMin = false
  JointType = 1 (Revolute)
  LengthMax = 0
  LengthMin = 0
  Offset2 = pos=(0,0,30) rot=(0,0,1;0rad)
  Placement2 = pos=(0,0,48) rot=(0,0,1;0rad)
  Reference1 = -> Assembly002 [Assembly001.Link032.Edge2,Assembly001.Link032.Edge2]
  Reference2 = -> Assembly002 [Assembly.Link028.Edge3,Assembly.Link028.Edge3]
  Suppressed = false
FEATURE [App::FeaturePython] GroundedJoint003  label="GroundedJoint006"  # Assembly grounded joint (typed FeaturePython)
  ObjectToGround = -> Link028
FEATURE [Assembly::JointGroup] Joints
  Group = -> [Fixed,Fixed001,Fixed002,Fixed003,Fixed004,Fixed005,GroundedJoint003]
FEATURE [Assembly::AssemblyObject] Assembly  label="base"
  Group = -> [Joints,Link028,Link029,Fixed,Link030,Fixed001,Link031,Fixed002,Link033,Fixed003,Link035,Link034,Fixed004,Fixed005,GroundedJoint003]
  Origin = -> Origin002
  Type = Assembly
FEATURE [App::FeaturePython] GroundedJoint  label="GroundedJoint005"  # Assembly grounded joint (typed FeaturePython)
  ObjectToGround = -> Assembly
FEATURE [App::FeaturePython] GroundedJoint004  label="GroundedJoint007"  # Assembly grounded joint (typed FeaturePython)
  ObjectToGround = -> Link032
FEATURE [App::FeaturePython] Joint010  label="Fixed020"  # Assembly joint (typed FeaturePython)
  Angle = 0
  AngleMax = 0
  AngleMin = 0
  Detach1 = false
  Detach2 = false
  Distance = 0
  Distance2 = 0
  EnableAngleMax = false
  EnableAngleMin = false
  EnableLengthMax = false
  EnableLengthMin = false
  JointType = 0 (Fixed)
  LengthMax = 0
  LengthMin = 0
  Offset2 = pos=(288,-55,0) rot=(0,0,-1;2.89725rad)
  Placement1 = pos=(-14,-52.0592,10) rot=(0,0,1;0rad)
  Placement2 = pos=(-9,91.2121,584.187) rot=(0.120974,0.985257,0.120974;1.58565rad)
  Reference1 = -> Assembly002 [Assembly001.Link045.Face47,Assembly001.Link045.Face47]
  Reference2 = -> Assembly002 [Assembly001.Link042.Face4,Assembly001.Link042.Face4]
  Suppressed = false
FEATURE [App::FeaturePython] Joint011  label="Fixed021"  # Assembly joint (typed FeaturePython)
  Angle = 0
  AngleMax = 0
  AngleMin = 0
  Detach1 = false
  Detach2 = false
  Distance = 0
  Distance2 = 0
  EnableAngleMax = false
  EnableAngleMin = false
  EnableLengthMax = false
  EnableLengthMin = false
  JointType = 0 (Fixed)
  LengthMax = 0
  LengthMin = 0
  Placement1 = pos=(1.137e-13,5.68e-14,-7.95) rot=(0,0,1;0rad)
  Placement2 = pos=(-40,0,4) rot=(-1,0,0;3.14159rad)
  Reference1 = -> Assembly002 [Assembly001.Link046.Edge2,Assembly001.Link046.Edge2]
  Reference2 = -> Assembly002 [Assembly001.Link045.Edge131,Assembly001.Link045.Edge131]
  Suppressed = false
FEATURE [App::FeaturePython] Joint012  label="Fixed022"  # Assembly joint (typed FeaturePython)
  Angle = 0
  AngleMax = 0
  AngleMin = 0
  Detach1 = false
  Detach2 = false
  Distance = 0
  Distance2 = 0
  EnableAngleMax = false
  EnableAngleMin = false
  EnableLengthMax = false
  EnableLengthMin = false
  JointType = 0 (Fixed)
  LengthMax = 0
  LengthMin = 0
  Offset2 = pos=(2,0,0) rot=(0,0,1;0rad)
  Placement1 = pos=(0,-5.68e-14,40) rot=(0,0,1;0rad)
  Placement2 = pos=(-1.2506e-12,-5.68e-14,16) rot=(0,0,1;0rad)
  Reference1 = -> Assembly002 [Assembly001.Link050.Edge11,Assembly001.Link050.Edge11]
  Reference2 = -> Assembly002 [Assembly001.Link045.Edge205,Assembly001.Link045.Edge205]
  Suppressed = false
FEATURE [App::FeaturePython] Joint013  label="Fixed024"  # Assembly joint (typed FeaturePython)
  Angle = 0
  AngleMax = 0
  AngleMin = 0
  Detach1 = false
  Detach2 = false
  Distance = 0
  Distance2 = 0
  EnableAngleMax = false
  EnableAngleMin = false
  EnableLengthMax = false
  EnableLengthMin = false
  JointType = 0 (Fixed)
  LengthMax = 0
  LengthMin = 0
  Placement1 = pos=(0,0,1) rot=(0,0,1;0rad)
  Placement2 = pos=(1.137e-13,5.68e-14,7.95) rot=(0,0,1;0rad)
  Reference1 = -> Assembly002 [Assembly001.Link048.Edge3,Assembly001.Link048.Edge3]
  Reference2 = -> Assembly002 [Assembly001.Link046.Edge17,Assembly001.Link046.Edge17]
  Suppressed = false
FEATURE [App::FeaturePython] Joint014  label="Fixed025"  # Assembly joint (typed FeaturePython)
  Angle = 0
  AngleMax = 0
  AngleMin = 0
  Detach1 = false
  Detach2 = false
  Distance = 0
  Distance2 = 0
  EnableAngleMax = false
  EnableAngleMin = false
  EnableLengthMax = false
  EnableLengthMin = false
  JointType = 0 (Fixed)
  LengthMax = 0
  LengthMin = 0
  Placement1 = pos=(0,0,-10) rot=(0.707107,0.707107,0;3.14159rad)
  Reference1 = -> Assembly002 [Assembly001.Link047.Body017.Edge396,Assembly001.Link047.Body017.Edge396]
  Reference2 = -> Assembly002 [Assembly001.Link048.Edge11,Assembly001.Link048.Edge11]
  Suppressed = false
FEATURE [App::FeaturePython] Joint015  label="Fixed027"  # Assembly joint (typed FeaturePython)
  Angle = 0
  AngleMax = 0
  AngleMin = 0
  Detach1 = false
  Detach2 = false
  Distance = 0
  Distance2 = 0
  EnableAngleMax = false
  EnableAngleMin = false
  EnableLengthMax = false
  EnableLengthMin = false
  JointType = 0 (Fixed)
  LengthMax = 0
  LengthMin = 0
  Placement1 = pos=(0,0,8) rot=(0,0,1;0rad)
  Placement2 = pos=(0,0,5) rot=(0,0,1;1.5708rad)
  Reference1 = -> Assembly002 [Assembly001.Link049.Body019.Edge1,Assembly001.Link049.Body019.Edge1]
  Reference2 = -> Assembly002 [Assembly001.Link047.Body017.Edge376,Assembly001.Link047.Body017.Edge376]
  Suppressed = false
FEATURE [App::FeaturePython] Joint016  label="Revolute028"  # Assembly joint (typed FeaturePython)
  Angle = 0
  AngleMax = 0
  AngleMin = 0
  Detach1 = false
  Detach2 = false
  Distance = 0
  Distance2 = 0
  EnableAngleMax = false
  EnableAngleMin = false
  EnableLengthMax = false
  EnableLengthMin = false
  JointType = 1 (Revolute)
  LengthMax = 0
  LengthMin = 0
  Offset2 = pos=(0,0,-9) rot=(0,0,1;0rad)
  Placement1 = pos=(0,0,0) rot=(1,0,0;3.14159rad)
  Placement2 = pos=(-3e-16,5.63e-14,54.5) rot=(0,0,1;0rad)
  Reference1 = -> Assembly002 [Assembly001.Link051.Body020.Edge298,Assembly001.Link051.Body020.Edge298]
  Reference2 = -> Assembly002 [Assembly001.Link050.Edge52,Assembly001.Link050.Edge52]
  Suppressed = false
FEATURE [App::FeaturePython] GroundedJoint005  label="GroundedJoint008"  # Assembly grounded joint (typed FeaturePython)
  ObjectToGround = -> Link043
FEATURE [App::FeaturePython] Joint018  label="Revolute030"  # Assembly joint (typed FeaturePython)
  Angle = 0
  AngleMax = 0
  AngleMin = 0
  Detach1 = false
  Detach2 = false
  Distance = 0
  Distance2 = 0
  EnableAngleMax = false
  EnableAngleMin = false
  EnableLengthMax = false
  EnableLengthMin = false
  JointType = 1 (Revolute)
  LengthMax = 0
  LengthMin = 0
  Placement1 = pos=(-170,1.9153e-11,420) rot=(-0.57735,0.57735,0.57735;4.18879rad)
  Placement2 = pos=(9,6.467e-11,580) rot=(0.57735,0.57735,0.57735;2.0944rad)
  Reference1 = -> Assembly002 [Assembly003.Link043.Edge41,Assembly003.Link043.Edge41]
  Reference2 = -> Assembly002 [Assembly001.Link042.Edge17,Assembly001.Link042.Edge17]
  Suppressed = false
FEATURE [Assembly::JointGroup] Joints002
  Group = -> [Joint009,GroundedJoint,Joint018]
FEATURE [App::FeaturePython] Joint019  label="Fixed029"  # Assembly joint (typed FeaturePython)
  Angle = 0
  AngleMax = 0
  AngleMin = 0
  Detach1 = false
  Detach2 = false
  Distance = 0
  Distance2 = 0
  EnableAngleMax = false
  EnableAngleMin = false
  EnableLengthMax = false
  EnableLengthMin = false
  JointType = 0 (Fixed)
  LengthMax = 0
  LengthMin = 0
  Offset2 = pos=(0,0,-12) rot=(0,0,1;3.14159rad)
  Placement1 = pos=(0,0,29) rot=(0,0,1;0rad)
  Placement2 = pos=(-162,6.57362e-11,420) rot=(0.57735,-0.57735,0.57735;4.18879rad)
  Reference1 = -> Assembly002 [Assembly003.Link044.Body013.Edge483,Assembly003.Link044.Body013.Edge483]
  Reference2 = -> Assembly002 [Assembly003.Link043.Edge14,Assembly003.Link043.Edge14]
  Suppressed = false
FEATURE [Assembly::JointGroup] Joints003
  Group = -> [GroundedJoint005,Joint019]
FEATURE [Assembly::AssemblyObject] Assembly003  label="tube"
  Group = -> [Joints003,Link043,Link044,GroundedJoint005,Joint019]
  Origin = -> Origin022
  Placement = pos=(-8.47407,-193.419,273.284) rot=(-0.995769,0.021803,-0.089272;0.481038rad)
  Type = Assembly
FEATURE [Sketcher::SketchObject] Sketch092
  ArcFitTolerance = 0
  AttachmentSupport = -> [XY_Plane033]
  ExternalTypes = [0]
  FullyConstrained = true
  MakeInternals = false
  MapMode = 5
  sketch-geometry (1):
    g0: Circle CenterX=0 CenterY=0 CenterZ=0 NormalX=0 NormalY=0 NormalZ=1 AngleXU=0 Radius=8
  constraints (2):
    c: Coincident(g0,g-1)
    c: Diameter(g0) = 16
FEATURE [PartDesign::Pad] Pad032
  Direction = (0,0,1)
  Length = 4
  Length2 = 100
  Profile = -> Sketch092
  SideType = 0
  Suppressed = false
  Type = 0
  Type2 = 0
FEATURE [Sketcher::SketchObject] Sketch093
  ArcFitTolerance = 0
  AttachmentSupport = -> [Pad032]
  ExternalTypes = [0]
  FullyConstrained = true
  MakeInternals = false
  MapMode = 5
  Placement = pos=(0,0,4) rot=(0,0,1;0rad)
  sketch-geometry (1):
    g0: Circle CenterX=0 CenterY=0 CenterZ=0 NormalX=0 NormalY=0 NormalZ=1 AngleXU=0 Radius=4
  constraints (2):
    c: Coincident(g0,g-1)
    c: Diameter(g0) = 8
FEATURE [PartDesign::Pad] Pad033
  BaseFeature = -> Pad032
  Direction = (0,0,1)
  Length = 7
  Length2 = 100
  Profile = -> Sketch093
  SideType = 0
  Suppressed = false
  Type = 0
  Type2 = 0
FEATURE [Sketcher::SketchObject] Sketch094
  ArcFitTolerance = 0
  AttachmentSupport = -> [Pad033]
  ExternalTypes = [0]
  FullyConstrained = true
  MakeInternals = false
  MapMode = 5
  Placement = pos=(0,0,11) rot=(0,0,1;0rad)
  sketch-geometry (4):
    g0: ArcOfCircle CenterX=0 CenterY=0 CenterZ=0 NormalX=0 NormalY=0 NormalZ=1 AngleXU=0 Radius=4.05 StartAngle=5.44901 EndAngle=7.11736
    g1: LineSegment StartX=1 StartY=3 StartZ=0 EndX=2.72075 EndY=3 EndZ=0
    g2: LineSegment StartX=1 StartY=-3 StartZ=0 EndX=2.72075 EndY=-3 EndZ=0
    g3: ArcOfCircle CenterX=1 CenterY=0 CenterZ=0 NormalX=0 NormalY=0 NormalZ=1 AngleXU=0 Radius=3 StartAngle=1.5708 EndAngle=4.71239
  constraints (11):
    c: Coincident(g0,g-1)
    c: Diameter(g0) = 8.1
    c: Horizontal(g2)
    c: Horizontal(g1)
    c: Coincident(g0,g2)
    c: Coincident(g0,g1)
    c: PointOnObject(g3,g-1)
    c: DistanceX(g3) = 1
    c: Tangent(g3,g1) = 1.5708
    c: Tangent(g3,g2) = -1.5708
    c: Diameter(g3) = 6
FEATURE [PartDesign::Pocket] Pocket052
  BaseFeature = -> Pad033
  Direction = (0,0,-1)
  Length = 5
  Length2 = 100
  Profile = -> Sketch094
  SideType = 0
  Suppressed = false
  Type = 1
  Type2 = 0
FEATURE [PartDesign::Fillet] Fillet005
  Base = -> Pocket052 [Edge15,Edge20]
  BaseFeature = -> Pocket052
  Radius = 0.3
  SupportTransform = true
  Suppressed = false
  UseAllEdges = false
FEATURE [PartDesign::Fillet] Fillet006
  Base = -> Fillet005 [Edge20,Edge24]
  BaseFeature = -> Fillet005
  Radius = 2
  SupportTransform = true
  Suppressed = false
  UseAllEdges = false
FEATURE [PartDesign::Chamfer] Chamfer010
  Angle = 5
  Base = -> Fillet006 [Edge9]
  BaseFeature = -> Fillet006
  ChamferType = 2
  FlipDirection = false
  Size = 3
  Size2 = 1
  SupportTransform = true
  Suppressed = false
  UseAllEdges = false
FEATURE [PartDesign::Chamfer] Chamfer011
  Angle = 45
  Base = -> Chamfer010 [Edge34,Edge14,Edge18,Edge22,Edge26,Edge29]
  BaseFeature = -> Chamfer010
  ChamferType = 1
  FlipDirection = false
  Size = 0.5
  Size2 = 1
  SupportTransform = true
  Suppressed = false
  UseAllEdges = false
FEATURE [PartDesign::Body] Body021  label="eccentric-sleeve"
  AllowCompound = true
  Group = -> [Sketch092,Pad032,Sketch093,Pad033,Sketch094,Pocket052,Fillet005,Fillet006,Chamfer010,Chamfer011]
  Origin = -> Origin064
  Tip = -> Chamfer011
FEATURE [App::Point] Origin065
  Role = Origin
FEATURE [App::Link] eccentric_sleeve  label="eccentric-sleeve001"
  LinkPlacement = pos=(-173.189,41.3437,593.013) rot=(0.692519,-0.259604,0.67307;3.73557rad)
  LinkedObject = -> Body021
  Placement = pos=(-173.189,41.3437,593.013) rot=(0.692519,-0.259604,0.67307;3.73557rad)
FEATURE [App::Link] eccentric_sleeve001  label="eccentric-sleeve002"
  LinkPlacement = pos=(-166.002,-64.4771,593.001) rot=(0.66455,0.302156,0.683428;2.64001rad)
  LinkedObject = -> Body021
  Placement = pos=(-166.002,-64.4771,593.001) rot=(0.66455,0.302156,0.683428;2.64001rad)
FEATURE [App::Link] eccentric_sleeve002  label="eccentric-sleeve003"
  LinkPlacement = pos=(166.023,64.4778,592.922) rot=(-0.390542,0.858911,0.331283;4.5891rad)
  LinkedObject = -> Body021
  Placement = pos=(166.023,64.4778,592.922) rot=(-0.390542,0.858911,0.331283;4.5891rad)
FEATURE [App::Link] eccentric_sleeve003  label="eccentric-sleeve004"
  LinkPlacement = pos=(173.21,-41.3438,592.931) rot=(-0.324305,-0.865171,0.382499;1.74278rad)
  LinkedObject = -> Body021
  Placement = pos=(173.21,-41.3438,592.931) rot=(-0.324305,-0.865171,0.382499;1.74278rad)
FEATURE [App::FeaturePython] Joint020  label="Fixed031"  # Assembly joint (typed FeaturePython)
  Angle = 0
  AngleMax = 0
  AngleMin = 0
  Detach1 = false
  Detach2 = false
  Distance = 0
  Distance2 = 0
  EnableAngleMax = false
  EnableAngleMin = false
  EnableLengthMax = false
  EnableLengthMin = false
  JointType = 0 (Fixed)
  LengthMax = 0
  LengthMin = 0
  Offset2 = pos=(0,0,0) rot=(0,0,1;2.35619rad)
  Placement2 = pos=(-9,53.033,526.967) rot=(0.678598,-0.281085,0.678598;3.68962rad)
  Reference1 = -> Assembly002 [Assembly001.eccentric_sleeve002.Edge36,Assembly001.eccentric_sleeve002.Edge36]
  Reference2 = -> Assembly002 [Assembly001.Link041.Edge12,Assembly001.Link041.Edge12]
  Suppressed = false
FEATURE [App::FeaturePython] Joint021  label="Fixed032"  # Assembly joint (typed FeaturePython)
  Angle = 0
  AngleMax = 0
  AngleMin = 0
  Detach1 = false
  Detach2 = false
  Distance = 0
  Distance2 = 0
  EnableAngleMax = false
  EnableAngleMin = false
  EnableLengthMax = false
  EnableLengthMin = false
  JointType = 0 (Fixed)
  LengthMax = 0
  LengthMin = 0
  Offset2 = pos=(0,0,0) rot=(0,0,1;0.785398rad)
  Placement2 = pos=(-9,-53.033,526.967) rot=(0.678598,0.281085,0.678598;2.59356rad)
  Reference1 = -> Assembly002 [Assembly001.eccentric_sleeve003.Chamfer011.Edge32]
  Reference2 = -> Assembly002 [Assembly001.Link041.Edge14,Assembly001.Link041.Edge14]
  Suppressed = false
FEATURE [App::FeaturePython] Joint022  label="Fixed033"  # Assembly joint (typed FeaturePython)
  Angle = 0
  AngleMax = 0
  AngleMin = 0
  Detach1 = false
  Detach2 = false
  Distance = 0
  Distance2 = 0
  EnableAngleMax = false
  EnableAngleMin = false
  EnableLengthMax = false
  EnableLengthMin = false
  JointType = 0 (Fixed)
  LengthMax = 0
  LengthMin = 0
  Offset2 = pos=(0,0,0) rot=(0,0,1;2.35619rad)
  Placement2 = pos=(9,53.033,526.967) rot=(0.678598,-0.281085,0.678598;3.68962rad)
  Reference1 = -> Assembly002 [Assembly001.eccentric_sleeve.Chamfer011.Edge32]
  Reference2 = -> Assembly002 [Assembly001.Link042.Edge16,Assembly001.Link042.Edge16]
  Suppressed = false
FEATURE [App::FeaturePython] Joint023  label="Fixed034"  # Assembly joint (typed FeaturePython)
  Angle = 0
  AngleMax = 0
  AngleMin = 0
  Detach1 = false
  Detach2 = false
  Distance = 0
  Distance2 = 0
  EnableAngleMax = false
  EnableAngleMin = false
  EnableLengthMax = false
  EnableLengthMin = false
  JointType = 0 (Fixed)
  LengthMax = 0
  LengthMin = 0
  Offset2 = pos=(0,0,0) rot=(0,0,1;0.785398rad)
  Placement2 = pos=(9,-53.033,526.967) rot=(0.678598,0.281085,0.678598;2.59356rad)
  Reference1 = -> Assembly002 [Assembly001.eccentric_sleeve001.Chamfer011.Edge32]
  Reference2 = -> Assembly002 [Assembly001.Link042.Edge18,Assembly001.Link042.Edge18]
  Suppressed = false
FEATURE [Part::Feature] Part__Feature  label="_608-2RSH_PART1"
  shape: bbox 7 x 17.36 x 17.36 mm, 26 faces (baked)
FEATURE [Part::Feature] Part__Feature001  label="_608-2RSH_PART2"
  shape: bbox 7 x 23.81 x 23.81 mm, 14 faces (baked)
FEATURE [Part::Feature] Part__Feature002  label="_608-2RSH_PART3"
  shape: bbox 3.969 x 3.969 x 3.969 mm, 1 faces (baked)
FEATURE [Part::Feature] Part__Feature003  label="_608-2RSH_PART001"
  Placement = pos=(0,0,0) rot=(-1,0,0;0.897598rad)
  shape: bbox 3.969 x 3.969 x 3.969 mm, 1 faces (baked)
FEATURE [Part::Feature] Part__Feature004  label="_608-2RSH_PART002"
  Placement = pos=(0,0,0) rot=(-1,0,0;1.7952rad)
  shape: bbox 3.969 x 3.969 x 3.969 mm, 1 faces (baked)
FEATURE [Part::Feature] Part__Feature005  label="_608-2RSH_PART003"
  Placement = pos=(0,0,0) rot=(1,0,0;3.59039rad)
  shape: bbox 3.969 x 3.969 x 3.969 mm, 1 faces (baked)
FEATURE [Part::Feature] Part__Feature006  label="_608-2RSH_PART004"
  Placement = pos=(0,0,0) rot=(1,0,0;2.69279rad)
  shape: bbox 3.969 x 3.969 x 3.969 mm, 1 faces (baked)
FEATURE [Part::Feature] Part__Feature007  label="_608-2RSH_PART005"
  Placement = pos=(0,0,0) rot=(1,0,0;1.7952rad)
  shape: bbox 3.969 x 3.969 x 3.969 mm, 1 faces (baked)
FEATURE [Part::Feature] Part__Feature008  label="_608-2RSH_PART006"
  Placement = pos=(0,0,0) rot=(1,0,0;0.897598rad)
  shape: bbox 3.969 x 3.969 x 3.969 mm, 1 faces (baked)
FEATURE [App::Part] _608_2RSH  label="bearing-608"
  Group = -> [Part__Feature,Part__Feature001,Part__Feature002,Part__Feature003,Part__Feature004,Part__Feature005,Part__Feature006,Part__Feature007,Part__Feature008]
  Origin = -> Origin066
FEATURE [App::DocumentObjectGroup] Group  label="parts"
  Group = -> [Body021,Body,_608_2RSH,Part,Body001,Body002,Part001,Body004,Body005,Body006,Body007,Body008,Part002,Body010,Body011,Body014,Part003,Body015,Body016,Part004,Body018,Part005,Part006]
FEATURE [App::Point] Origin067
  Role = Origin
FEATURE [App::Link] bearing_608  label="bearing-51127"
  LinkPlacement = pos=(155.051,63.7644,592.959) rot=(0.999317,0.034139,-0.014168;3.92654rad)
  LinkedObject = -> _608_2RSH
  Placement = pos=(155.051,63.7644,592.959) rot=(0.999317,0.034139,-0.014168;3.92654rad)
FEATURE [App::Link] bearing_609  label="bearing-51128"
  LinkPlacement = pos=(162.238,-42.0562,592.896) rot=(-0.999317,-0.034236,-0.01393;3.92646rad)
  LinkedObject = -> _608_2RSH
  Placement = pos=(162.238,-42.0562,592.896) rot=(-0.999317,-0.034236,-0.01393;3.92646rad)
FEATURE [App::Link] bearing_610  label="bearing-51129"
  LinkPlacement = pos=(-169.188,41.5791,592.974) rot=(0.999317,0.034139,-0.014168;3.92654rad)
  LinkedObject = -> _608_2RSH
  Placement = pos=(-169.188,41.5791,592.974) rot=(0.999317,0.034139,-0.014168;3.92654rad)
FEATURE [App::Link] bearing_611  label="bearing-51130"
  LinkPlacement = pos=(-162,-64.2407,593.036) rot=(0.999317,0.034237,0.013929;2.3567rad)
  LinkedObject = -> _608_2RSH
  Placement = pos=(-162,-64.2407,593.036) rot=(0.999317,0.034237,0.013929;2.3567rad)
FEATURE [App::FeaturePython] Joint024  label="Fixed035"  # Assembly joint (typed FeaturePython)
  Angle = 0
  AngleMax = 0
  AngleMin = 0
  Detach1 = false
  Detach2 = false
  Distance = 0
  Distance2 = 0
  EnableAngleMax = false
  EnableAngleMin = false
  EnableLengthMax = false
  EnableLengthMin = false
  JointType = 0 (Fixed)
  LengthMax = 0
  LengthMin = 0
  Placement1 = pos=(7,0,0) rot=(0,1,0;1.5708rad)
  Placement2 = pos=(5.68e-14,1.137e-13,4) rot=(0,0,1;0rad)
  Reference1 = -> Assembly002 [Assembly001.bearing_608.Part__Feature.Edge23,Assembly001.bearing_608.Part__Feature.Edge23]
  Reference2 = -> Assembly002 [Assembly001.eccentric_sleeve002.Edge16,Assembly001.eccentric_sleeve002.Edge16]
  Suppressed = false
FEATURE [App::FeaturePython] Joint025  label="Fixed036"  # Assembly joint (typed FeaturePython)
  Angle = 0
  AngleMax = 0
  AngleMin = 0
  Detach1 = false
  Detach2 = false
  Distance = 0
  Distance2 = 0
  EnableAngleMax = false
  EnableAngleMin = false
  EnableLengthMax = false
  EnableLengthMin = false
  JointType = 0 (Fixed)
  LengthMax = 0
  LengthMin = 0
  Placement1 = pos=(7,0,0) rot=(0,1,0;1.5708rad)
  Placement2 = pos=(0,0,4) rot=(0,0,1;0rad)
  Reference1 = -> Assembly002 [Assembly001.bearing_609.Part__Feature.Edge23,Assembly001.bearing_609.Part__Feature.Edge23]
  Reference2 = -> Assembly002 [Assembly001.eccentric_sleeve003.Edge13,Assembly001.eccentric_sleeve003.Edge13]
  Suppressed = false
FEATURE [App::FeaturePython] Joint026  label="Fixed037"  # Assembly joint (typed FeaturePython)
  Angle = 0
  AngleMax = 0
  AngleMin = 0
  Detach1 = false
  Detach2 = false
  Distance = 0
  Distance2 = 0
  EnableAngleMax = false
  EnableAngleMin = false
  EnableLengthMax = false
  EnableLengthMin = false
  JointType = 0 (Fixed)
  LengthMax = 0
  LengthMin = 0
  Placement1 = pos=(0,0,0) rot=(0,1,0;1.5708rad)
  Placement2 = pos=(-5.68e-14,5.68e-14,4) rot=(0,0,1;0rad)
  Reference1 = -> Assembly002 [Assembly001.bearing_610.Part__Feature.Edge29,Assembly001.bearing_610.Part__Feature.Edge29]
  Reference2 = -> Assembly002 [Assembly001.eccentric_sleeve.Edge13,Assembly001.eccentric_sleeve.Edge13]
  Suppressed = false
FEATURE [App::FeaturePython] Joint027  label="Fixed038"  # Assembly joint (typed FeaturePython)
  Angle = 0
  AngleMax = 0
  AngleMin = 0
  Detach1 = false
  Detach2 = false
  Distance = 0
  Distance2 = 0
  EnableAngleMax = false
  EnableAngleMin = false
  EnableLengthMax = false
  EnableLengthMin = false
  JointType = 0 (Fixed)
  LengthMax = 0
  LengthMin = 0
  Placement1 = pos=(0,0,0) rot=(0,1,0;1.5708rad)
  Placement2 = pos=(0,0,4) rot=(0,0,1;0rad)
  Reference1 = -> Assembly002 [Assembly001.bearing_611.Part__Feature.Edge29,Assembly001.bearing_611.Part__Feature.Edge29]
  Reference2 = -> Assembly002 [Assembly001.eccentric_sleeve001.Edge13,Assembly001.eccentric_sleeve001.Edge13]
  Suppressed = false
FEATURE [Assembly::JointGroup] Joints001
  Group = -> [Joint,Joint001,Joint002,Joint003,Joint004,Joint005,Joint006,Joint007,Joint008,GroundedJoint004,Joint010,Joint011,Joint012,Joint013,Joint014,Joint015,Joint016,Joint020,Joint021,Joint022,Joint023,Joint024,Joint025,Joint026,Joint027]
FEATURE [Assembly::AssemblyObject] Assembly001  label="fork"
  Group = -> [Joints001,Link032,bearing_51126_hub_top,bearing_51126_cover,Link036,Link037,Link038,Link039,Link040,Link041,Link042,Link045,Link046,Link048,Link047,Link049,Link050,Link051,Joint,Joint001,Joint002,Joint003,Joint004,Joint005,Joint006,Joint007,Joint008,GroundedJoint004,Joint010,Joint011,Joint012,Joint013,Joint014,Joint015,Joint016,eccentric_sleeve,eccentric_sleeve001,eccentric_sleeve002,+13 more]
  Origin = -> Origin007
  Placement = pos=(0,0,-1.95e-14) rot=(0,0,-1;0.111878rad)
  Type = Assembly
FEATURE [Assembly::AssemblyObject] Assembly002  label="telescope"
  Group = -> [Joints002,Assembly,Assembly001,Assembly003,Joint009,GroundedJoint,Joint018]
  Origin = -> Origin008
  Type = Assembly
